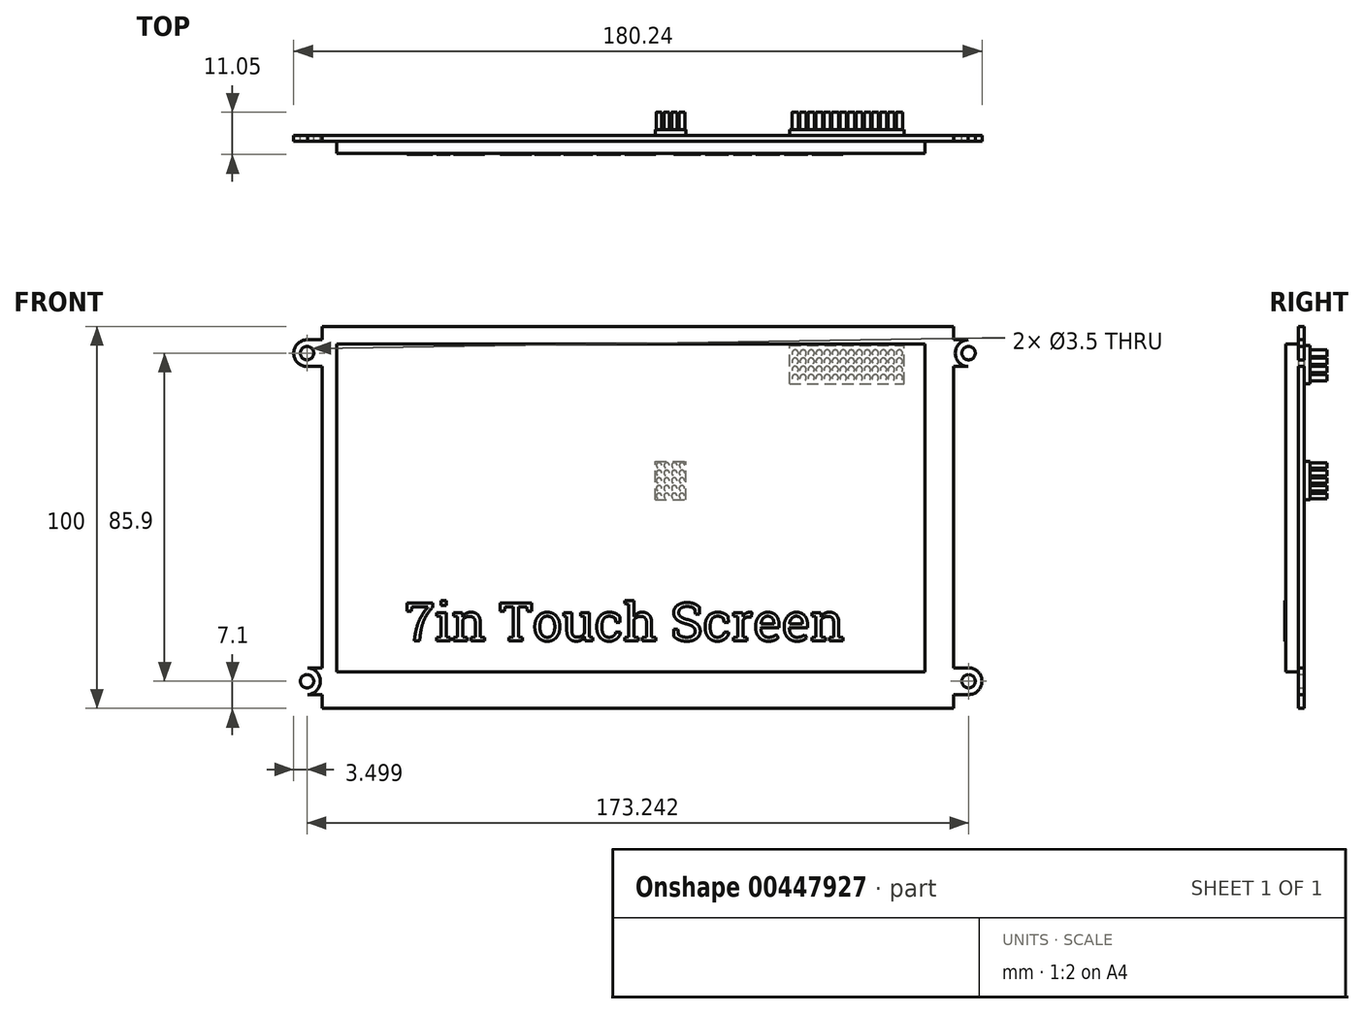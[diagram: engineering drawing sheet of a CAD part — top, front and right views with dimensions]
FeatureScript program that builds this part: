
annotation { "Feature Type Name" : "Feature", "Feature Type Description" : "" }
export const myFeature = defineFeature(function(context is Context, id is Id, definition is map)
    precondition{}
    {
        {
            var Q0;
            Q0=qCreatedBy(makeId("Front.planeOp"),FACE);
            var sketch = newSketch(context, id + "F0", { "sketchPlane" : qUnion([Q0])});
            skPoint(sketch, "E0.middle", {"position": v(0, 0) * mm});
            skCircle(sketch, "E1", {"center": v(-86.62, 42.95) * mm, "radius": 1.75 * mm});
            skLineSegment(sketch, "E2.bottom", {"start": v(-82.7, 46.45) * mm, "end": v(-86.45, 46.45) * mm});
            skLineSegment(sketch, "E2.top", {"start": v(-82.7, 39.45) * mm, "end": v(-86.45, 39.45) * mm});
            skLineSegment(sketch, "E2.left", {"start": v(-82.7, 46.45) * mm, "end": v(-82.7, 39.45) * mm});
            skCircle(sketch, "E3", {"center": v(-86.62, 42.95) * mm, "radius": 3.5 * mm});
            skPoint(sketch, "E4", {"position": v(-86.45, 46.45) * mm});
            skPoint(sketch, "E5", {"position": v(-86.45, 39.45) * mm});
            skPoint(sketch, "E6.MirrorP", {"position": v(86.62, 42.95) * mm});
            skCircle(sketch, "E7.MirrorC", {"center": v(86.62, 42.95) * mm, "radius": 1.75 * mm});
            skCircle(sketch, "E8.MirrorC", {"center": v(86.62, 42.95) * mm, "radius": 3.5 * mm});
            skLineSegment(sketch, "E9.MirrorCS", {"start": v(82.7, 39.45) * mm, "end": v(86.45, 39.45) * mm});
            skLineSegment(sketch, "E10.MirrorCS", {"start": v(82.7, 46.45) * mm, "end": v(82.7, 39.45) * mm});
            skLineSegment(sketch, "E11.MirrorCS", {"start": v(82.7, 46.45) * mm, "end": v(86.45, 46.45) * mm});
            skCircle(sketch, "E12.MirrorC", {"center": v(-86.62, -42.95) * mm, "radius": 1.75 * mm});
            skCircle(sketch, "E13.MirrorC", {"center": v(86.62, -42.95) * mm, "radius": 1.75 * mm});
            skLineSegment(sketch, "E14.MirrorCS", {"start": v(-82.7, -39.45) * mm, "end": v(-86.45, -39.45) * mm});
            skLineSegment(sketch, "E15.MirrorCS", {"start": v(-82.7, -46.45) * mm, "end": v(-82.7, -39.45) * mm});
            skLineSegment(sketch, "E16.MirrorCS", {"start": v(82.7, -46.45) * mm, "end": v(86.45, -46.45) * mm});
            skLineSegment(sketch, "E17.MirrorCS", {"start": v(-82.7, -46.45) * mm, "end": v(-86.45, -46.45) * mm});
            skLineSegment(sketch, "E18.MirrorCS", {"start": v(82.7, -46.45) * mm, "end": v(82.7, -39.45) * mm});
            skLineSegment(sketch, "E19.MirrorCS", {"start": v(82.7, -39.45) * mm, "end": v(86.45, -39.45) * mm});
            skCircle(sketch, "E20.MirrorC", {"center": v(-86.62, -42.95) * mm, "radius": 3.5 * mm});
            skCircle(sketch, "E21.MirrorC", {"center": v(86.62, -42.95) * mm, "radius": 3.5 * mm});
            skPoint(sketch, "E22.MirrorP", {"position": v(-86.45, -46.45) * mm});
            skPoint(sketch, "E23.MirrorP", {"position": v(-86.45, -39.45) * mm});
            skLineSegment(sketch, "E24.bottom", {"start": v(-78.92, 45.35) * mm, "end": v(75.18, 45.35) * mm});
            skLineSegment(sketch, "E24.top", {"start": v(-78.92, -40.55) * mm, "end": v(75.18, -40.55) * mm});
            skLineSegment(sketch, "E24.left", {"start": v(-78.92, 45.35) * mm, "end": v(-78.92, -40.55) * mm});
            skLineSegment(sketch, "E24.right", {"start": v(75.18, 45.35) * mm, "end": v(75.18, -40.55) * mm});
            skPoint(sketch, "E24.middle", {"position": v(-1.87, 2.4) * mm});
            skLineSegment(sketch, "E25.bottom", {"start": v(-82.7, 49.95) * mm, "end": v(82.7, 49.95) * mm});
            skLineSegment(sketch, "E25.top", {"start": v(-82.7, -50.05) * mm, "end": v(82.7, -50.05) * mm});
            skLineSegment(sketch, "E25.left", {"start": v(-82.7, 49.95) * mm, "end": v(-82.7, -50.05) * mm});
            skLineSegment(sketch, "E25.right", {"start": v(82.7, 49.95) * mm, "end": v(82.7, -50.05) * mm});
            skLineSegment(sketch, "E26", {"start": v(-86.45, 46.45) * mm, "end": v(-86.45, 46.45) * mm});
            skLineSegment(sketch, "E27.trimOffspring", {"start": v(-86.45, 39.45) * mm, "end": v(-86.45, 39.45) * mm});
            skLineSegment(sketch, "E28", {"start": v(-82.7, -39.45) * mm, "end": v(-82.7, -46.45) * mm});
            skLineSegment(sketch, "E29", {"start": v(-86.45, -39.45) * mm, "end": v(-86.45, -39.45) * mm});
            skLineSegment(sketch, "E30.trimOffspring", {"start": v(-86.45, -46.45) * mm, "end": v(-86.45, -46.45) * mm});
            skLineSegment(sketch, "E31", {"start": v(82.7, -39.45) * mm, "end": v(82.7, -46.45) * mm});
            skLineSegment(sketch, "E32", {"start": v(86.45, -39.45) * mm, "end": v(86.45, -39.45) * mm});
            skLineSegment(sketch, "E33.trimOffspring", {"start": v(86.45, -46.45) * mm, "end": v(86.45, -46.45) * mm});
            skLineSegment(sketch, "E34", {"start": v(86.45, 46.45) * mm, "end": v(86.45, 46.45) * mm});
            skLineSegment(sketch, "E35.trimOffspring", {"start": v(86.45, 39.45) * mm, "end": v(86.45, 39.45) * mm});
            skSolve(sketch);
        }
        {
            var Q0;
            Q0=makeQuery(id+"F0.imprint","IMPRINT",FACE,{"disambiguationData":[TD([[makeQuery(id+"F0.imprint","IMPRINT",EDGE,{"derivedFrom":sQuery(id+"F0.wireOp",EDGE,"E1")}),-1.0]])]});
            var Q1;
            {var subQ4=sQuery(id+"F0.wireOp",EDGE,"E2.bottom");Q1=makeQuery(id+"F0.imprint","IMPRINT",FACE,{"disambiguationData":[TD([[makeQuery(id+"F0.imprint","IMPRINT",EDGE,{"derivedFrom":subQ4}),1.0]])]});}
            var Q2;
            Q2=makeQuery(id+"F0.imprint","IMPRINT",FACE,{"disambiguationData":[TD([[makeQuery(id+"F0.imprint","IMPRINT",EDGE,{"derivedFrom":sQuery(id+"F0.wireOp",EDGE,"E24.bottom")}),1.0]])]});
            var Q3;
            Q3=makeQuery(id+"F0.imprint","IMPRINT",FACE,{"disambiguationData":[TD([[makeQuery(id+"F0.imprint","IMPRINT",EDGE,{"derivedFrom":sQuery(id+"F0.wireOp",EDGE,"E14.MirrorCS")}),1.0]])]});
            var Q4;
            Q4=makeQuery(id+"F0.imprint","IMPRINT",FACE,{"disambiguationData":[TD([[makeQuery(id+"F0.imprint","IMPRINT",EDGE,{"derivedFrom":sQuery(id+"F0.wireOp",EDGE,"E12.MirrorC")}),1.0]])]});
            var Q5;
            Q5=makeQuery(id+"F0.imprint","IMPRINT",FACE,{"disambiguationData":[TD([[makeQuery(id+"F0.imprint","IMPRINT",EDGE,{"derivedFrom":sQuery(id+"F0.wireOp",EDGE,"E13.MirrorC")}),-1.0]])]});
            var Q6;
            Q6=makeQuery(id+"F0.imprint","IMPRINT",FACE,{"disambiguationData":[TD([[makeQuery(id+"F0.imprint","IMPRINT",EDGE,{"derivedFrom":sQuery(id+"F0.wireOp",EDGE,"E16.MirrorCS")}),1.0]])]});
            var Q7;
            Q7=makeQuery(id+"F0.imprint","IMPRINT",FACE,{"disambiguationData":[TD([[makeQuery(id+"F0.imprint","IMPRINT",EDGE,{"derivedFrom":sQuery(id+"F0.wireOp",EDGE,"E7.MirrorC")}),1.0]])]});
            var Q8;
            Q8=makeQuery(id+"F0.imprint","IMPRINT",FACE,{"disambiguationData":[TD([[makeQuery(id+"F0.imprint","IMPRINT",EDGE,{"derivedFrom":sQuery(id+"F0.wireOp",EDGE,"E9.MirrorCS")}),1.0]])]});
            extrude(context, id + "F1", {"entities" : qUnion([Q0, Q1, Q2, Q3, Q4, Q5, Q6, Q7, Q8]), "depth" : 1.6 * mm});
        }
        {
            var Q0;
            Q0=makeQuery(id+"F0.imprint","IMPRINT",FACE,{"disambiguationData":[TD([[makeQuery(id+"F0.imprint","IMPRINT",EDGE,{"derivedFrom":sQuery(id+"F0.wireOp",EDGE,"E24.bottom")}),-1.0]])]});
            extrude(context, id + "F2", {"entities" : qUnion([Q0]), "operationType" : NewBodyOperationType.ADD, "depth" : 4.8 * mm});
        }
        {
            var Q0;
            {var subQ0=sQuery(id+"F0.wireOp",EDGE,"E24.right");var subQ1=sQuery(id+"F0.wireOp",EDGE,"E24.left");var subQ2=sQuery(id+"F0.wireOp",EDGE,"E24.top");var subQ3=sQuery(id+"F0.wireOp",EDGE,"E24.bottom");Q0=makeQuery(id+"F2.boolean.opBoolean","MERGE",FACE,{"derivedFrom":[makeQuery(id+"F1.opExtrude","CAP_FACE",FACE,{"disambiguationData":[OSD([sQuery(id+"F0.wireOp",EDGE,"E1"),sQuery(id+"F0.wireOp",EDGE,"E2.bottom"),sQuery(id+"F0.wireOp",EDGE,"E2.top"),sQuery(id+"F0.wireOp",EDGE,"E3"),sQuery(id+"F0.wireOp",EDGE,"E7.MirrorC"),sQuery(id+"F0.wireOp",EDGE,"E8.MirrorC"),sQuery(id+"F0.wireOp",EDGE,"E9.MirrorCS"),sQuery(id+"F0.wireOp",EDGE,"E11.MirrorCS"),sQuery(id+"F0.wireOp",EDGE,"E12.MirrorC"),sQuery(id+"F0.wireOp",EDGE,"E13.MirrorC"),sQuery(id+"F0.wireOp",EDGE,"E14.MirrorCS"),sQuery(id+"F0.wireOp",EDGE,"E16.MirrorCS"),sQuery(id+"F0.wireOp",EDGE,"E17.MirrorCS"),sQuery(id+"F0.wireOp",EDGE,"E19.MirrorCS"),sQuery(id+"F0.wireOp",EDGE,"E20.MirrorC"),sQuery(id+"F0.wireOp",EDGE,"E21.MirrorC"),subQ3,subQ2,subQ1,subQ0,sQuery(id+"F0.wireOp",EDGE,"E25.bottom"),sQuery(id+"F0.wireOp",EDGE,"E25.top"),sQuery(id+"F0.wireOp",EDGE,"E25.left"),sQuery(id+"F0.wireOp",EDGE,"E25.right"),sQuery(id+"F0.wireOp",EDGE,"E26"),sQuery(id+"F0.wireOp",EDGE,"E27.trimOffspring"),sQuery(id+"F0.wireOp",EDGE,"E29"),sQuery(id+"F0.wireOp",EDGE,"E30.trimOffspring"),sQuery(id+"F0.wireOp",EDGE,"E32"),sQuery(id+"F0.wireOp",EDGE,"E33.trimOffspring"),sQuery(id+"F0.wireOp",EDGE,"E34"),sQuery(id+"F0.wireOp",EDGE,"E35.trimOffspring")])],"isStart":true}),makeQuery(id+"F2.opExtrude","CAP_FACE",FACE,{"disambiguationData":[OSD([subQ3,subQ2,subQ1,subQ0])],"isStart":true})]});}
            var sketch = newSketch(context, id + "F3", { "sketchPlane" : qUnion([Q0])});
            skLineSegment(sketch, "E36.bottom", {"start": v(-39.7, 44.95) * mm, "end": v(-69.7, 44.95) * mm});
            skLineSegment(sketch, "E36.top", {"start": v(-39.7, 34.95) * mm, "end": v(-69.7, 34.95) * mm});
            skLineSegment(sketch, "E36.left", {"start": v(-39.7, 34.95) * mm, "end": v(-39.7, 44.95) * mm});
            skLineSegment(sketch, "E36.right", {"start": v(-69.7, 34.95) * mm, "end": v(-69.7, 44.95) * mm});
            skPoint(sketch, "E36.middle", {"position": v(-54.7, 39.95) * mm});
            skLineSegment(sketch, "E37.bottom", {"start": v(-4.57, 4.56) * mm, "end": v(-12.57, 4.56) * mm});
            skLineSegment(sketch, "E37.top", {"start": v(-4.57, 14.56) * mm, "end": v(-12.57, 14.56) * mm});
            skLineSegment(sketch, "E37.left", {"start": v(-4.57, 4.56) * mm, "end": v(-4.57, 14.56) * mm});
            skLineSegment(sketch, "E37.right", {"start": v(-12.57, 4.56) * mm, "end": v(-12.57, 14.56) * mm});
            skPoint(sketch, "E37.middle", {"position": v(-8.57, 9.56) * mm});
            skCircle(sketch, "E38", {"center": v(-68.5, 42.95) * mm, "radius": 0.84 * mm});
            skCircle(sketch, "E39.1.0.0", {"center": v(-66.4, 42.95) * mm, "radius": 0.84 * mm});
            skCircle(sketch, "E39.2.0.0", {"center": v(-64.3, 42.95) * mm, "radius": 0.84 * mm});
            skCircle(sketch, "E39.3.0.0", {"center": v(-62.2, 42.95) * mm, "radius": 0.84 * mm});
            skCircle(sketch, "E39.4.0.0", {"center": v(-60.1, 42.95) * mm, "radius": 0.84 * mm});
            skCircle(sketch, "E39.5.0.0", {"center": v(-58, 42.95) * mm, "radius": 0.84 * mm});
            skCircle(sketch, "E39.6.0.0", {"center": v(-55.9, 42.95) * mm, "radius": 0.84 * mm});
            skCircle(sketch, "E39.7.0.0", {"center": v(-53.8, 42.95) * mm, "radius": 0.84 * mm});
            skCircle(sketch, "E39.8.0.0", {"center": v(-51.7, 42.95) * mm, "radius": 0.84 * mm});
            skCircle(sketch, "E39.9.0.0", {"center": v(-49.6, 42.95) * mm, "radius": 0.84 * mm});
            skCircle(sketch, "E39.10.0.0", {"center": v(-47.5, 42.95) * mm, "radius": 0.84 * mm});
            skCircle(sketch, "E39.11.0.0", {"center": v(-45.4, 42.95) * mm, "radius": 0.84 * mm});
            skCircle(sketch, "E39.12.0.0", {"center": v(-43.3, 42.95) * mm, "radius": 0.84 * mm});
            skLineSegment(sketch, "E39.direction1", {"start": v(-68.5, 42.95) * mm, "end": v(-66.4, 42.95) * mm, "construction": true});
            skCircle(sketch, "E40.0.13.0", {"center": v(-41.2, 42.95) * mm, "radius": 0.84 * mm});
            skCircle(sketch, "E41.1.0.0", {"center": v(-58, 40.8) * mm, "radius": 0.84 * mm});
            skCircle(sketch, "E41.1.0.1", {"center": v(-68.5, 40.8) * mm, "radius": 0.84 * mm});
            skCircle(sketch, "E41.1.0.2", {"center": v(-53.8, 40.8) * mm, "radius": 0.84 * mm});
            skCircle(sketch, "E41.1.0.3", {"center": v(-47.5, 40.8) * mm, "radius": 0.84 * mm});
            skCircle(sketch, "E41.1.0.4", {"center": v(-41.2, 40.8) * mm, "radius": 0.84 * mm});
            skCircle(sketch, "E41.1.0.5", {"center": v(-43.3, 40.8) * mm, "radius": 0.84 * mm});
            skCircle(sketch, "E41.1.0.6", {"center": v(-51.7, 40.8) * mm, "radius": 0.84 * mm});
            skCircle(sketch, "E41.1.0.7", {"center": v(-60.1, 40.8) * mm, "radius": 0.84 * mm});
            skCircle(sketch, "E41.1.0.8", {"center": v(-62.2, 40.8) * mm, "radius": 0.84 * mm});
            skCircle(sketch, "E41.1.0.9", {"center": v(-64.3, 40.8) * mm, "radius": 0.84 * mm});
            skCircle(sketch, "E41.1.0.10", {"center": v(-66.4, 40.8) * mm, "radius": 0.84 * mm});
            skCircle(sketch, "E41.1.0.11", {"center": v(-55.9, 40.8) * mm, "radius": 0.84 * mm});
            skCircle(sketch, "E41.1.0.12", {"center": v(-49.6, 40.8) * mm, "radius": 0.84 * mm});
            skLineSegment(sketch, "E41.1.0.13", {"start": v(-68.5, 40.8) * mm, "end": v(-66.4, 40.8) * mm, "construction": true});
            skCircle(sketch, "E41.1.0.14", {"center": v(-45.4, 40.8) * mm, "radius": 0.84 * mm});
            skCircle(sketch, "E41.2.0.0", {"center": v(-58, 38.65) * mm, "radius": 0.84 * mm});
            skCircle(sketch, "E41.2.0.1", {"center": v(-68.5, 38.65) * mm, "radius": 0.84 * mm});
            skCircle(sketch, "E41.2.0.2", {"center": v(-53.8, 38.65) * mm, "radius": 0.84 * mm});
            skCircle(sketch, "E41.2.0.3", {"center": v(-47.5, 38.65) * mm, "radius": 0.84 * mm});
            skCircle(sketch, "E41.2.0.4", {"center": v(-41.2, 38.65) * mm, "radius": 0.84 * mm});
            skCircle(sketch, "E41.2.0.5", {"center": v(-43.3, 38.65) * mm, "radius": 0.84 * mm});
            skCircle(sketch, "E41.2.0.6", {"center": v(-51.7, 38.65) * mm, "radius": 0.84 * mm});
            skCircle(sketch, "E41.2.0.7", {"center": v(-60.1, 38.65) * mm, "radius": 0.84 * mm});
            skCircle(sketch, "E41.2.0.8", {"center": v(-62.2, 38.65) * mm, "radius": 0.84 * mm});
            skCircle(sketch, "E41.2.0.9", {"center": v(-64.3, 38.65) * mm, "radius": 0.84 * mm});
            skCircle(sketch, "E41.2.0.10", {"center": v(-66.4, 38.65) * mm, "radius": 0.84 * mm});
            skCircle(sketch, "E41.2.0.11", {"center": v(-55.9, 38.65) * mm, "radius": 0.84 * mm});
            skCircle(sketch, "E41.2.0.12", {"center": v(-49.6, 38.65) * mm, "radius": 0.84 * mm});
            skLineSegment(sketch, "E41.2.0.13", {"start": v(-68.5, 38.65) * mm, "end": v(-66.4, 38.65) * mm, "construction": true});
            skCircle(sketch, "E41.2.0.14", {"center": v(-45.4, 38.65) * mm, "radius": 0.84 * mm});
            skCircle(sketch, "E41.3.0.0", {"center": v(-58, 36.5) * mm, "radius": 0.84 * mm});
            skCircle(sketch, "E41.3.0.1", {"center": v(-68.5, 36.5) * mm, "radius": 0.84 * mm});
            skCircle(sketch, "E41.3.0.2", {"center": v(-53.8, 36.5) * mm, "radius": 0.84 * mm});
            skCircle(sketch, "E41.3.0.3", {"center": v(-47.5, 36.5) * mm, "radius": 0.84 * mm});
            skCircle(sketch, "E41.3.0.4", {"center": v(-41.2, 36.5) * mm, "radius": 0.84 * mm});
            skCircle(sketch, "E41.3.0.5", {"center": v(-43.3, 36.5) * mm, "radius": 0.84 * mm});
            skCircle(sketch, "E41.3.0.6", {"center": v(-51.7, 36.5) * mm, "radius": 0.84 * mm});
            skCircle(sketch, "E41.3.0.7", {"center": v(-60.1, 36.5) * mm, "radius": 0.84 * mm});
            skCircle(sketch, "E41.3.0.8", {"center": v(-62.2, 36.5) * mm, "radius": 0.84 * mm});
            skCircle(sketch, "E41.3.0.9", {"center": v(-64.3, 36.5) * mm, "radius": 0.84 * mm});
            skCircle(sketch, "E41.3.0.10", {"center": v(-66.4, 36.5) * mm, "radius": 0.84 * mm});
            skCircle(sketch, "E41.3.0.11", {"center": v(-55.9, 36.5) * mm, "radius": 0.84 * mm});
            skCircle(sketch, "E41.3.0.12", {"center": v(-49.6, 36.5) * mm, "radius": 0.84 * mm});
            skLineSegment(sketch, "E41.3.0.13", {"start": v(-68.5, 36.5) * mm, "end": v(-66.4, 36.5) * mm, "construction": true});
            skCircle(sketch, "E41.3.0.14", {"center": v(-45.4, 36.5) * mm, "radius": 0.84 * mm});
            skLineSegment(sketch, "E41.direction1", {"start": v(-68.5, 42.95) * mm, "end": v(-68.5, 40.8) * mm, "construction": true});
            skCircle(sketch, "E42", {"center": v(-11.57, 13.56) * mm, "radius": 0.71 * mm});
            skCircle(sketch, "E43.1.0.0", {"center": v(-9.57, 13.56) * mm, "radius": 0.71 * mm});
            skCircle(sketch, "E43.2.0.0", {"center": v(-7.57, 13.56) * mm, "radius": 0.71 * mm});
            skCircle(sketch, "E43.3.0.0", {"center": v(-5.57, 13.56) * mm, "radius": 0.71 * mm});
            skLineSegment(sketch, "E43.direction1", {"start": v(-11.57, 13.56) * mm, "end": v(-9.57, 13.56) * mm, "construction": true});
            skCircle(sketch, "E44.1.0.0", {"center": v(-11.56, 11.56) * mm, "radius": 0.71 * mm});
            skCircle(sketch, "E44.1.0.1", {"center": v(-9.56, 11.56) * mm, "radius": 0.71 * mm});
            skCircle(sketch, "E44.1.0.2", {"center": v(-7.56, 11.56) * mm, "radius": 0.71 * mm});
            skCircle(sketch, "E44.1.0.3", {"center": v(-5.56, 11.56) * mm, "radius": 0.71 * mm});
            skCircle(sketch, "E44.2.0.0", {"center": v(-11.55, 9.56) * mm, "radius": 0.71 * mm});
            skCircle(sketch, "E44.2.0.1", {"center": v(-9.55, 9.56) * mm, "radius": 0.71 * mm});
            skCircle(sketch, "E44.2.0.2", {"center": v(-7.55, 9.56) * mm, "radius": 0.71 * mm});
            skCircle(sketch, "E44.2.0.3", {"center": v(-5.55, 9.56) * mm, "radius": 0.71 * mm});
            skCircle(sketch, "E44.3.0.0", {"center": v(-11.55, 7.56) * mm, "radius": 0.71 * mm});
            skCircle(sketch, "E44.3.0.1", {"center": v(-9.55, 7.56) * mm, "radius": 0.71 * mm});
            skCircle(sketch, "E44.3.0.2", {"center": v(-7.55, 7.56) * mm, "radius": 0.71 * mm});
            skCircle(sketch, "E44.3.0.3", {"center": v(-5.55, 7.56) * mm, "radius": 0.71 * mm});
            skCircle(sketch, "E44.4.0.0", {"center": v(-11.54, 5.56) * mm, "radius": 0.71 * mm});
            skCircle(sketch, "E44.4.0.1", {"center": v(-9.54, 5.56) * mm, "radius": 0.71 * mm});
            skCircle(sketch, "E44.4.0.2", {"center": v(-7.54, 5.56) * mm, "radius": 0.71 * mm});
            skCircle(sketch, "E44.4.0.3", {"center": v(-5.54, 5.56) * mm, "radius": 0.71 * mm});
            skLineSegment(sketch, "E44.direction1", {"start": v(-11.57, 13.56) * mm, "end": v(-11.56, 11.56) * mm, "construction": true});
            skSolve(sketch);
        }
        {
            var Q0;
            Q0=makeQuery(id+"F3.imprint","IMPRINT",FACE,{"disambiguationData":[TD([[makeQuery(id+"F3.imprint","IMPRINT",EDGE,{"derivedFrom":sQuery(id+"F3.wireOp",EDGE,"E36.bottom")}),1.0]])]});
            extrude(context, id + "F4", {"entities" : qUnion([Q0]), "operationType" : NewBodyOperationType.ADD, "depth" : 1.5 * mm});
        }
        {
            var Q0;
            {var subQ0=sQuery(id+"F0.wireOp",EDGE,"E24.right");var subQ1=sQuery(id+"F0.wireOp",EDGE,"E24.left");var subQ2=sQuery(id+"F0.wireOp",EDGE,"E24.top");var subQ3=sQuery(id+"F0.wireOp",EDGE,"E24.bottom");Q0=makeQuery(id+"F4.boolean.opBoolean","SPLIT",FACE,{"disambiguationData":[TD([makeQuery(id+"F4.opExtrude","SWEPT_FACE",FACE,{"disambiguationData":[OSD([sQuery(id+"F3.wireOp",EDGE,"E38")])]})])],"derivedFrom":makeQuery(id+"F2.boolean.opBoolean","MERGE",FACE,{"derivedFrom":[makeQuery(id+"F1.opExtrude","CAP_FACE",FACE,{"disambiguationData":[OSD([sQuery(id+"F0.wireOp",EDGE,"E1"),sQuery(id+"F0.wireOp",EDGE,"E2.bottom"),sQuery(id+"F0.wireOp",EDGE,"E2.top"),sQuery(id+"F0.wireOp",EDGE,"E3"),sQuery(id+"F0.wireOp",EDGE,"E7.MirrorC"),sQuery(id+"F0.wireOp",EDGE,"E8.MirrorC"),sQuery(id+"F0.wireOp",EDGE,"E9.MirrorCS"),sQuery(id+"F0.wireOp",EDGE,"E11.MirrorCS"),sQuery(id+"F0.wireOp",EDGE,"E12.MirrorC"),sQuery(id+"F0.wireOp",EDGE,"E13.MirrorC"),sQuery(id+"F0.wireOp",EDGE,"E14.MirrorCS"),sQuery(id+"F0.wireOp",EDGE,"E16.MirrorCS"),sQuery(id+"F0.wireOp",EDGE,"E17.MirrorCS"),sQuery(id+"F0.wireOp",EDGE,"E19.MirrorCS"),sQuery(id+"F0.wireOp",EDGE,"E20.MirrorC"),sQuery(id+"F0.wireOp",EDGE,"E21.MirrorC"),subQ3,subQ2,subQ1,subQ0,sQuery(id+"F0.wireOp",EDGE,"E25.bottom"),sQuery(id+"F0.wireOp",EDGE,"E25.top"),sQuery(id+"F0.wireOp",EDGE,"E25.left"),sQuery(id+"F0.wireOp",EDGE,"E25.right"),sQuery(id+"F0.wireOp",EDGE,"E26"),sQuery(id+"F0.wireOp",EDGE,"E27.trimOffspring"),sQuery(id+"F0.wireOp",EDGE,"E29"),sQuery(id+"F0.wireOp",EDGE,"E30.trimOffspring"),sQuery(id+"F0.wireOp",EDGE,"E32"),sQuery(id+"F0.wireOp",EDGE,"E33.trimOffspring"),sQuery(id+"F0.wireOp",EDGE,"E34"),sQuery(id+"F0.wireOp",EDGE,"E35.trimOffspring")])],"isStart":true}),makeQuery(id+"F2.opExtrude","CAP_FACE",FACE,{"disambiguationData":[OSD([subQ3,subQ2,subQ1,subQ0])],"isStart":true})]})});}
            var Q1;
            {var subQ0=sQuery(id+"F0.wireOp",EDGE,"E24.right");var subQ1=sQuery(id+"F0.wireOp",EDGE,"E24.left");var subQ2=sQuery(id+"F0.wireOp",EDGE,"E24.top");var subQ3=sQuery(id+"F0.wireOp",EDGE,"E24.bottom");Q1=makeQuery(id+"F4.boolean.opBoolean","SPLIT",FACE,{"disambiguationData":[TD([makeQuery(id+"F4.opExtrude","SWEPT_FACE",FACE,{"disambiguationData":[OSD([sQuery(id+"F3.wireOp",EDGE,"E39.1.0.0")])]})])],"derivedFrom":makeQuery(id+"F2.boolean.opBoolean","MERGE",FACE,{"derivedFrom":[makeQuery(id+"F1.opExtrude","CAP_FACE",FACE,{"disambiguationData":[OSD([sQuery(id+"F0.wireOp",EDGE,"E1"),sQuery(id+"F0.wireOp",EDGE,"E2.bottom"),sQuery(id+"F0.wireOp",EDGE,"E2.top"),sQuery(id+"F0.wireOp",EDGE,"E3"),sQuery(id+"F0.wireOp",EDGE,"E7.MirrorC"),sQuery(id+"F0.wireOp",EDGE,"E8.MirrorC"),sQuery(id+"F0.wireOp",EDGE,"E9.MirrorCS"),sQuery(id+"F0.wireOp",EDGE,"E11.MirrorCS"),sQuery(id+"F0.wireOp",EDGE,"E12.MirrorC"),sQuery(id+"F0.wireOp",EDGE,"E13.MirrorC"),sQuery(id+"F0.wireOp",EDGE,"E14.MirrorCS"),sQuery(id+"F0.wireOp",EDGE,"E16.MirrorCS"),sQuery(id+"F0.wireOp",EDGE,"E17.MirrorCS"),sQuery(id+"F0.wireOp",EDGE,"E19.MirrorCS"),sQuery(id+"F0.wireOp",EDGE,"E20.MirrorC"),sQuery(id+"F0.wireOp",EDGE,"E21.MirrorC"),subQ3,subQ2,subQ1,subQ0,sQuery(id+"F0.wireOp",EDGE,"E25.bottom"),sQuery(id+"F0.wireOp",EDGE,"E25.top"),sQuery(id+"F0.wireOp",EDGE,"E25.left"),sQuery(id+"F0.wireOp",EDGE,"E25.right"),sQuery(id+"F0.wireOp",EDGE,"E26"),sQuery(id+"F0.wireOp",EDGE,"E27.trimOffspring"),sQuery(id+"F0.wireOp",EDGE,"E29"),sQuery(id+"F0.wireOp",EDGE,"E30.trimOffspring"),sQuery(id+"F0.wireOp",EDGE,"E32"),sQuery(id+"F0.wireOp",EDGE,"E33.trimOffspring"),sQuery(id+"F0.wireOp",EDGE,"E34"),sQuery(id+"F0.wireOp",EDGE,"E35.trimOffspring")])],"isStart":true}),makeQuery(id+"F2.opExtrude","CAP_FACE",FACE,{"disambiguationData":[OSD([subQ3,subQ2,subQ1,subQ0])],"isStart":true})]})});}
            var Q2;
            {var subQ0=sQuery(id+"F0.wireOp",EDGE,"E24.right");var subQ1=sQuery(id+"F0.wireOp",EDGE,"E24.left");var subQ2=sQuery(id+"F0.wireOp",EDGE,"E24.top");var subQ3=sQuery(id+"F0.wireOp",EDGE,"E24.bottom");Q2=makeQuery(id+"F4.boolean.opBoolean","SPLIT",FACE,{"disambiguationData":[TD([makeQuery(id+"F4.opExtrude","SWEPT_FACE",FACE,{"disambiguationData":[OSD([sQuery(id+"F3.wireOp",EDGE,"E39.2.0.0")])]})])],"derivedFrom":makeQuery(id+"F2.boolean.opBoolean","MERGE",FACE,{"derivedFrom":[makeQuery(id+"F1.opExtrude","CAP_FACE",FACE,{"disambiguationData":[OSD([sQuery(id+"F0.wireOp",EDGE,"E1"),sQuery(id+"F0.wireOp",EDGE,"E2.bottom"),sQuery(id+"F0.wireOp",EDGE,"E2.top"),sQuery(id+"F0.wireOp",EDGE,"E3"),sQuery(id+"F0.wireOp",EDGE,"E7.MirrorC"),sQuery(id+"F0.wireOp",EDGE,"E8.MirrorC"),sQuery(id+"F0.wireOp",EDGE,"E9.MirrorCS"),sQuery(id+"F0.wireOp",EDGE,"E11.MirrorCS"),sQuery(id+"F0.wireOp",EDGE,"E12.MirrorC"),sQuery(id+"F0.wireOp",EDGE,"E13.MirrorC"),sQuery(id+"F0.wireOp",EDGE,"E14.MirrorCS"),sQuery(id+"F0.wireOp",EDGE,"E16.MirrorCS"),sQuery(id+"F0.wireOp",EDGE,"E17.MirrorCS"),sQuery(id+"F0.wireOp",EDGE,"E19.MirrorCS"),sQuery(id+"F0.wireOp",EDGE,"E20.MirrorC"),sQuery(id+"F0.wireOp",EDGE,"E21.MirrorC"),subQ3,subQ2,subQ1,subQ0,sQuery(id+"F0.wireOp",EDGE,"E25.bottom"),sQuery(id+"F0.wireOp",EDGE,"E25.top"),sQuery(id+"F0.wireOp",EDGE,"E25.left"),sQuery(id+"F0.wireOp",EDGE,"E25.right"),sQuery(id+"F0.wireOp",EDGE,"E26"),sQuery(id+"F0.wireOp",EDGE,"E27.trimOffspring"),sQuery(id+"F0.wireOp",EDGE,"E29"),sQuery(id+"F0.wireOp",EDGE,"E30.trimOffspring"),sQuery(id+"F0.wireOp",EDGE,"E32"),sQuery(id+"F0.wireOp",EDGE,"E33.trimOffspring"),sQuery(id+"F0.wireOp",EDGE,"E34"),sQuery(id+"F0.wireOp",EDGE,"E35.trimOffspring")])],"isStart":true}),makeQuery(id+"F2.opExtrude","CAP_FACE",FACE,{"disambiguationData":[OSD([subQ3,subQ2,subQ1,subQ0])],"isStart":true})]})});}
            var Q3;
            {var subQ0=sQuery(id+"F0.wireOp",EDGE,"E24.right");var subQ1=sQuery(id+"F0.wireOp",EDGE,"E24.left");var subQ2=sQuery(id+"F0.wireOp",EDGE,"E24.top");var subQ3=sQuery(id+"F0.wireOp",EDGE,"E24.bottom");Q3=makeQuery(id+"F4.boolean.opBoolean","SPLIT",FACE,{"disambiguationData":[TD([makeQuery(id+"F4.opExtrude","SWEPT_FACE",FACE,{"disambiguationData":[OSD([sQuery(id+"F3.wireOp",EDGE,"E39.3.0.0")])]})])],"derivedFrom":makeQuery(id+"F2.boolean.opBoolean","MERGE",FACE,{"derivedFrom":[makeQuery(id+"F1.opExtrude","CAP_FACE",FACE,{"disambiguationData":[OSD([sQuery(id+"F0.wireOp",EDGE,"E1"),sQuery(id+"F0.wireOp",EDGE,"E2.bottom"),sQuery(id+"F0.wireOp",EDGE,"E2.top"),sQuery(id+"F0.wireOp",EDGE,"E3"),sQuery(id+"F0.wireOp",EDGE,"E7.MirrorC"),sQuery(id+"F0.wireOp",EDGE,"E8.MirrorC"),sQuery(id+"F0.wireOp",EDGE,"E9.MirrorCS"),sQuery(id+"F0.wireOp",EDGE,"E11.MirrorCS"),sQuery(id+"F0.wireOp",EDGE,"E12.MirrorC"),sQuery(id+"F0.wireOp",EDGE,"E13.MirrorC"),sQuery(id+"F0.wireOp",EDGE,"E14.MirrorCS"),sQuery(id+"F0.wireOp",EDGE,"E16.MirrorCS"),sQuery(id+"F0.wireOp",EDGE,"E17.MirrorCS"),sQuery(id+"F0.wireOp",EDGE,"E19.MirrorCS"),sQuery(id+"F0.wireOp",EDGE,"E20.MirrorC"),sQuery(id+"F0.wireOp",EDGE,"E21.MirrorC"),subQ3,subQ2,subQ1,subQ0,sQuery(id+"F0.wireOp",EDGE,"E25.bottom"),sQuery(id+"F0.wireOp",EDGE,"E25.top"),sQuery(id+"F0.wireOp",EDGE,"E25.left"),sQuery(id+"F0.wireOp",EDGE,"E25.right"),sQuery(id+"F0.wireOp",EDGE,"E26"),sQuery(id+"F0.wireOp",EDGE,"E27.trimOffspring"),sQuery(id+"F0.wireOp",EDGE,"E29"),sQuery(id+"F0.wireOp",EDGE,"E30.trimOffspring"),sQuery(id+"F0.wireOp",EDGE,"E32"),sQuery(id+"F0.wireOp",EDGE,"E33.trimOffspring"),sQuery(id+"F0.wireOp",EDGE,"E34"),sQuery(id+"F0.wireOp",EDGE,"E35.trimOffspring")])],"isStart":true}),makeQuery(id+"F2.opExtrude","CAP_FACE",FACE,{"disambiguationData":[OSD([subQ3,subQ2,subQ1,subQ0])],"isStart":true})]})});}
            var Q4;
            {var subQ0=sQuery(id+"F0.wireOp",EDGE,"E24.right");var subQ1=sQuery(id+"F0.wireOp",EDGE,"E24.left");var subQ2=sQuery(id+"F0.wireOp",EDGE,"E24.top");var subQ3=sQuery(id+"F0.wireOp",EDGE,"E24.bottom");Q4=makeQuery(id+"F4.boolean.opBoolean","SPLIT",FACE,{"disambiguationData":[TD([makeQuery(id+"F4.opExtrude","SWEPT_FACE",FACE,{"disambiguationData":[OSD([sQuery(id+"F3.wireOp",EDGE,"E39.4.0.0")])]})])],"derivedFrom":makeQuery(id+"F2.boolean.opBoolean","MERGE",FACE,{"derivedFrom":[makeQuery(id+"F1.opExtrude","CAP_FACE",FACE,{"disambiguationData":[OSD([sQuery(id+"F0.wireOp",EDGE,"E1"),sQuery(id+"F0.wireOp",EDGE,"E2.bottom"),sQuery(id+"F0.wireOp",EDGE,"E2.top"),sQuery(id+"F0.wireOp",EDGE,"E3"),sQuery(id+"F0.wireOp",EDGE,"E7.MirrorC"),sQuery(id+"F0.wireOp",EDGE,"E8.MirrorC"),sQuery(id+"F0.wireOp",EDGE,"E9.MirrorCS"),sQuery(id+"F0.wireOp",EDGE,"E11.MirrorCS"),sQuery(id+"F0.wireOp",EDGE,"E12.MirrorC"),sQuery(id+"F0.wireOp",EDGE,"E13.MirrorC"),sQuery(id+"F0.wireOp",EDGE,"E14.MirrorCS"),sQuery(id+"F0.wireOp",EDGE,"E16.MirrorCS"),sQuery(id+"F0.wireOp",EDGE,"E17.MirrorCS"),sQuery(id+"F0.wireOp",EDGE,"E19.MirrorCS"),sQuery(id+"F0.wireOp",EDGE,"E20.MirrorC"),sQuery(id+"F0.wireOp",EDGE,"E21.MirrorC"),subQ3,subQ2,subQ1,subQ0,sQuery(id+"F0.wireOp",EDGE,"E25.bottom"),sQuery(id+"F0.wireOp",EDGE,"E25.top"),sQuery(id+"F0.wireOp",EDGE,"E25.left"),sQuery(id+"F0.wireOp",EDGE,"E25.right"),sQuery(id+"F0.wireOp",EDGE,"E26"),sQuery(id+"F0.wireOp",EDGE,"E27.trimOffspring"),sQuery(id+"F0.wireOp",EDGE,"E29"),sQuery(id+"F0.wireOp",EDGE,"E30.trimOffspring"),sQuery(id+"F0.wireOp",EDGE,"E32"),sQuery(id+"F0.wireOp",EDGE,"E33.trimOffspring"),sQuery(id+"F0.wireOp",EDGE,"E34"),sQuery(id+"F0.wireOp",EDGE,"E35.trimOffspring")])],"isStart":true}),makeQuery(id+"F2.opExtrude","CAP_FACE",FACE,{"disambiguationData":[OSD([subQ3,subQ2,subQ1,subQ0])],"isStart":true})]})});}
            var Q5;
            {var subQ0=sQuery(id+"F0.wireOp",EDGE,"E24.right");var subQ1=sQuery(id+"F0.wireOp",EDGE,"E24.left");var subQ2=sQuery(id+"F0.wireOp",EDGE,"E24.top");var subQ3=sQuery(id+"F0.wireOp",EDGE,"E24.bottom");Q5=makeQuery(id+"F4.boolean.opBoolean","SPLIT",FACE,{"disambiguationData":[TD([makeQuery(id+"F4.opExtrude","SWEPT_FACE",FACE,{"disambiguationData":[OSD([sQuery(id+"F3.wireOp",EDGE,"E39.6.0.0")])]})])],"derivedFrom":makeQuery(id+"F2.boolean.opBoolean","MERGE",FACE,{"derivedFrom":[makeQuery(id+"F1.opExtrude","CAP_FACE",FACE,{"disambiguationData":[OSD([sQuery(id+"F0.wireOp",EDGE,"E1"),sQuery(id+"F0.wireOp",EDGE,"E2.bottom"),sQuery(id+"F0.wireOp",EDGE,"E2.top"),sQuery(id+"F0.wireOp",EDGE,"E3"),sQuery(id+"F0.wireOp",EDGE,"E7.MirrorC"),sQuery(id+"F0.wireOp",EDGE,"E8.MirrorC"),sQuery(id+"F0.wireOp",EDGE,"E9.MirrorCS"),sQuery(id+"F0.wireOp",EDGE,"E11.MirrorCS"),sQuery(id+"F0.wireOp",EDGE,"E12.MirrorC"),sQuery(id+"F0.wireOp",EDGE,"E13.MirrorC"),sQuery(id+"F0.wireOp",EDGE,"E14.MirrorCS"),sQuery(id+"F0.wireOp",EDGE,"E16.MirrorCS"),sQuery(id+"F0.wireOp",EDGE,"E17.MirrorCS"),sQuery(id+"F0.wireOp",EDGE,"E19.MirrorCS"),sQuery(id+"F0.wireOp",EDGE,"E20.MirrorC"),sQuery(id+"F0.wireOp",EDGE,"E21.MirrorC"),subQ3,subQ2,subQ1,subQ0,sQuery(id+"F0.wireOp",EDGE,"E25.bottom"),sQuery(id+"F0.wireOp",EDGE,"E25.top"),sQuery(id+"F0.wireOp",EDGE,"E25.left"),sQuery(id+"F0.wireOp",EDGE,"E25.right"),sQuery(id+"F0.wireOp",EDGE,"E26"),sQuery(id+"F0.wireOp",EDGE,"E27.trimOffspring"),sQuery(id+"F0.wireOp",EDGE,"E29"),sQuery(id+"F0.wireOp",EDGE,"E30.trimOffspring"),sQuery(id+"F0.wireOp",EDGE,"E32"),sQuery(id+"F0.wireOp",EDGE,"E33.trimOffspring"),sQuery(id+"F0.wireOp",EDGE,"E34"),sQuery(id+"F0.wireOp",EDGE,"E35.trimOffspring")])],"isStart":true}),makeQuery(id+"F2.opExtrude","CAP_FACE",FACE,{"disambiguationData":[OSD([subQ3,subQ2,subQ1,subQ0])],"isStart":true})]})});}
            var Q6;
            {var subQ0=sQuery(id+"F0.wireOp",EDGE,"E24.right");var subQ1=sQuery(id+"F0.wireOp",EDGE,"E24.left");var subQ2=sQuery(id+"F0.wireOp",EDGE,"E24.top");var subQ3=sQuery(id+"F0.wireOp",EDGE,"E24.bottom");Q6=makeQuery(id+"F4.boolean.opBoolean","SPLIT",FACE,{"disambiguationData":[TD([makeQuery(id+"F4.opExtrude","SWEPT_FACE",FACE,{"disambiguationData":[OSD([sQuery(id+"F3.wireOp",EDGE,"E39.5.0.0")])]})])],"derivedFrom":makeQuery(id+"F2.boolean.opBoolean","MERGE",FACE,{"derivedFrom":[makeQuery(id+"F1.opExtrude","CAP_FACE",FACE,{"disambiguationData":[OSD([sQuery(id+"F0.wireOp",EDGE,"E1"),sQuery(id+"F0.wireOp",EDGE,"E2.bottom"),sQuery(id+"F0.wireOp",EDGE,"E2.top"),sQuery(id+"F0.wireOp",EDGE,"E3"),sQuery(id+"F0.wireOp",EDGE,"E7.MirrorC"),sQuery(id+"F0.wireOp",EDGE,"E8.MirrorC"),sQuery(id+"F0.wireOp",EDGE,"E9.MirrorCS"),sQuery(id+"F0.wireOp",EDGE,"E11.MirrorCS"),sQuery(id+"F0.wireOp",EDGE,"E12.MirrorC"),sQuery(id+"F0.wireOp",EDGE,"E13.MirrorC"),sQuery(id+"F0.wireOp",EDGE,"E14.MirrorCS"),sQuery(id+"F0.wireOp",EDGE,"E16.MirrorCS"),sQuery(id+"F0.wireOp",EDGE,"E17.MirrorCS"),sQuery(id+"F0.wireOp",EDGE,"E19.MirrorCS"),sQuery(id+"F0.wireOp",EDGE,"E20.MirrorC"),sQuery(id+"F0.wireOp",EDGE,"E21.MirrorC"),subQ3,subQ2,subQ1,subQ0,sQuery(id+"F0.wireOp",EDGE,"E25.bottom"),sQuery(id+"F0.wireOp",EDGE,"E25.top"),sQuery(id+"F0.wireOp",EDGE,"E25.left"),sQuery(id+"F0.wireOp",EDGE,"E25.right"),sQuery(id+"F0.wireOp",EDGE,"E26"),sQuery(id+"F0.wireOp",EDGE,"E27.trimOffspring"),sQuery(id+"F0.wireOp",EDGE,"E29"),sQuery(id+"F0.wireOp",EDGE,"E30.trimOffspring"),sQuery(id+"F0.wireOp",EDGE,"E32"),sQuery(id+"F0.wireOp",EDGE,"E33.trimOffspring"),sQuery(id+"F0.wireOp",EDGE,"E34"),sQuery(id+"F0.wireOp",EDGE,"E35.trimOffspring")])],"isStart":true}),makeQuery(id+"F2.opExtrude","CAP_FACE",FACE,{"disambiguationData":[OSD([subQ3,subQ2,subQ1,subQ0])],"isStart":true})]})});}
            var Q7;
            {var subQ0=sQuery(id+"F0.wireOp",EDGE,"E24.right");var subQ1=sQuery(id+"F0.wireOp",EDGE,"E24.left");var subQ2=sQuery(id+"F0.wireOp",EDGE,"E24.top");var subQ3=sQuery(id+"F0.wireOp",EDGE,"E24.bottom");Q7=makeQuery(id+"F4.boolean.opBoolean","SPLIT",FACE,{"disambiguationData":[TD([makeQuery(id+"F4.opExtrude","SWEPT_FACE",FACE,{"disambiguationData":[OSD([sQuery(id+"F3.wireOp",EDGE,"E39.7.0.0")])]})])],"derivedFrom":makeQuery(id+"F2.boolean.opBoolean","MERGE",FACE,{"derivedFrom":[makeQuery(id+"F1.opExtrude","CAP_FACE",FACE,{"disambiguationData":[OSD([sQuery(id+"F0.wireOp",EDGE,"E1"),sQuery(id+"F0.wireOp",EDGE,"E2.bottom"),sQuery(id+"F0.wireOp",EDGE,"E2.top"),sQuery(id+"F0.wireOp",EDGE,"E3"),sQuery(id+"F0.wireOp",EDGE,"E7.MirrorC"),sQuery(id+"F0.wireOp",EDGE,"E8.MirrorC"),sQuery(id+"F0.wireOp",EDGE,"E9.MirrorCS"),sQuery(id+"F0.wireOp",EDGE,"E11.MirrorCS"),sQuery(id+"F0.wireOp",EDGE,"E12.MirrorC"),sQuery(id+"F0.wireOp",EDGE,"E13.MirrorC"),sQuery(id+"F0.wireOp",EDGE,"E14.MirrorCS"),sQuery(id+"F0.wireOp",EDGE,"E16.MirrorCS"),sQuery(id+"F0.wireOp",EDGE,"E17.MirrorCS"),sQuery(id+"F0.wireOp",EDGE,"E19.MirrorCS"),sQuery(id+"F0.wireOp",EDGE,"E20.MirrorC"),sQuery(id+"F0.wireOp",EDGE,"E21.MirrorC"),subQ3,subQ2,subQ1,subQ0,sQuery(id+"F0.wireOp",EDGE,"E25.bottom"),sQuery(id+"F0.wireOp",EDGE,"E25.top"),sQuery(id+"F0.wireOp",EDGE,"E25.left"),sQuery(id+"F0.wireOp",EDGE,"E25.right"),sQuery(id+"F0.wireOp",EDGE,"E26"),sQuery(id+"F0.wireOp",EDGE,"E27.trimOffspring"),sQuery(id+"F0.wireOp",EDGE,"E29"),sQuery(id+"F0.wireOp",EDGE,"E30.trimOffspring"),sQuery(id+"F0.wireOp",EDGE,"E32"),sQuery(id+"F0.wireOp",EDGE,"E33.trimOffspring"),sQuery(id+"F0.wireOp",EDGE,"E34"),sQuery(id+"F0.wireOp",EDGE,"E35.trimOffspring")])],"isStart":true}),makeQuery(id+"F2.opExtrude","CAP_FACE",FACE,{"disambiguationData":[OSD([subQ3,subQ2,subQ1,subQ0])],"isStart":true})]})});}
            var Q8;
            {var subQ0=sQuery(id+"F0.wireOp",EDGE,"E24.right");var subQ1=sQuery(id+"F0.wireOp",EDGE,"E24.left");var subQ2=sQuery(id+"F0.wireOp",EDGE,"E24.top");var subQ3=sQuery(id+"F0.wireOp",EDGE,"E24.bottom");Q8=makeQuery(id+"F4.boolean.opBoolean","SPLIT",FACE,{"disambiguationData":[TD([makeQuery(id+"F4.opExtrude","SWEPT_FACE",FACE,{"disambiguationData":[OSD([sQuery(id+"F3.wireOp",EDGE,"E39.9.0.0")])]})])],"derivedFrom":makeQuery(id+"F2.boolean.opBoolean","MERGE",FACE,{"derivedFrom":[makeQuery(id+"F1.opExtrude","CAP_FACE",FACE,{"disambiguationData":[OSD([sQuery(id+"F0.wireOp",EDGE,"E1"),sQuery(id+"F0.wireOp",EDGE,"E2.bottom"),sQuery(id+"F0.wireOp",EDGE,"E2.top"),sQuery(id+"F0.wireOp",EDGE,"E3"),sQuery(id+"F0.wireOp",EDGE,"E7.MirrorC"),sQuery(id+"F0.wireOp",EDGE,"E8.MirrorC"),sQuery(id+"F0.wireOp",EDGE,"E9.MirrorCS"),sQuery(id+"F0.wireOp",EDGE,"E11.MirrorCS"),sQuery(id+"F0.wireOp",EDGE,"E12.MirrorC"),sQuery(id+"F0.wireOp",EDGE,"E13.MirrorC"),sQuery(id+"F0.wireOp",EDGE,"E14.MirrorCS"),sQuery(id+"F0.wireOp",EDGE,"E16.MirrorCS"),sQuery(id+"F0.wireOp",EDGE,"E17.MirrorCS"),sQuery(id+"F0.wireOp",EDGE,"E19.MirrorCS"),sQuery(id+"F0.wireOp",EDGE,"E20.MirrorC"),sQuery(id+"F0.wireOp",EDGE,"E21.MirrorC"),subQ3,subQ2,subQ1,subQ0,sQuery(id+"F0.wireOp",EDGE,"E25.bottom"),sQuery(id+"F0.wireOp",EDGE,"E25.top"),sQuery(id+"F0.wireOp",EDGE,"E25.left"),sQuery(id+"F0.wireOp",EDGE,"E25.right"),sQuery(id+"F0.wireOp",EDGE,"E26"),sQuery(id+"F0.wireOp",EDGE,"E27.trimOffspring"),sQuery(id+"F0.wireOp",EDGE,"E29"),sQuery(id+"F0.wireOp",EDGE,"E30.trimOffspring"),sQuery(id+"F0.wireOp",EDGE,"E32"),sQuery(id+"F0.wireOp",EDGE,"E33.trimOffspring"),sQuery(id+"F0.wireOp",EDGE,"E34"),sQuery(id+"F0.wireOp",EDGE,"E35.trimOffspring")])],"isStart":true}),makeQuery(id+"F2.opExtrude","CAP_FACE",FACE,{"disambiguationData":[OSD([subQ3,subQ2,subQ1,subQ0])],"isStart":true})]})});}
            var Q9;
            {var subQ0=sQuery(id+"F0.wireOp",EDGE,"E24.right");var subQ1=sQuery(id+"F0.wireOp",EDGE,"E24.left");var subQ2=sQuery(id+"F0.wireOp",EDGE,"E24.top");var subQ3=sQuery(id+"F0.wireOp",EDGE,"E24.bottom");Q9=makeQuery(id+"F4.boolean.opBoolean","SPLIT",FACE,{"disambiguationData":[TD([makeQuery(id+"F4.opExtrude","SWEPT_FACE",FACE,{"disambiguationData":[OSD([sQuery(id+"F3.wireOp",EDGE,"E39.8.0.0")])]})])],"derivedFrom":makeQuery(id+"F2.boolean.opBoolean","MERGE",FACE,{"derivedFrom":[makeQuery(id+"F1.opExtrude","CAP_FACE",FACE,{"disambiguationData":[OSD([sQuery(id+"F0.wireOp",EDGE,"E1"),sQuery(id+"F0.wireOp",EDGE,"E2.bottom"),sQuery(id+"F0.wireOp",EDGE,"E2.top"),sQuery(id+"F0.wireOp",EDGE,"E3"),sQuery(id+"F0.wireOp",EDGE,"E7.MirrorC"),sQuery(id+"F0.wireOp",EDGE,"E8.MirrorC"),sQuery(id+"F0.wireOp",EDGE,"E9.MirrorCS"),sQuery(id+"F0.wireOp",EDGE,"E11.MirrorCS"),sQuery(id+"F0.wireOp",EDGE,"E12.MirrorC"),sQuery(id+"F0.wireOp",EDGE,"E13.MirrorC"),sQuery(id+"F0.wireOp",EDGE,"E14.MirrorCS"),sQuery(id+"F0.wireOp",EDGE,"E16.MirrorCS"),sQuery(id+"F0.wireOp",EDGE,"E17.MirrorCS"),sQuery(id+"F0.wireOp",EDGE,"E19.MirrorCS"),sQuery(id+"F0.wireOp",EDGE,"E20.MirrorC"),sQuery(id+"F0.wireOp",EDGE,"E21.MirrorC"),subQ3,subQ2,subQ1,subQ0,sQuery(id+"F0.wireOp",EDGE,"E25.bottom"),sQuery(id+"F0.wireOp",EDGE,"E25.top"),sQuery(id+"F0.wireOp",EDGE,"E25.left"),sQuery(id+"F0.wireOp",EDGE,"E25.right"),sQuery(id+"F0.wireOp",EDGE,"E26"),sQuery(id+"F0.wireOp",EDGE,"E27.trimOffspring"),sQuery(id+"F0.wireOp",EDGE,"E29"),sQuery(id+"F0.wireOp",EDGE,"E30.trimOffspring"),sQuery(id+"F0.wireOp",EDGE,"E32"),sQuery(id+"F0.wireOp",EDGE,"E33.trimOffspring"),sQuery(id+"F0.wireOp",EDGE,"E34"),sQuery(id+"F0.wireOp",EDGE,"E35.trimOffspring")])],"isStart":true}),makeQuery(id+"F2.opExtrude","CAP_FACE",FACE,{"disambiguationData":[OSD([subQ3,subQ2,subQ1,subQ0])],"isStart":true})]})});}
            var Q10;
            {var subQ0=sQuery(id+"F0.wireOp",EDGE,"E24.right");var subQ1=sQuery(id+"F0.wireOp",EDGE,"E24.left");var subQ2=sQuery(id+"F0.wireOp",EDGE,"E24.top");var subQ3=sQuery(id+"F0.wireOp",EDGE,"E24.bottom");Q10=makeQuery(id+"F4.boolean.opBoolean","SPLIT",FACE,{"disambiguationData":[TD([makeQuery(id+"F4.opExtrude","SWEPT_FACE",FACE,{"disambiguationData":[OSD([sQuery(id+"F3.wireOp",EDGE,"E39.10.0.0")])]})])],"derivedFrom":makeQuery(id+"F2.boolean.opBoolean","MERGE",FACE,{"derivedFrom":[makeQuery(id+"F1.opExtrude","CAP_FACE",FACE,{"disambiguationData":[OSD([sQuery(id+"F0.wireOp",EDGE,"E1"),sQuery(id+"F0.wireOp",EDGE,"E2.bottom"),sQuery(id+"F0.wireOp",EDGE,"E2.top"),sQuery(id+"F0.wireOp",EDGE,"E3"),sQuery(id+"F0.wireOp",EDGE,"E7.MirrorC"),sQuery(id+"F0.wireOp",EDGE,"E8.MirrorC"),sQuery(id+"F0.wireOp",EDGE,"E9.MirrorCS"),sQuery(id+"F0.wireOp",EDGE,"E11.MirrorCS"),sQuery(id+"F0.wireOp",EDGE,"E12.MirrorC"),sQuery(id+"F0.wireOp",EDGE,"E13.MirrorC"),sQuery(id+"F0.wireOp",EDGE,"E14.MirrorCS"),sQuery(id+"F0.wireOp",EDGE,"E16.MirrorCS"),sQuery(id+"F0.wireOp",EDGE,"E17.MirrorCS"),sQuery(id+"F0.wireOp",EDGE,"E19.MirrorCS"),sQuery(id+"F0.wireOp",EDGE,"E20.MirrorC"),sQuery(id+"F0.wireOp",EDGE,"E21.MirrorC"),subQ3,subQ2,subQ1,subQ0,sQuery(id+"F0.wireOp",EDGE,"E25.bottom"),sQuery(id+"F0.wireOp",EDGE,"E25.top"),sQuery(id+"F0.wireOp",EDGE,"E25.left"),sQuery(id+"F0.wireOp",EDGE,"E25.right"),sQuery(id+"F0.wireOp",EDGE,"E26"),sQuery(id+"F0.wireOp",EDGE,"E27.trimOffspring"),sQuery(id+"F0.wireOp",EDGE,"E29"),sQuery(id+"F0.wireOp",EDGE,"E30.trimOffspring"),sQuery(id+"F0.wireOp",EDGE,"E32"),sQuery(id+"F0.wireOp",EDGE,"E33.trimOffspring"),sQuery(id+"F0.wireOp",EDGE,"E34"),sQuery(id+"F0.wireOp",EDGE,"E35.trimOffspring")])],"isStart":true}),makeQuery(id+"F2.opExtrude","CAP_FACE",FACE,{"disambiguationData":[OSD([subQ3,subQ2,subQ1,subQ0])],"isStart":true})]})});}
            var Q11;
            {var subQ0=sQuery(id+"F0.wireOp",EDGE,"E24.right");var subQ1=sQuery(id+"F0.wireOp",EDGE,"E24.left");var subQ2=sQuery(id+"F0.wireOp",EDGE,"E24.top");var subQ3=sQuery(id+"F0.wireOp",EDGE,"E24.bottom");Q11=makeQuery(id+"F4.boolean.opBoolean","SPLIT",FACE,{"disambiguationData":[TD([makeQuery(id+"F4.opExtrude","SWEPT_FACE",FACE,{"disambiguationData":[OSD([sQuery(id+"F3.wireOp",EDGE,"E39.11.0.0")])]})])],"derivedFrom":makeQuery(id+"F2.boolean.opBoolean","MERGE",FACE,{"derivedFrom":[makeQuery(id+"F1.opExtrude","CAP_FACE",FACE,{"disambiguationData":[OSD([sQuery(id+"F0.wireOp",EDGE,"E1"),sQuery(id+"F0.wireOp",EDGE,"E2.bottom"),sQuery(id+"F0.wireOp",EDGE,"E2.top"),sQuery(id+"F0.wireOp",EDGE,"E3"),sQuery(id+"F0.wireOp",EDGE,"E7.MirrorC"),sQuery(id+"F0.wireOp",EDGE,"E8.MirrorC"),sQuery(id+"F0.wireOp",EDGE,"E9.MirrorCS"),sQuery(id+"F0.wireOp",EDGE,"E11.MirrorCS"),sQuery(id+"F0.wireOp",EDGE,"E12.MirrorC"),sQuery(id+"F0.wireOp",EDGE,"E13.MirrorC"),sQuery(id+"F0.wireOp",EDGE,"E14.MirrorCS"),sQuery(id+"F0.wireOp",EDGE,"E16.MirrorCS"),sQuery(id+"F0.wireOp",EDGE,"E17.MirrorCS"),sQuery(id+"F0.wireOp",EDGE,"E19.MirrorCS"),sQuery(id+"F0.wireOp",EDGE,"E20.MirrorC"),sQuery(id+"F0.wireOp",EDGE,"E21.MirrorC"),subQ3,subQ2,subQ1,subQ0,sQuery(id+"F0.wireOp",EDGE,"E25.bottom"),sQuery(id+"F0.wireOp",EDGE,"E25.top"),sQuery(id+"F0.wireOp",EDGE,"E25.left"),sQuery(id+"F0.wireOp",EDGE,"E25.right"),sQuery(id+"F0.wireOp",EDGE,"E26"),sQuery(id+"F0.wireOp",EDGE,"E27.trimOffspring"),sQuery(id+"F0.wireOp",EDGE,"E29"),sQuery(id+"F0.wireOp",EDGE,"E30.trimOffspring"),sQuery(id+"F0.wireOp",EDGE,"E32"),sQuery(id+"F0.wireOp",EDGE,"E33.trimOffspring"),sQuery(id+"F0.wireOp",EDGE,"E34"),sQuery(id+"F0.wireOp",EDGE,"E35.trimOffspring")])],"isStart":true}),makeQuery(id+"F2.opExtrude","CAP_FACE",FACE,{"disambiguationData":[OSD([subQ3,subQ2,subQ1,subQ0])],"isStart":true})]})});}
            var Q12;
            {var subQ0=sQuery(id+"F0.wireOp",EDGE,"E24.right");var subQ1=sQuery(id+"F0.wireOp",EDGE,"E24.left");var subQ2=sQuery(id+"F0.wireOp",EDGE,"E24.top");var subQ3=sQuery(id+"F0.wireOp",EDGE,"E24.bottom");Q12=makeQuery(id+"F4.boolean.opBoolean","SPLIT",FACE,{"disambiguationData":[TD([makeQuery(id+"F4.opExtrude","SWEPT_FACE",FACE,{"disambiguationData":[OSD([sQuery(id+"F3.wireOp",EDGE,"E39.12.0.0")])]})])],"derivedFrom":makeQuery(id+"F2.boolean.opBoolean","MERGE",FACE,{"derivedFrom":[makeQuery(id+"F1.opExtrude","CAP_FACE",FACE,{"disambiguationData":[OSD([sQuery(id+"F0.wireOp",EDGE,"E1"),sQuery(id+"F0.wireOp",EDGE,"E2.bottom"),sQuery(id+"F0.wireOp",EDGE,"E2.top"),sQuery(id+"F0.wireOp",EDGE,"E3"),sQuery(id+"F0.wireOp",EDGE,"E7.MirrorC"),sQuery(id+"F0.wireOp",EDGE,"E8.MirrorC"),sQuery(id+"F0.wireOp",EDGE,"E9.MirrorCS"),sQuery(id+"F0.wireOp",EDGE,"E11.MirrorCS"),sQuery(id+"F0.wireOp",EDGE,"E12.MirrorC"),sQuery(id+"F0.wireOp",EDGE,"E13.MirrorC"),sQuery(id+"F0.wireOp",EDGE,"E14.MirrorCS"),sQuery(id+"F0.wireOp",EDGE,"E16.MirrorCS"),sQuery(id+"F0.wireOp",EDGE,"E17.MirrorCS"),sQuery(id+"F0.wireOp",EDGE,"E19.MirrorCS"),sQuery(id+"F0.wireOp",EDGE,"E20.MirrorC"),sQuery(id+"F0.wireOp",EDGE,"E21.MirrorC"),subQ3,subQ2,subQ1,subQ0,sQuery(id+"F0.wireOp",EDGE,"E25.bottom"),sQuery(id+"F0.wireOp",EDGE,"E25.top"),sQuery(id+"F0.wireOp",EDGE,"E25.left"),sQuery(id+"F0.wireOp",EDGE,"E25.right"),sQuery(id+"F0.wireOp",EDGE,"E26"),sQuery(id+"F0.wireOp",EDGE,"E27.trimOffspring"),sQuery(id+"F0.wireOp",EDGE,"E29"),sQuery(id+"F0.wireOp",EDGE,"E30.trimOffspring"),sQuery(id+"F0.wireOp",EDGE,"E32"),sQuery(id+"F0.wireOp",EDGE,"E33.trimOffspring"),sQuery(id+"F0.wireOp",EDGE,"E34"),sQuery(id+"F0.wireOp",EDGE,"E35.trimOffspring")])],"isStart":true}),makeQuery(id+"F2.opExtrude","CAP_FACE",FACE,{"disambiguationData":[OSD([subQ3,subQ2,subQ1,subQ0])],"isStart":true})]})});}
            var Q13;
            {var subQ0=sQuery(id+"F0.wireOp",EDGE,"E24.right");var subQ1=sQuery(id+"F0.wireOp",EDGE,"E24.left");var subQ2=sQuery(id+"F0.wireOp",EDGE,"E24.top");var subQ3=sQuery(id+"F0.wireOp",EDGE,"E24.bottom");Q13=makeQuery(id+"F4.boolean.opBoolean","SPLIT",FACE,{"disambiguationData":[TD([makeQuery(id+"F4.opExtrude","SWEPT_FACE",FACE,{"disambiguationData":[OSD([sQuery(id+"F3.wireOp",EDGE,"E40.0.13.0")])]})])],"derivedFrom":makeQuery(id+"F2.boolean.opBoolean","MERGE",FACE,{"derivedFrom":[makeQuery(id+"F1.opExtrude","CAP_FACE",FACE,{"disambiguationData":[OSD([sQuery(id+"F0.wireOp",EDGE,"E1"),sQuery(id+"F0.wireOp",EDGE,"E2.bottom"),sQuery(id+"F0.wireOp",EDGE,"E2.top"),sQuery(id+"F0.wireOp",EDGE,"E3"),sQuery(id+"F0.wireOp",EDGE,"E7.MirrorC"),sQuery(id+"F0.wireOp",EDGE,"E8.MirrorC"),sQuery(id+"F0.wireOp",EDGE,"E9.MirrorCS"),sQuery(id+"F0.wireOp",EDGE,"E11.MirrorCS"),sQuery(id+"F0.wireOp",EDGE,"E12.MirrorC"),sQuery(id+"F0.wireOp",EDGE,"E13.MirrorC"),sQuery(id+"F0.wireOp",EDGE,"E14.MirrorCS"),sQuery(id+"F0.wireOp",EDGE,"E16.MirrorCS"),sQuery(id+"F0.wireOp",EDGE,"E17.MirrorCS"),sQuery(id+"F0.wireOp",EDGE,"E19.MirrorCS"),sQuery(id+"F0.wireOp",EDGE,"E20.MirrorC"),sQuery(id+"F0.wireOp",EDGE,"E21.MirrorC"),subQ3,subQ2,subQ1,subQ0,sQuery(id+"F0.wireOp",EDGE,"E25.bottom"),sQuery(id+"F0.wireOp",EDGE,"E25.top"),sQuery(id+"F0.wireOp",EDGE,"E25.left"),sQuery(id+"F0.wireOp",EDGE,"E25.right"),sQuery(id+"F0.wireOp",EDGE,"E26"),sQuery(id+"F0.wireOp",EDGE,"E27.trimOffspring"),sQuery(id+"F0.wireOp",EDGE,"E29"),sQuery(id+"F0.wireOp",EDGE,"E30.trimOffspring"),sQuery(id+"F0.wireOp",EDGE,"E32"),sQuery(id+"F0.wireOp",EDGE,"E33.trimOffspring"),sQuery(id+"F0.wireOp",EDGE,"E34"),sQuery(id+"F0.wireOp",EDGE,"E35.trimOffspring")])],"isStart":true}),makeQuery(id+"F2.opExtrude","CAP_FACE",FACE,{"disambiguationData":[OSD([subQ3,subQ2,subQ1,subQ0])],"isStart":true})]})});}
            var Q14;
            {var subQ0=sQuery(id+"F0.wireOp",EDGE,"E24.right");var subQ1=sQuery(id+"F0.wireOp",EDGE,"E24.left");var subQ2=sQuery(id+"F0.wireOp",EDGE,"E24.top");var subQ3=sQuery(id+"F0.wireOp",EDGE,"E24.bottom");Q14=makeQuery(id+"F4.boolean.opBoolean","SPLIT",FACE,{"disambiguationData":[TD([makeQuery(id+"F4.opExtrude","SWEPT_FACE",FACE,{"disambiguationData":[OSD([sQuery(id+"F3.wireOp",EDGE,"E41.1.0.4")])]})])],"derivedFrom":makeQuery(id+"F2.boolean.opBoolean","MERGE",FACE,{"derivedFrom":[makeQuery(id+"F1.opExtrude","CAP_FACE",FACE,{"disambiguationData":[OSD([sQuery(id+"F0.wireOp",EDGE,"E1"),sQuery(id+"F0.wireOp",EDGE,"E2.bottom"),sQuery(id+"F0.wireOp",EDGE,"E2.top"),sQuery(id+"F0.wireOp",EDGE,"E3"),sQuery(id+"F0.wireOp",EDGE,"E7.MirrorC"),sQuery(id+"F0.wireOp",EDGE,"E8.MirrorC"),sQuery(id+"F0.wireOp",EDGE,"E9.MirrorCS"),sQuery(id+"F0.wireOp",EDGE,"E11.MirrorCS"),sQuery(id+"F0.wireOp",EDGE,"E12.MirrorC"),sQuery(id+"F0.wireOp",EDGE,"E13.MirrorC"),sQuery(id+"F0.wireOp",EDGE,"E14.MirrorCS"),sQuery(id+"F0.wireOp",EDGE,"E16.MirrorCS"),sQuery(id+"F0.wireOp",EDGE,"E17.MirrorCS"),sQuery(id+"F0.wireOp",EDGE,"E19.MirrorCS"),sQuery(id+"F0.wireOp",EDGE,"E20.MirrorC"),sQuery(id+"F0.wireOp",EDGE,"E21.MirrorC"),subQ3,subQ2,subQ1,subQ0,sQuery(id+"F0.wireOp",EDGE,"E25.bottom"),sQuery(id+"F0.wireOp",EDGE,"E25.top"),sQuery(id+"F0.wireOp",EDGE,"E25.left"),sQuery(id+"F0.wireOp",EDGE,"E25.right"),sQuery(id+"F0.wireOp",EDGE,"E26"),sQuery(id+"F0.wireOp",EDGE,"E27.trimOffspring"),sQuery(id+"F0.wireOp",EDGE,"E29"),sQuery(id+"F0.wireOp",EDGE,"E30.trimOffspring"),sQuery(id+"F0.wireOp",EDGE,"E32"),sQuery(id+"F0.wireOp",EDGE,"E33.trimOffspring"),sQuery(id+"F0.wireOp",EDGE,"E34"),sQuery(id+"F0.wireOp",EDGE,"E35.trimOffspring")])],"isStart":true}),makeQuery(id+"F2.opExtrude","CAP_FACE",FACE,{"disambiguationData":[OSD([subQ3,subQ2,subQ1,subQ0])],"isStart":true})]})});}
            var Q15;
            {var subQ0=sQuery(id+"F0.wireOp",EDGE,"E24.right");var subQ1=sQuery(id+"F0.wireOp",EDGE,"E24.left");var subQ2=sQuery(id+"F0.wireOp",EDGE,"E24.top");var subQ3=sQuery(id+"F0.wireOp",EDGE,"E24.bottom");Q15=makeQuery(id+"F4.boolean.opBoolean","SPLIT",FACE,{"disambiguationData":[TD([makeQuery(id+"F4.opExtrude","SWEPT_FACE",FACE,{"disambiguationData":[OSD([sQuery(id+"F3.wireOp",EDGE,"E41.1.0.5")])]})])],"derivedFrom":makeQuery(id+"F2.boolean.opBoolean","MERGE",FACE,{"derivedFrom":[makeQuery(id+"F1.opExtrude","CAP_FACE",FACE,{"disambiguationData":[OSD([sQuery(id+"F0.wireOp",EDGE,"E1"),sQuery(id+"F0.wireOp",EDGE,"E2.bottom"),sQuery(id+"F0.wireOp",EDGE,"E2.top"),sQuery(id+"F0.wireOp",EDGE,"E3"),sQuery(id+"F0.wireOp",EDGE,"E7.MirrorC"),sQuery(id+"F0.wireOp",EDGE,"E8.MirrorC"),sQuery(id+"F0.wireOp",EDGE,"E9.MirrorCS"),sQuery(id+"F0.wireOp",EDGE,"E11.MirrorCS"),sQuery(id+"F0.wireOp",EDGE,"E12.MirrorC"),sQuery(id+"F0.wireOp",EDGE,"E13.MirrorC"),sQuery(id+"F0.wireOp",EDGE,"E14.MirrorCS"),sQuery(id+"F0.wireOp",EDGE,"E16.MirrorCS"),sQuery(id+"F0.wireOp",EDGE,"E17.MirrorCS"),sQuery(id+"F0.wireOp",EDGE,"E19.MirrorCS"),sQuery(id+"F0.wireOp",EDGE,"E20.MirrorC"),sQuery(id+"F0.wireOp",EDGE,"E21.MirrorC"),subQ3,subQ2,subQ1,subQ0,sQuery(id+"F0.wireOp",EDGE,"E25.bottom"),sQuery(id+"F0.wireOp",EDGE,"E25.top"),sQuery(id+"F0.wireOp",EDGE,"E25.left"),sQuery(id+"F0.wireOp",EDGE,"E25.right"),sQuery(id+"F0.wireOp",EDGE,"E26"),sQuery(id+"F0.wireOp",EDGE,"E27.trimOffspring"),sQuery(id+"F0.wireOp",EDGE,"E29"),sQuery(id+"F0.wireOp",EDGE,"E30.trimOffspring"),sQuery(id+"F0.wireOp",EDGE,"E32"),sQuery(id+"F0.wireOp",EDGE,"E33.trimOffspring"),sQuery(id+"F0.wireOp",EDGE,"E34"),sQuery(id+"F0.wireOp",EDGE,"E35.trimOffspring")])],"isStart":true}),makeQuery(id+"F2.opExtrude","CAP_FACE",FACE,{"disambiguationData":[OSD([subQ3,subQ2,subQ1,subQ0])],"isStart":true})]})});}
            var Q16;
            {var subQ0=sQuery(id+"F0.wireOp",EDGE,"E24.right");var subQ1=sQuery(id+"F0.wireOp",EDGE,"E24.left");var subQ2=sQuery(id+"F0.wireOp",EDGE,"E24.top");var subQ3=sQuery(id+"F0.wireOp",EDGE,"E24.bottom");Q16=makeQuery(id+"F4.boolean.opBoolean","SPLIT",FACE,{"disambiguationData":[TD([makeQuery(id+"F4.opExtrude","SWEPT_FACE",FACE,{"disambiguationData":[OSD([sQuery(id+"F3.wireOp",EDGE,"E41.1.0.14")])]})])],"derivedFrom":makeQuery(id+"F2.boolean.opBoolean","MERGE",FACE,{"derivedFrom":[makeQuery(id+"F1.opExtrude","CAP_FACE",FACE,{"disambiguationData":[OSD([sQuery(id+"F0.wireOp",EDGE,"E1"),sQuery(id+"F0.wireOp",EDGE,"E2.bottom"),sQuery(id+"F0.wireOp",EDGE,"E2.top"),sQuery(id+"F0.wireOp",EDGE,"E3"),sQuery(id+"F0.wireOp",EDGE,"E7.MirrorC"),sQuery(id+"F0.wireOp",EDGE,"E8.MirrorC"),sQuery(id+"F0.wireOp",EDGE,"E9.MirrorCS"),sQuery(id+"F0.wireOp",EDGE,"E11.MirrorCS"),sQuery(id+"F0.wireOp",EDGE,"E12.MirrorC"),sQuery(id+"F0.wireOp",EDGE,"E13.MirrorC"),sQuery(id+"F0.wireOp",EDGE,"E14.MirrorCS"),sQuery(id+"F0.wireOp",EDGE,"E16.MirrorCS"),sQuery(id+"F0.wireOp",EDGE,"E17.MirrorCS"),sQuery(id+"F0.wireOp",EDGE,"E19.MirrorCS"),sQuery(id+"F0.wireOp",EDGE,"E20.MirrorC"),sQuery(id+"F0.wireOp",EDGE,"E21.MirrorC"),subQ3,subQ2,subQ1,subQ0,sQuery(id+"F0.wireOp",EDGE,"E25.bottom"),sQuery(id+"F0.wireOp",EDGE,"E25.top"),sQuery(id+"F0.wireOp",EDGE,"E25.left"),sQuery(id+"F0.wireOp",EDGE,"E25.right"),sQuery(id+"F0.wireOp",EDGE,"E26"),sQuery(id+"F0.wireOp",EDGE,"E27.trimOffspring"),sQuery(id+"F0.wireOp",EDGE,"E29"),sQuery(id+"F0.wireOp",EDGE,"E30.trimOffspring"),sQuery(id+"F0.wireOp",EDGE,"E32"),sQuery(id+"F0.wireOp",EDGE,"E33.trimOffspring"),sQuery(id+"F0.wireOp",EDGE,"E34"),sQuery(id+"F0.wireOp",EDGE,"E35.trimOffspring")])],"isStart":true}),makeQuery(id+"F2.opExtrude","CAP_FACE",FACE,{"disambiguationData":[OSD([subQ3,subQ2,subQ1,subQ0])],"isStart":true})]})});}
            var Q17;
            {var subQ0=sQuery(id+"F0.wireOp",EDGE,"E24.right");var subQ1=sQuery(id+"F0.wireOp",EDGE,"E24.left");var subQ2=sQuery(id+"F0.wireOp",EDGE,"E24.top");var subQ3=sQuery(id+"F0.wireOp",EDGE,"E24.bottom");Q17=makeQuery(id+"F4.boolean.opBoolean","SPLIT",FACE,{"disambiguationData":[TD([makeQuery(id+"F4.opExtrude","SWEPT_FACE",FACE,{"disambiguationData":[OSD([sQuery(id+"F3.wireOp",EDGE,"E41.1.0.3")])]})])],"derivedFrom":makeQuery(id+"F2.boolean.opBoolean","MERGE",FACE,{"derivedFrom":[makeQuery(id+"F1.opExtrude","CAP_FACE",FACE,{"disambiguationData":[OSD([sQuery(id+"F0.wireOp",EDGE,"E1"),sQuery(id+"F0.wireOp",EDGE,"E2.bottom"),sQuery(id+"F0.wireOp",EDGE,"E2.top"),sQuery(id+"F0.wireOp",EDGE,"E3"),sQuery(id+"F0.wireOp",EDGE,"E7.MirrorC"),sQuery(id+"F0.wireOp",EDGE,"E8.MirrorC"),sQuery(id+"F0.wireOp",EDGE,"E9.MirrorCS"),sQuery(id+"F0.wireOp",EDGE,"E11.MirrorCS"),sQuery(id+"F0.wireOp",EDGE,"E12.MirrorC"),sQuery(id+"F0.wireOp",EDGE,"E13.MirrorC"),sQuery(id+"F0.wireOp",EDGE,"E14.MirrorCS"),sQuery(id+"F0.wireOp",EDGE,"E16.MirrorCS"),sQuery(id+"F0.wireOp",EDGE,"E17.MirrorCS"),sQuery(id+"F0.wireOp",EDGE,"E19.MirrorCS"),sQuery(id+"F0.wireOp",EDGE,"E20.MirrorC"),sQuery(id+"F0.wireOp",EDGE,"E21.MirrorC"),subQ3,subQ2,subQ1,subQ0,sQuery(id+"F0.wireOp",EDGE,"E25.bottom"),sQuery(id+"F0.wireOp",EDGE,"E25.top"),sQuery(id+"F0.wireOp",EDGE,"E25.left"),sQuery(id+"F0.wireOp",EDGE,"E25.right"),sQuery(id+"F0.wireOp",EDGE,"E26"),sQuery(id+"F0.wireOp",EDGE,"E27.trimOffspring"),sQuery(id+"F0.wireOp",EDGE,"E29"),sQuery(id+"F0.wireOp",EDGE,"E30.trimOffspring"),sQuery(id+"F0.wireOp",EDGE,"E32"),sQuery(id+"F0.wireOp",EDGE,"E33.trimOffspring"),sQuery(id+"F0.wireOp",EDGE,"E34"),sQuery(id+"F0.wireOp",EDGE,"E35.trimOffspring")])],"isStart":true}),makeQuery(id+"F2.opExtrude","CAP_FACE",FACE,{"disambiguationData":[OSD([subQ3,subQ2,subQ1,subQ0])],"isStart":true})]})});}
            var Q18;
            {var subQ0=sQuery(id+"F0.wireOp",EDGE,"E24.right");var subQ1=sQuery(id+"F0.wireOp",EDGE,"E24.left");var subQ2=sQuery(id+"F0.wireOp",EDGE,"E24.top");var subQ3=sQuery(id+"F0.wireOp",EDGE,"E24.bottom");Q18=makeQuery(id+"F4.boolean.opBoolean","SPLIT",FACE,{"disambiguationData":[TD([makeQuery(id+"F4.opExtrude","SWEPT_FACE",FACE,{"disambiguationData":[OSD([sQuery(id+"F3.wireOp",EDGE,"E41.1.0.12")])]})])],"derivedFrom":makeQuery(id+"F2.boolean.opBoolean","MERGE",FACE,{"derivedFrom":[makeQuery(id+"F1.opExtrude","CAP_FACE",FACE,{"disambiguationData":[OSD([sQuery(id+"F0.wireOp",EDGE,"E1"),sQuery(id+"F0.wireOp",EDGE,"E2.bottom"),sQuery(id+"F0.wireOp",EDGE,"E2.top"),sQuery(id+"F0.wireOp",EDGE,"E3"),sQuery(id+"F0.wireOp",EDGE,"E7.MirrorC"),sQuery(id+"F0.wireOp",EDGE,"E8.MirrorC"),sQuery(id+"F0.wireOp",EDGE,"E9.MirrorCS"),sQuery(id+"F0.wireOp",EDGE,"E11.MirrorCS"),sQuery(id+"F0.wireOp",EDGE,"E12.MirrorC"),sQuery(id+"F0.wireOp",EDGE,"E13.MirrorC"),sQuery(id+"F0.wireOp",EDGE,"E14.MirrorCS"),sQuery(id+"F0.wireOp",EDGE,"E16.MirrorCS"),sQuery(id+"F0.wireOp",EDGE,"E17.MirrorCS"),sQuery(id+"F0.wireOp",EDGE,"E19.MirrorCS"),sQuery(id+"F0.wireOp",EDGE,"E20.MirrorC"),sQuery(id+"F0.wireOp",EDGE,"E21.MirrorC"),subQ3,subQ2,subQ1,subQ0,sQuery(id+"F0.wireOp",EDGE,"E25.bottom"),sQuery(id+"F0.wireOp",EDGE,"E25.top"),sQuery(id+"F0.wireOp",EDGE,"E25.left"),sQuery(id+"F0.wireOp",EDGE,"E25.right"),sQuery(id+"F0.wireOp",EDGE,"E26"),sQuery(id+"F0.wireOp",EDGE,"E27.trimOffspring"),sQuery(id+"F0.wireOp",EDGE,"E29"),sQuery(id+"F0.wireOp",EDGE,"E30.trimOffspring"),sQuery(id+"F0.wireOp",EDGE,"E32"),sQuery(id+"F0.wireOp",EDGE,"E33.trimOffspring"),sQuery(id+"F0.wireOp",EDGE,"E34"),sQuery(id+"F0.wireOp",EDGE,"E35.trimOffspring")])],"isStart":true}),makeQuery(id+"F2.opExtrude","CAP_FACE",FACE,{"disambiguationData":[OSD([subQ3,subQ2,subQ1,subQ0])],"isStart":true})]})});}
            var Q19;
            {var subQ0=sQuery(id+"F0.wireOp",EDGE,"E24.right");var subQ1=sQuery(id+"F0.wireOp",EDGE,"E24.left");var subQ2=sQuery(id+"F0.wireOp",EDGE,"E24.top");var subQ3=sQuery(id+"F0.wireOp",EDGE,"E24.bottom");Q19=makeQuery(id+"F4.boolean.opBoolean","SPLIT",FACE,{"disambiguationData":[TD([makeQuery(id+"F4.opExtrude","SWEPT_FACE",FACE,{"disambiguationData":[OSD([sQuery(id+"F3.wireOp",EDGE,"E41.1.0.6")])]})])],"derivedFrom":makeQuery(id+"F2.boolean.opBoolean","MERGE",FACE,{"derivedFrom":[makeQuery(id+"F1.opExtrude","CAP_FACE",FACE,{"disambiguationData":[OSD([sQuery(id+"F0.wireOp",EDGE,"E1"),sQuery(id+"F0.wireOp",EDGE,"E2.bottom"),sQuery(id+"F0.wireOp",EDGE,"E2.top"),sQuery(id+"F0.wireOp",EDGE,"E3"),sQuery(id+"F0.wireOp",EDGE,"E7.MirrorC"),sQuery(id+"F0.wireOp",EDGE,"E8.MirrorC"),sQuery(id+"F0.wireOp",EDGE,"E9.MirrorCS"),sQuery(id+"F0.wireOp",EDGE,"E11.MirrorCS"),sQuery(id+"F0.wireOp",EDGE,"E12.MirrorC"),sQuery(id+"F0.wireOp",EDGE,"E13.MirrorC"),sQuery(id+"F0.wireOp",EDGE,"E14.MirrorCS"),sQuery(id+"F0.wireOp",EDGE,"E16.MirrorCS"),sQuery(id+"F0.wireOp",EDGE,"E17.MirrorCS"),sQuery(id+"F0.wireOp",EDGE,"E19.MirrorCS"),sQuery(id+"F0.wireOp",EDGE,"E20.MirrorC"),sQuery(id+"F0.wireOp",EDGE,"E21.MirrorC"),subQ3,subQ2,subQ1,subQ0,sQuery(id+"F0.wireOp",EDGE,"E25.bottom"),sQuery(id+"F0.wireOp",EDGE,"E25.top"),sQuery(id+"F0.wireOp",EDGE,"E25.left"),sQuery(id+"F0.wireOp",EDGE,"E25.right"),sQuery(id+"F0.wireOp",EDGE,"E26"),sQuery(id+"F0.wireOp",EDGE,"E27.trimOffspring"),sQuery(id+"F0.wireOp",EDGE,"E29"),sQuery(id+"F0.wireOp",EDGE,"E30.trimOffspring"),sQuery(id+"F0.wireOp",EDGE,"E32"),sQuery(id+"F0.wireOp",EDGE,"E33.trimOffspring"),sQuery(id+"F0.wireOp",EDGE,"E34"),sQuery(id+"F0.wireOp",EDGE,"E35.trimOffspring")])],"isStart":true}),makeQuery(id+"F2.opExtrude","CAP_FACE",FACE,{"disambiguationData":[OSD([subQ3,subQ2,subQ1,subQ0])],"isStart":true})]})});}
            var Q20;
            {var subQ0=sQuery(id+"F0.wireOp",EDGE,"E24.right");var subQ1=sQuery(id+"F0.wireOp",EDGE,"E24.left");var subQ2=sQuery(id+"F0.wireOp",EDGE,"E24.top");var subQ3=sQuery(id+"F0.wireOp",EDGE,"E24.bottom");Q20=makeQuery(id+"F4.boolean.opBoolean","SPLIT",FACE,{"disambiguationData":[TD([makeQuery(id+"F4.opExtrude","SWEPT_FACE",FACE,{"disambiguationData":[OSD([sQuery(id+"F3.wireOp",EDGE,"E41.1.0.2")])]})])],"derivedFrom":makeQuery(id+"F2.boolean.opBoolean","MERGE",FACE,{"derivedFrom":[makeQuery(id+"F1.opExtrude","CAP_FACE",FACE,{"disambiguationData":[OSD([sQuery(id+"F0.wireOp",EDGE,"E1"),sQuery(id+"F0.wireOp",EDGE,"E2.bottom"),sQuery(id+"F0.wireOp",EDGE,"E2.top"),sQuery(id+"F0.wireOp",EDGE,"E3"),sQuery(id+"F0.wireOp",EDGE,"E7.MirrorC"),sQuery(id+"F0.wireOp",EDGE,"E8.MirrorC"),sQuery(id+"F0.wireOp",EDGE,"E9.MirrorCS"),sQuery(id+"F0.wireOp",EDGE,"E11.MirrorCS"),sQuery(id+"F0.wireOp",EDGE,"E12.MirrorC"),sQuery(id+"F0.wireOp",EDGE,"E13.MirrorC"),sQuery(id+"F0.wireOp",EDGE,"E14.MirrorCS"),sQuery(id+"F0.wireOp",EDGE,"E16.MirrorCS"),sQuery(id+"F0.wireOp",EDGE,"E17.MirrorCS"),sQuery(id+"F0.wireOp",EDGE,"E19.MirrorCS"),sQuery(id+"F0.wireOp",EDGE,"E20.MirrorC"),sQuery(id+"F0.wireOp",EDGE,"E21.MirrorC"),subQ3,subQ2,subQ1,subQ0,sQuery(id+"F0.wireOp",EDGE,"E25.bottom"),sQuery(id+"F0.wireOp",EDGE,"E25.top"),sQuery(id+"F0.wireOp",EDGE,"E25.left"),sQuery(id+"F0.wireOp",EDGE,"E25.right"),sQuery(id+"F0.wireOp",EDGE,"E26"),sQuery(id+"F0.wireOp",EDGE,"E27.trimOffspring"),sQuery(id+"F0.wireOp",EDGE,"E29"),sQuery(id+"F0.wireOp",EDGE,"E30.trimOffspring"),sQuery(id+"F0.wireOp",EDGE,"E32"),sQuery(id+"F0.wireOp",EDGE,"E33.trimOffspring"),sQuery(id+"F0.wireOp",EDGE,"E34"),sQuery(id+"F0.wireOp",EDGE,"E35.trimOffspring")])],"isStart":true}),makeQuery(id+"F2.opExtrude","CAP_FACE",FACE,{"disambiguationData":[OSD([subQ3,subQ2,subQ1,subQ0])],"isStart":true})]})});}
            var Q21;
            {var subQ0=sQuery(id+"F0.wireOp",EDGE,"E24.right");var subQ1=sQuery(id+"F0.wireOp",EDGE,"E24.left");var subQ2=sQuery(id+"F0.wireOp",EDGE,"E24.top");var subQ3=sQuery(id+"F0.wireOp",EDGE,"E24.bottom");Q21=makeQuery(id+"F4.boolean.opBoolean","SPLIT",FACE,{"disambiguationData":[TD([makeQuery(id+"F4.opExtrude","SWEPT_FACE",FACE,{"disambiguationData":[OSD([sQuery(id+"F3.wireOp",EDGE,"E41.1.0.11")])]})])],"derivedFrom":makeQuery(id+"F2.boolean.opBoolean","MERGE",FACE,{"derivedFrom":[makeQuery(id+"F1.opExtrude","CAP_FACE",FACE,{"disambiguationData":[OSD([sQuery(id+"F0.wireOp",EDGE,"E1"),sQuery(id+"F0.wireOp",EDGE,"E2.bottom"),sQuery(id+"F0.wireOp",EDGE,"E2.top"),sQuery(id+"F0.wireOp",EDGE,"E3"),sQuery(id+"F0.wireOp",EDGE,"E7.MirrorC"),sQuery(id+"F0.wireOp",EDGE,"E8.MirrorC"),sQuery(id+"F0.wireOp",EDGE,"E9.MirrorCS"),sQuery(id+"F0.wireOp",EDGE,"E11.MirrorCS"),sQuery(id+"F0.wireOp",EDGE,"E12.MirrorC"),sQuery(id+"F0.wireOp",EDGE,"E13.MirrorC"),sQuery(id+"F0.wireOp",EDGE,"E14.MirrorCS"),sQuery(id+"F0.wireOp",EDGE,"E16.MirrorCS"),sQuery(id+"F0.wireOp",EDGE,"E17.MirrorCS"),sQuery(id+"F0.wireOp",EDGE,"E19.MirrorCS"),sQuery(id+"F0.wireOp",EDGE,"E20.MirrorC"),sQuery(id+"F0.wireOp",EDGE,"E21.MirrorC"),subQ3,subQ2,subQ1,subQ0,sQuery(id+"F0.wireOp",EDGE,"E25.bottom"),sQuery(id+"F0.wireOp",EDGE,"E25.top"),sQuery(id+"F0.wireOp",EDGE,"E25.left"),sQuery(id+"F0.wireOp",EDGE,"E25.right"),sQuery(id+"F0.wireOp",EDGE,"E26"),sQuery(id+"F0.wireOp",EDGE,"E27.trimOffspring"),sQuery(id+"F0.wireOp",EDGE,"E29"),sQuery(id+"F0.wireOp",EDGE,"E30.trimOffspring"),sQuery(id+"F0.wireOp",EDGE,"E32"),sQuery(id+"F0.wireOp",EDGE,"E33.trimOffspring"),sQuery(id+"F0.wireOp",EDGE,"E34"),sQuery(id+"F0.wireOp",EDGE,"E35.trimOffspring")])],"isStart":true}),makeQuery(id+"F2.opExtrude","CAP_FACE",FACE,{"disambiguationData":[OSD([subQ3,subQ2,subQ1,subQ0])],"isStart":true})]})});}
            var Q22;
            {var subQ0=sQuery(id+"F0.wireOp",EDGE,"E24.right");var subQ1=sQuery(id+"F0.wireOp",EDGE,"E24.left");var subQ2=sQuery(id+"F0.wireOp",EDGE,"E24.top");var subQ3=sQuery(id+"F0.wireOp",EDGE,"E24.bottom");Q22=makeQuery(id+"F4.boolean.opBoolean","SPLIT",FACE,{"disambiguationData":[TD([makeQuery(id+"F4.opExtrude","SWEPT_FACE",FACE,{"disambiguationData":[OSD([sQuery(id+"F3.wireOp",EDGE,"E41.1.0.0")])]})])],"derivedFrom":makeQuery(id+"F2.boolean.opBoolean","MERGE",FACE,{"derivedFrom":[makeQuery(id+"F1.opExtrude","CAP_FACE",FACE,{"disambiguationData":[OSD([sQuery(id+"F0.wireOp",EDGE,"E1"),sQuery(id+"F0.wireOp",EDGE,"E2.bottom"),sQuery(id+"F0.wireOp",EDGE,"E2.top"),sQuery(id+"F0.wireOp",EDGE,"E3"),sQuery(id+"F0.wireOp",EDGE,"E7.MirrorC"),sQuery(id+"F0.wireOp",EDGE,"E8.MirrorC"),sQuery(id+"F0.wireOp",EDGE,"E9.MirrorCS"),sQuery(id+"F0.wireOp",EDGE,"E11.MirrorCS"),sQuery(id+"F0.wireOp",EDGE,"E12.MirrorC"),sQuery(id+"F0.wireOp",EDGE,"E13.MirrorC"),sQuery(id+"F0.wireOp",EDGE,"E14.MirrorCS"),sQuery(id+"F0.wireOp",EDGE,"E16.MirrorCS"),sQuery(id+"F0.wireOp",EDGE,"E17.MirrorCS"),sQuery(id+"F0.wireOp",EDGE,"E19.MirrorCS"),sQuery(id+"F0.wireOp",EDGE,"E20.MirrorC"),sQuery(id+"F0.wireOp",EDGE,"E21.MirrorC"),subQ3,subQ2,subQ1,subQ0,sQuery(id+"F0.wireOp",EDGE,"E25.bottom"),sQuery(id+"F0.wireOp",EDGE,"E25.top"),sQuery(id+"F0.wireOp",EDGE,"E25.left"),sQuery(id+"F0.wireOp",EDGE,"E25.right"),sQuery(id+"F0.wireOp",EDGE,"E26"),sQuery(id+"F0.wireOp",EDGE,"E27.trimOffspring"),sQuery(id+"F0.wireOp",EDGE,"E29"),sQuery(id+"F0.wireOp",EDGE,"E30.trimOffspring"),sQuery(id+"F0.wireOp",EDGE,"E32"),sQuery(id+"F0.wireOp",EDGE,"E33.trimOffspring"),sQuery(id+"F0.wireOp",EDGE,"E34"),sQuery(id+"F0.wireOp",EDGE,"E35.trimOffspring")])],"isStart":true}),makeQuery(id+"F2.opExtrude","CAP_FACE",FACE,{"disambiguationData":[OSD([subQ3,subQ2,subQ1,subQ0])],"isStart":true})]})});}
            var Q23;
            {var subQ0=sQuery(id+"F0.wireOp",EDGE,"E24.right");var subQ1=sQuery(id+"F0.wireOp",EDGE,"E24.left");var subQ2=sQuery(id+"F0.wireOp",EDGE,"E24.top");var subQ3=sQuery(id+"F0.wireOp",EDGE,"E24.bottom");Q23=makeQuery(id+"F4.boolean.opBoolean","SPLIT",FACE,{"disambiguationData":[TD([makeQuery(id+"F4.opExtrude","SWEPT_FACE",FACE,{"disambiguationData":[OSD([sQuery(id+"F3.wireOp",EDGE,"E41.1.0.7")])]})])],"derivedFrom":makeQuery(id+"F2.boolean.opBoolean","MERGE",FACE,{"derivedFrom":[makeQuery(id+"F1.opExtrude","CAP_FACE",FACE,{"disambiguationData":[OSD([sQuery(id+"F0.wireOp",EDGE,"E1"),sQuery(id+"F0.wireOp",EDGE,"E2.bottom"),sQuery(id+"F0.wireOp",EDGE,"E2.top"),sQuery(id+"F0.wireOp",EDGE,"E3"),sQuery(id+"F0.wireOp",EDGE,"E7.MirrorC"),sQuery(id+"F0.wireOp",EDGE,"E8.MirrorC"),sQuery(id+"F0.wireOp",EDGE,"E9.MirrorCS"),sQuery(id+"F0.wireOp",EDGE,"E11.MirrorCS"),sQuery(id+"F0.wireOp",EDGE,"E12.MirrorC"),sQuery(id+"F0.wireOp",EDGE,"E13.MirrorC"),sQuery(id+"F0.wireOp",EDGE,"E14.MirrorCS"),sQuery(id+"F0.wireOp",EDGE,"E16.MirrorCS"),sQuery(id+"F0.wireOp",EDGE,"E17.MirrorCS"),sQuery(id+"F0.wireOp",EDGE,"E19.MirrorCS"),sQuery(id+"F0.wireOp",EDGE,"E20.MirrorC"),sQuery(id+"F0.wireOp",EDGE,"E21.MirrorC"),subQ3,subQ2,subQ1,subQ0,sQuery(id+"F0.wireOp",EDGE,"E25.bottom"),sQuery(id+"F0.wireOp",EDGE,"E25.top"),sQuery(id+"F0.wireOp",EDGE,"E25.left"),sQuery(id+"F0.wireOp",EDGE,"E25.right"),sQuery(id+"F0.wireOp",EDGE,"E26"),sQuery(id+"F0.wireOp",EDGE,"E27.trimOffspring"),sQuery(id+"F0.wireOp",EDGE,"E29"),sQuery(id+"F0.wireOp",EDGE,"E30.trimOffspring"),sQuery(id+"F0.wireOp",EDGE,"E32"),sQuery(id+"F0.wireOp",EDGE,"E33.trimOffspring"),sQuery(id+"F0.wireOp",EDGE,"E34"),sQuery(id+"F0.wireOp",EDGE,"E35.trimOffspring")])],"isStart":true}),makeQuery(id+"F2.opExtrude","CAP_FACE",FACE,{"disambiguationData":[OSD([subQ3,subQ2,subQ1,subQ0])],"isStart":true})]})});}
            var Q24;
            {var subQ0=sQuery(id+"F0.wireOp",EDGE,"E24.right");var subQ1=sQuery(id+"F0.wireOp",EDGE,"E24.left");var subQ2=sQuery(id+"F0.wireOp",EDGE,"E24.top");var subQ3=sQuery(id+"F0.wireOp",EDGE,"E24.bottom");Q24=makeQuery(id+"F4.boolean.opBoolean","SPLIT",FACE,{"disambiguationData":[TD([makeQuery(id+"F4.opExtrude","SWEPT_FACE",FACE,{"disambiguationData":[OSD([sQuery(id+"F3.wireOp",EDGE,"E41.1.0.8")])]})])],"derivedFrom":makeQuery(id+"F2.boolean.opBoolean","MERGE",FACE,{"derivedFrom":[makeQuery(id+"F1.opExtrude","CAP_FACE",FACE,{"disambiguationData":[OSD([sQuery(id+"F0.wireOp",EDGE,"E1"),sQuery(id+"F0.wireOp",EDGE,"E2.bottom"),sQuery(id+"F0.wireOp",EDGE,"E2.top"),sQuery(id+"F0.wireOp",EDGE,"E3"),sQuery(id+"F0.wireOp",EDGE,"E7.MirrorC"),sQuery(id+"F0.wireOp",EDGE,"E8.MirrorC"),sQuery(id+"F0.wireOp",EDGE,"E9.MirrorCS"),sQuery(id+"F0.wireOp",EDGE,"E11.MirrorCS"),sQuery(id+"F0.wireOp",EDGE,"E12.MirrorC"),sQuery(id+"F0.wireOp",EDGE,"E13.MirrorC"),sQuery(id+"F0.wireOp",EDGE,"E14.MirrorCS"),sQuery(id+"F0.wireOp",EDGE,"E16.MirrorCS"),sQuery(id+"F0.wireOp",EDGE,"E17.MirrorCS"),sQuery(id+"F0.wireOp",EDGE,"E19.MirrorCS"),sQuery(id+"F0.wireOp",EDGE,"E20.MirrorC"),sQuery(id+"F0.wireOp",EDGE,"E21.MirrorC"),subQ3,subQ2,subQ1,subQ0,sQuery(id+"F0.wireOp",EDGE,"E25.bottom"),sQuery(id+"F0.wireOp",EDGE,"E25.top"),sQuery(id+"F0.wireOp",EDGE,"E25.left"),sQuery(id+"F0.wireOp",EDGE,"E25.right"),sQuery(id+"F0.wireOp",EDGE,"E26"),sQuery(id+"F0.wireOp",EDGE,"E27.trimOffspring"),sQuery(id+"F0.wireOp",EDGE,"E29"),sQuery(id+"F0.wireOp",EDGE,"E30.trimOffspring"),sQuery(id+"F0.wireOp",EDGE,"E32"),sQuery(id+"F0.wireOp",EDGE,"E33.trimOffspring"),sQuery(id+"F0.wireOp",EDGE,"E34"),sQuery(id+"F0.wireOp",EDGE,"E35.trimOffspring")])],"isStart":true}),makeQuery(id+"F2.opExtrude","CAP_FACE",FACE,{"disambiguationData":[OSD([subQ3,subQ2,subQ1,subQ0])],"isStart":true})]})});}
            var Q25;
            {var subQ0=sQuery(id+"F0.wireOp",EDGE,"E24.right");var subQ1=sQuery(id+"F0.wireOp",EDGE,"E24.left");var subQ2=sQuery(id+"F0.wireOp",EDGE,"E24.top");var subQ3=sQuery(id+"F0.wireOp",EDGE,"E24.bottom");Q25=makeQuery(id+"F4.boolean.opBoolean","SPLIT",FACE,{"disambiguationData":[TD([makeQuery(id+"F4.opExtrude","SWEPT_FACE",FACE,{"disambiguationData":[OSD([sQuery(id+"F3.wireOp",EDGE,"E41.1.0.9")])]})])],"derivedFrom":makeQuery(id+"F2.boolean.opBoolean","MERGE",FACE,{"derivedFrom":[makeQuery(id+"F1.opExtrude","CAP_FACE",FACE,{"disambiguationData":[OSD([sQuery(id+"F0.wireOp",EDGE,"E1"),sQuery(id+"F0.wireOp",EDGE,"E2.bottom"),sQuery(id+"F0.wireOp",EDGE,"E2.top"),sQuery(id+"F0.wireOp",EDGE,"E3"),sQuery(id+"F0.wireOp",EDGE,"E7.MirrorC"),sQuery(id+"F0.wireOp",EDGE,"E8.MirrorC"),sQuery(id+"F0.wireOp",EDGE,"E9.MirrorCS"),sQuery(id+"F0.wireOp",EDGE,"E11.MirrorCS"),sQuery(id+"F0.wireOp",EDGE,"E12.MirrorC"),sQuery(id+"F0.wireOp",EDGE,"E13.MirrorC"),sQuery(id+"F0.wireOp",EDGE,"E14.MirrorCS"),sQuery(id+"F0.wireOp",EDGE,"E16.MirrorCS"),sQuery(id+"F0.wireOp",EDGE,"E17.MirrorCS"),sQuery(id+"F0.wireOp",EDGE,"E19.MirrorCS"),sQuery(id+"F0.wireOp",EDGE,"E20.MirrorC"),sQuery(id+"F0.wireOp",EDGE,"E21.MirrorC"),subQ3,subQ2,subQ1,subQ0,sQuery(id+"F0.wireOp",EDGE,"E25.bottom"),sQuery(id+"F0.wireOp",EDGE,"E25.top"),sQuery(id+"F0.wireOp",EDGE,"E25.left"),sQuery(id+"F0.wireOp",EDGE,"E25.right"),sQuery(id+"F0.wireOp",EDGE,"E26"),sQuery(id+"F0.wireOp",EDGE,"E27.trimOffspring"),sQuery(id+"F0.wireOp",EDGE,"E29"),sQuery(id+"F0.wireOp",EDGE,"E30.trimOffspring"),sQuery(id+"F0.wireOp",EDGE,"E32"),sQuery(id+"F0.wireOp",EDGE,"E33.trimOffspring"),sQuery(id+"F0.wireOp",EDGE,"E34"),sQuery(id+"F0.wireOp",EDGE,"E35.trimOffspring")])],"isStart":true}),makeQuery(id+"F2.opExtrude","CAP_FACE",FACE,{"disambiguationData":[OSD([subQ3,subQ2,subQ1,subQ0])],"isStart":true})]})});}
            var Q26;
            {var subQ0=sQuery(id+"F0.wireOp",EDGE,"E24.right");var subQ1=sQuery(id+"F0.wireOp",EDGE,"E24.left");var subQ2=sQuery(id+"F0.wireOp",EDGE,"E24.top");var subQ3=sQuery(id+"F0.wireOp",EDGE,"E24.bottom");Q26=makeQuery(id+"F4.boolean.opBoolean","SPLIT",FACE,{"disambiguationData":[TD([makeQuery(id+"F4.opExtrude","SWEPT_FACE",FACE,{"disambiguationData":[OSD([sQuery(id+"F3.wireOp",EDGE,"E41.1.0.10")])]})])],"derivedFrom":makeQuery(id+"F2.boolean.opBoolean","MERGE",FACE,{"derivedFrom":[makeQuery(id+"F1.opExtrude","CAP_FACE",FACE,{"disambiguationData":[OSD([sQuery(id+"F0.wireOp",EDGE,"E1"),sQuery(id+"F0.wireOp",EDGE,"E2.bottom"),sQuery(id+"F0.wireOp",EDGE,"E2.top"),sQuery(id+"F0.wireOp",EDGE,"E3"),sQuery(id+"F0.wireOp",EDGE,"E7.MirrorC"),sQuery(id+"F0.wireOp",EDGE,"E8.MirrorC"),sQuery(id+"F0.wireOp",EDGE,"E9.MirrorCS"),sQuery(id+"F0.wireOp",EDGE,"E11.MirrorCS"),sQuery(id+"F0.wireOp",EDGE,"E12.MirrorC"),sQuery(id+"F0.wireOp",EDGE,"E13.MirrorC"),sQuery(id+"F0.wireOp",EDGE,"E14.MirrorCS"),sQuery(id+"F0.wireOp",EDGE,"E16.MirrorCS"),sQuery(id+"F0.wireOp",EDGE,"E17.MirrorCS"),sQuery(id+"F0.wireOp",EDGE,"E19.MirrorCS"),sQuery(id+"F0.wireOp",EDGE,"E20.MirrorC"),sQuery(id+"F0.wireOp",EDGE,"E21.MirrorC"),subQ3,subQ2,subQ1,subQ0,sQuery(id+"F0.wireOp",EDGE,"E25.bottom"),sQuery(id+"F0.wireOp",EDGE,"E25.top"),sQuery(id+"F0.wireOp",EDGE,"E25.left"),sQuery(id+"F0.wireOp",EDGE,"E25.right"),sQuery(id+"F0.wireOp",EDGE,"E26"),sQuery(id+"F0.wireOp",EDGE,"E27.trimOffspring"),sQuery(id+"F0.wireOp",EDGE,"E29"),sQuery(id+"F0.wireOp",EDGE,"E30.trimOffspring"),sQuery(id+"F0.wireOp",EDGE,"E32"),sQuery(id+"F0.wireOp",EDGE,"E33.trimOffspring"),sQuery(id+"F0.wireOp",EDGE,"E34"),sQuery(id+"F0.wireOp",EDGE,"E35.trimOffspring")])],"isStart":true}),makeQuery(id+"F2.opExtrude","CAP_FACE",FACE,{"disambiguationData":[OSD([subQ3,subQ2,subQ1,subQ0])],"isStart":true})]})});}
            var Q27;
            {var subQ0=sQuery(id+"F0.wireOp",EDGE,"E24.right");var subQ1=sQuery(id+"F0.wireOp",EDGE,"E24.left");var subQ2=sQuery(id+"F0.wireOp",EDGE,"E24.top");var subQ3=sQuery(id+"F0.wireOp",EDGE,"E24.bottom");Q27=makeQuery(id+"F4.boolean.opBoolean","SPLIT",FACE,{"disambiguationData":[TD([makeQuery(id+"F4.opExtrude","SWEPT_FACE",FACE,{"disambiguationData":[OSD([sQuery(id+"F3.wireOp",EDGE,"E41.1.0.1")])]})])],"derivedFrom":makeQuery(id+"F2.boolean.opBoolean","MERGE",FACE,{"derivedFrom":[makeQuery(id+"F1.opExtrude","CAP_FACE",FACE,{"disambiguationData":[OSD([sQuery(id+"F0.wireOp",EDGE,"E1"),sQuery(id+"F0.wireOp",EDGE,"E2.bottom"),sQuery(id+"F0.wireOp",EDGE,"E2.top"),sQuery(id+"F0.wireOp",EDGE,"E3"),sQuery(id+"F0.wireOp",EDGE,"E7.MirrorC"),sQuery(id+"F0.wireOp",EDGE,"E8.MirrorC"),sQuery(id+"F0.wireOp",EDGE,"E9.MirrorCS"),sQuery(id+"F0.wireOp",EDGE,"E11.MirrorCS"),sQuery(id+"F0.wireOp",EDGE,"E12.MirrorC"),sQuery(id+"F0.wireOp",EDGE,"E13.MirrorC"),sQuery(id+"F0.wireOp",EDGE,"E14.MirrorCS"),sQuery(id+"F0.wireOp",EDGE,"E16.MirrorCS"),sQuery(id+"F0.wireOp",EDGE,"E17.MirrorCS"),sQuery(id+"F0.wireOp",EDGE,"E19.MirrorCS"),sQuery(id+"F0.wireOp",EDGE,"E20.MirrorC"),sQuery(id+"F0.wireOp",EDGE,"E21.MirrorC"),subQ3,subQ2,subQ1,subQ0,sQuery(id+"F0.wireOp",EDGE,"E25.bottom"),sQuery(id+"F0.wireOp",EDGE,"E25.top"),sQuery(id+"F0.wireOp",EDGE,"E25.left"),sQuery(id+"F0.wireOp",EDGE,"E25.right"),sQuery(id+"F0.wireOp",EDGE,"E26"),sQuery(id+"F0.wireOp",EDGE,"E27.trimOffspring"),sQuery(id+"F0.wireOp",EDGE,"E29"),sQuery(id+"F0.wireOp",EDGE,"E30.trimOffspring"),sQuery(id+"F0.wireOp",EDGE,"E32"),sQuery(id+"F0.wireOp",EDGE,"E33.trimOffspring"),sQuery(id+"F0.wireOp",EDGE,"E34"),sQuery(id+"F0.wireOp",EDGE,"E35.trimOffspring")])],"isStart":true}),makeQuery(id+"F2.opExtrude","CAP_FACE",FACE,{"disambiguationData":[OSD([subQ3,subQ2,subQ1,subQ0])],"isStart":true})]})});}
            var Q28;
            {var subQ0=sQuery(id+"F0.wireOp",EDGE,"E24.right");var subQ1=sQuery(id+"F0.wireOp",EDGE,"E24.left");var subQ2=sQuery(id+"F0.wireOp",EDGE,"E24.top");var subQ3=sQuery(id+"F0.wireOp",EDGE,"E24.bottom");Q28=makeQuery(id+"F4.boolean.opBoolean","SPLIT",FACE,{"disambiguationData":[TD([makeQuery(id+"F4.opExtrude","SWEPT_FACE",FACE,{"disambiguationData":[OSD([sQuery(id+"F3.wireOp",EDGE,"E41.2.0.1")])]})])],"derivedFrom":makeQuery(id+"F2.boolean.opBoolean","MERGE",FACE,{"derivedFrom":[makeQuery(id+"F1.opExtrude","CAP_FACE",FACE,{"disambiguationData":[OSD([sQuery(id+"F0.wireOp",EDGE,"E1"),sQuery(id+"F0.wireOp",EDGE,"E2.bottom"),sQuery(id+"F0.wireOp",EDGE,"E2.top"),sQuery(id+"F0.wireOp",EDGE,"E3"),sQuery(id+"F0.wireOp",EDGE,"E7.MirrorC"),sQuery(id+"F0.wireOp",EDGE,"E8.MirrorC"),sQuery(id+"F0.wireOp",EDGE,"E9.MirrorCS"),sQuery(id+"F0.wireOp",EDGE,"E11.MirrorCS"),sQuery(id+"F0.wireOp",EDGE,"E12.MirrorC"),sQuery(id+"F0.wireOp",EDGE,"E13.MirrorC"),sQuery(id+"F0.wireOp",EDGE,"E14.MirrorCS"),sQuery(id+"F0.wireOp",EDGE,"E16.MirrorCS"),sQuery(id+"F0.wireOp",EDGE,"E17.MirrorCS"),sQuery(id+"F0.wireOp",EDGE,"E19.MirrorCS"),sQuery(id+"F0.wireOp",EDGE,"E20.MirrorC"),sQuery(id+"F0.wireOp",EDGE,"E21.MirrorC"),subQ3,subQ2,subQ1,subQ0,sQuery(id+"F0.wireOp",EDGE,"E25.bottom"),sQuery(id+"F0.wireOp",EDGE,"E25.top"),sQuery(id+"F0.wireOp",EDGE,"E25.left"),sQuery(id+"F0.wireOp",EDGE,"E25.right"),sQuery(id+"F0.wireOp",EDGE,"E26"),sQuery(id+"F0.wireOp",EDGE,"E27.trimOffspring"),sQuery(id+"F0.wireOp",EDGE,"E29"),sQuery(id+"F0.wireOp",EDGE,"E30.trimOffspring"),sQuery(id+"F0.wireOp",EDGE,"E32"),sQuery(id+"F0.wireOp",EDGE,"E33.trimOffspring"),sQuery(id+"F0.wireOp",EDGE,"E34"),sQuery(id+"F0.wireOp",EDGE,"E35.trimOffspring")])],"isStart":true}),makeQuery(id+"F2.opExtrude","CAP_FACE",FACE,{"disambiguationData":[OSD([subQ3,subQ2,subQ1,subQ0])],"isStart":true})]})});}
            var Q29;
            {var subQ0=sQuery(id+"F0.wireOp",EDGE,"E24.right");var subQ1=sQuery(id+"F0.wireOp",EDGE,"E24.left");var subQ2=sQuery(id+"F0.wireOp",EDGE,"E24.top");var subQ3=sQuery(id+"F0.wireOp",EDGE,"E24.bottom");Q29=makeQuery(id+"F4.boolean.opBoolean","SPLIT",FACE,{"disambiguationData":[TD([makeQuery(id+"F4.opExtrude","SWEPT_FACE",FACE,{"disambiguationData":[OSD([sQuery(id+"F3.wireOp",EDGE,"E41.2.0.10")])]})])],"derivedFrom":makeQuery(id+"F2.boolean.opBoolean","MERGE",FACE,{"derivedFrom":[makeQuery(id+"F1.opExtrude","CAP_FACE",FACE,{"disambiguationData":[OSD([sQuery(id+"F0.wireOp",EDGE,"E1"),sQuery(id+"F0.wireOp",EDGE,"E2.bottom"),sQuery(id+"F0.wireOp",EDGE,"E2.top"),sQuery(id+"F0.wireOp",EDGE,"E3"),sQuery(id+"F0.wireOp",EDGE,"E7.MirrorC"),sQuery(id+"F0.wireOp",EDGE,"E8.MirrorC"),sQuery(id+"F0.wireOp",EDGE,"E9.MirrorCS"),sQuery(id+"F0.wireOp",EDGE,"E11.MirrorCS"),sQuery(id+"F0.wireOp",EDGE,"E12.MirrorC"),sQuery(id+"F0.wireOp",EDGE,"E13.MirrorC"),sQuery(id+"F0.wireOp",EDGE,"E14.MirrorCS"),sQuery(id+"F0.wireOp",EDGE,"E16.MirrorCS"),sQuery(id+"F0.wireOp",EDGE,"E17.MirrorCS"),sQuery(id+"F0.wireOp",EDGE,"E19.MirrorCS"),sQuery(id+"F0.wireOp",EDGE,"E20.MirrorC"),sQuery(id+"F0.wireOp",EDGE,"E21.MirrorC"),subQ3,subQ2,subQ1,subQ0,sQuery(id+"F0.wireOp",EDGE,"E25.bottom"),sQuery(id+"F0.wireOp",EDGE,"E25.top"),sQuery(id+"F0.wireOp",EDGE,"E25.left"),sQuery(id+"F0.wireOp",EDGE,"E25.right"),sQuery(id+"F0.wireOp",EDGE,"E26"),sQuery(id+"F0.wireOp",EDGE,"E27.trimOffspring"),sQuery(id+"F0.wireOp",EDGE,"E29"),sQuery(id+"F0.wireOp",EDGE,"E30.trimOffspring"),sQuery(id+"F0.wireOp",EDGE,"E32"),sQuery(id+"F0.wireOp",EDGE,"E33.trimOffspring"),sQuery(id+"F0.wireOp",EDGE,"E34"),sQuery(id+"F0.wireOp",EDGE,"E35.trimOffspring")])],"isStart":true}),makeQuery(id+"F2.opExtrude","CAP_FACE",FACE,{"disambiguationData":[OSD([subQ3,subQ2,subQ1,subQ0])],"isStart":true})]})});}
            var Q30;
            {var subQ0=sQuery(id+"F0.wireOp",EDGE,"E24.right");var subQ1=sQuery(id+"F0.wireOp",EDGE,"E24.left");var subQ2=sQuery(id+"F0.wireOp",EDGE,"E24.top");var subQ3=sQuery(id+"F0.wireOp",EDGE,"E24.bottom");Q30=makeQuery(id+"F4.boolean.opBoolean","SPLIT",FACE,{"disambiguationData":[TD([makeQuery(id+"F4.opExtrude","SWEPT_FACE",FACE,{"disambiguationData":[OSD([sQuery(id+"F3.wireOp",EDGE,"E41.2.0.9")])]})])],"derivedFrom":makeQuery(id+"F2.boolean.opBoolean","MERGE",FACE,{"derivedFrom":[makeQuery(id+"F1.opExtrude","CAP_FACE",FACE,{"disambiguationData":[OSD([sQuery(id+"F0.wireOp",EDGE,"E1"),sQuery(id+"F0.wireOp",EDGE,"E2.bottom"),sQuery(id+"F0.wireOp",EDGE,"E2.top"),sQuery(id+"F0.wireOp",EDGE,"E3"),sQuery(id+"F0.wireOp",EDGE,"E7.MirrorC"),sQuery(id+"F0.wireOp",EDGE,"E8.MirrorC"),sQuery(id+"F0.wireOp",EDGE,"E9.MirrorCS"),sQuery(id+"F0.wireOp",EDGE,"E11.MirrorCS"),sQuery(id+"F0.wireOp",EDGE,"E12.MirrorC"),sQuery(id+"F0.wireOp",EDGE,"E13.MirrorC"),sQuery(id+"F0.wireOp",EDGE,"E14.MirrorCS"),sQuery(id+"F0.wireOp",EDGE,"E16.MirrorCS"),sQuery(id+"F0.wireOp",EDGE,"E17.MirrorCS"),sQuery(id+"F0.wireOp",EDGE,"E19.MirrorCS"),sQuery(id+"F0.wireOp",EDGE,"E20.MirrorC"),sQuery(id+"F0.wireOp",EDGE,"E21.MirrorC"),subQ3,subQ2,subQ1,subQ0,sQuery(id+"F0.wireOp",EDGE,"E25.bottom"),sQuery(id+"F0.wireOp",EDGE,"E25.top"),sQuery(id+"F0.wireOp",EDGE,"E25.left"),sQuery(id+"F0.wireOp",EDGE,"E25.right"),sQuery(id+"F0.wireOp",EDGE,"E26"),sQuery(id+"F0.wireOp",EDGE,"E27.trimOffspring"),sQuery(id+"F0.wireOp",EDGE,"E29"),sQuery(id+"F0.wireOp",EDGE,"E30.trimOffspring"),sQuery(id+"F0.wireOp",EDGE,"E32"),sQuery(id+"F0.wireOp",EDGE,"E33.trimOffspring"),sQuery(id+"F0.wireOp",EDGE,"E34"),sQuery(id+"F0.wireOp",EDGE,"E35.trimOffspring")])],"isStart":true}),makeQuery(id+"F2.opExtrude","CAP_FACE",FACE,{"disambiguationData":[OSD([subQ3,subQ2,subQ1,subQ0])],"isStart":true})]})});}
            var Q31;
            {var subQ0=sQuery(id+"F0.wireOp",EDGE,"E24.right");var subQ1=sQuery(id+"F0.wireOp",EDGE,"E24.left");var subQ2=sQuery(id+"F0.wireOp",EDGE,"E24.top");var subQ3=sQuery(id+"F0.wireOp",EDGE,"E24.bottom");Q31=makeQuery(id+"F4.boolean.opBoolean","SPLIT",FACE,{"disambiguationData":[TD([makeQuery(id+"F4.opExtrude","SWEPT_FACE",FACE,{"disambiguationData":[OSD([sQuery(id+"F3.wireOp",EDGE,"E41.2.0.7")])]})])],"derivedFrom":makeQuery(id+"F2.boolean.opBoolean","MERGE",FACE,{"derivedFrom":[makeQuery(id+"F1.opExtrude","CAP_FACE",FACE,{"disambiguationData":[OSD([sQuery(id+"F0.wireOp",EDGE,"E1"),sQuery(id+"F0.wireOp",EDGE,"E2.bottom"),sQuery(id+"F0.wireOp",EDGE,"E2.top"),sQuery(id+"F0.wireOp",EDGE,"E3"),sQuery(id+"F0.wireOp",EDGE,"E7.MirrorC"),sQuery(id+"F0.wireOp",EDGE,"E8.MirrorC"),sQuery(id+"F0.wireOp",EDGE,"E9.MirrorCS"),sQuery(id+"F0.wireOp",EDGE,"E11.MirrorCS"),sQuery(id+"F0.wireOp",EDGE,"E12.MirrorC"),sQuery(id+"F0.wireOp",EDGE,"E13.MirrorC"),sQuery(id+"F0.wireOp",EDGE,"E14.MirrorCS"),sQuery(id+"F0.wireOp",EDGE,"E16.MirrorCS"),sQuery(id+"F0.wireOp",EDGE,"E17.MirrorCS"),sQuery(id+"F0.wireOp",EDGE,"E19.MirrorCS"),sQuery(id+"F0.wireOp",EDGE,"E20.MirrorC"),sQuery(id+"F0.wireOp",EDGE,"E21.MirrorC"),subQ3,subQ2,subQ1,subQ0,sQuery(id+"F0.wireOp",EDGE,"E25.bottom"),sQuery(id+"F0.wireOp",EDGE,"E25.top"),sQuery(id+"F0.wireOp",EDGE,"E25.left"),sQuery(id+"F0.wireOp",EDGE,"E25.right"),sQuery(id+"F0.wireOp",EDGE,"E26"),sQuery(id+"F0.wireOp",EDGE,"E27.trimOffspring"),sQuery(id+"F0.wireOp",EDGE,"E29"),sQuery(id+"F0.wireOp",EDGE,"E30.trimOffspring"),sQuery(id+"F0.wireOp",EDGE,"E32"),sQuery(id+"F0.wireOp",EDGE,"E33.trimOffspring"),sQuery(id+"F0.wireOp",EDGE,"E34"),sQuery(id+"F0.wireOp",EDGE,"E35.trimOffspring")])],"isStart":true}),makeQuery(id+"F2.opExtrude","CAP_FACE",FACE,{"disambiguationData":[OSD([subQ3,subQ2,subQ1,subQ0])],"isStart":true})]})});}
            var Q32;
            {var subQ0=sQuery(id+"F0.wireOp",EDGE,"E24.right");var subQ1=sQuery(id+"F0.wireOp",EDGE,"E24.left");var subQ2=sQuery(id+"F0.wireOp",EDGE,"E24.top");var subQ3=sQuery(id+"F0.wireOp",EDGE,"E24.bottom");Q32=makeQuery(id+"F4.boolean.opBoolean","SPLIT",FACE,{"disambiguationData":[TD([makeQuery(id+"F4.opExtrude","SWEPT_FACE",FACE,{"disambiguationData":[OSD([sQuery(id+"F3.wireOp",EDGE,"E41.2.0.8")])]})])],"derivedFrom":makeQuery(id+"F2.boolean.opBoolean","MERGE",FACE,{"derivedFrom":[makeQuery(id+"F1.opExtrude","CAP_FACE",FACE,{"disambiguationData":[OSD([sQuery(id+"F0.wireOp",EDGE,"E1"),sQuery(id+"F0.wireOp",EDGE,"E2.bottom"),sQuery(id+"F0.wireOp",EDGE,"E2.top"),sQuery(id+"F0.wireOp",EDGE,"E3"),sQuery(id+"F0.wireOp",EDGE,"E7.MirrorC"),sQuery(id+"F0.wireOp",EDGE,"E8.MirrorC"),sQuery(id+"F0.wireOp",EDGE,"E9.MirrorCS"),sQuery(id+"F0.wireOp",EDGE,"E11.MirrorCS"),sQuery(id+"F0.wireOp",EDGE,"E12.MirrorC"),sQuery(id+"F0.wireOp",EDGE,"E13.MirrorC"),sQuery(id+"F0.wireOp",EDGE,"E14.MirrorCS"),sQuery(id+"F0.wireOp",EDGE,"E16.MirrorCS"),sQuery(id+"F0.wireOp",EDGE,"E17.MirrorCS"),sQuery(id+"F0.wireOp",EDGE,"E19.MirrorCS"),sQuery(id+"F0.wireOp",EDGE,"E20.MirrorC"),sQuery(id+"F0.wireOp",EDGE,"E21.MirrorC"),subQ3,subQ2,subQ1,subQ0,sQuery(id+"F0.wireOp",EDGE,"E25.bottom"),sQuery(id+"F0.wireOp",EDGE,"E25.top"),sQuery(id+"F0.wireOp",EDGE,"E25.left"),sQuery(id+"F0.wireOp",EDGE,"E25.right"),sQuery(id+"F0.wireOp",EDGE,"E26"),sQuery(id+"F0.wireOp",EDGE,"E27.trimOffspring"),sQuery(id+"F0.wireOp",EDGE,"E29"),sQuery(id+"F0.wireOp",EDGE,"E30.trimOffspring"),sQuery(id+"F0.wireOp",EDGE,"E32"),sQuery(id+"F0.wireOp",EDGE,"E33.trimOffspring"),sQuery(id+"F0.wireOp",EDGE,"E34"),sQuery(id+"F0.wireOp",EDGE,"E35.trimOffspring")])],"isStart":true}),makeQuery(id+"F2.opExtrude","CAP_FACE",FACE,{"disambiguationData":[OSD([subQ3,subQ2,subQ1,subQ0])],"isStart":true})]})});}
            var Q33;
            {var subQ0=sQuery(id+"F0.wireOp",EDGE,"E24.right");var subQ1=sQuery(id+"F0.wireOp",EDGE,"E24.left");var subQ2=sQuery(id+"F0.wireOp",EDGE,"E24.top");var subQ3=sQuery(id+"F0.wireOp",EDGE,"E24.bottom");Q33=makeQuery(id+"F4.boolean.opBoolean","SPLIT",FACE,{"disambiguationData":[TD([makeQuery(id+"F4.opExtrude","SWEPT_FACE",FACE,{"disambiguationData":[OSD([sQuery(id+"F3.wireOp",EDGE,"E41.2.0.0")])]})])],"derivedFrom":makeQuery(id+"F2.boolean.opBoolean","MERGE",FACE,{"derivedFrom":[makeQuery(id+"F1.opExtrude","CAP_FACE",FACE,{"disambiguationData":[OSD([sQuery(id+"F0.wireOp",EDGE,"E1"),sQuery(id+"F0.wireOp",EDGE,"E2.bottom"),sQuery(id+"F0.wireOp",EDGE,"E2.top"),sQuery(id+"F0.wireOp",EDGE,"E3"),sQuery(id+"F0.wireOp",EDGE,"E7.MirrorC"),sQuery(id+"F0.wireOp",EDGE,"E8.MirrorC"),sQuery(id+"F0.wireOp",EDGE,"E9.MirrorCS"),sQuery(id+"F0.wireOp",EDGE,"E11.MirrorCS"),sQuery(id+"F0.wireOp",EDGE,"E12.MirrorC"),sQuery(id+"F0.wireOp",EDGE,"E13.MirrorC"),sQuery(id+"F0.wireOp",EDGE,"E14.MirrorCS"),sQuery(id+"F0.wireOp",EDGE,"E16.MirrorCS"),sQuery(id+"F0.wireOp",EDGE,"E17.MirrorCS"),sQuery(id+"F0.wireOp",EDGE,"E19.MirrorCS"),sQuery(id+"F0.wireOp",EDGE,"E20.MirrorC"),sQuery(id+"F0.wireOp",EDGE,"E21.MirrorC"),subQ3,subQ2,subQ1,subQ0,sQuery(id+"F0.wireOp",EDGE,"E25.bottom"),sQuery(id+"F0.wireOp",EDGE,"E25.top"),sQuery(id+"F0.wireOp",EDGE,"E25.left"),sQuery(id+"F0.wireOp",EDGE,"E25.right"),sQuery(id+"F0.wireOp",EDGE,"E26"),sQuery(id+"F0.wireOp",EDGE,"E27.trimOffspring"),sQuery(id+"F0.wireOp",EDGE,"E29"),sQuery(id+"F0.wireOp",EDGE,"E30.trimOffspring"),sQuery(id+"F0.wireOp",EDGE,"E32"),sQuery(id+"F0.wireOp",EDGE,"E33.trimOffspring"),sQuery(id+"F0.wireOp",EDGE,"E34"),sQuery(id+"F0.wireOp",EDGE,"E35.trimOffspring")])],"isStart":true}),makeQuery(id+"F2.opExtrude","CAP_FACE",FACE,{"disambiguationData":[OSD([subQ3,subQ2,subQ1,subQ0])],"isStart":true})]})});}
            var Q34;
            {var subQ0=sQuery(id+"F0.wireOp",EDGE,"E24.right");var subQ1=sQuery(id+"F0.wireOp",EDGE,"E24.left");var subQ2=sQuery(id+"F0.wireOp",EDGE,"E24.top");var subQ3=sQuery(id+"F0.wireOp",EDGE,"E24.bottom");Q34=makeQuery(id+"F4.boolean.opBoolean","SPLIT",FACE,{"disambiguationData":[TD([makeQuery(id+"F4.opExtrude","SWEPT_FACE",FACE,{"disambiguationData":[OSD([sQuery(id+"F3.wireOp",EDGE,"E41.2.0.11")])]})])],"derivedFrom":makeQuery(id+"F2.boolean.opBoolean","MERGE",FACE,{"derivedFrom":[makeQuery(id+"F1.opExtrude","CAP_FACE",FACE,{"disambiguationData":[OSD([sQuery(id+"F0.wireOp",EDGE,"E1"),sQuery(id+"F0.wireOp",EDGE,"E2.bottom"),sQuery(id+"F0.wireOp",EDGE,"E2.top"),sQuery(id+"F0.wireOp",EDGE,"E3"),sQuery(id+"F0.wireOp",EDGE,"E7.MirrorC"),sQuery(id+"F0.wireOp",EDGE,"E8.MirrorC"),sQuery(id+"F0.wireOp",EDGE,"E9.MirrorCS"),sQuery(id+"F0.wireOp",EDGE,"E11.MirrorCS"),sQuery(id+"F0.wireOp",EDGE,"E12.MirrorC"),sQuery(id+"F0.wireOp",EDGE,"E13.MirrorC"),sQuery(id+"F0.wireOp",EDGE,"E14.MirrorCS"),sQuery(id+"F0.wireOp",EDGE,"E16.MirrorCS"),sQuery(id+"F0.wireOp",EDGE,"E17.MirrorCS"),sQuery(id+"F0.wireOp",EDGE,"E19.MirrorCS"),sQuery(id+"F0.wireOp",EDGE,"E20.MirrorC"),sQuery(id+"F0.wireOp",EDGE,"E21.MirrorC"),subQ3,subQ2,subQ1,subQ0,sQuery(id+"F0.wireOp",EDGE,"E25.bottom"),sQuery(id+"F0.wireOp",EDGE,"E25.top"),sQuery(id+"F0.wireOp",EDGE,"E25.left"),sQuery(id+"F0.wireOp",EDGE,"E25.right"),sQuery(id+"F0.wireOp",EDGE,"E26"),sQuery(id+"F0.wireOp",EDGE,"E27.trimOffspring"),sQuery(id+"F0.wireOp",EDGE,"E29"),sQuery(id+"F0.wireOp",EDGE,"E30.trimOffspring"),sQuery(id+"F0.wireOp",EDGE,"E32"),sQuery(id+"F0.wireOp",EDGE,"E33.trimOffspring"),sQuery(id+"F0.wireOp",EDGE,"E34"),sQuery(id+"F0.wireOp",EDGE,"E35.trimOffspring")])],"isStart":true}),makeQuery(id+"F2.opExtrude","CAP_FACE",FACE,{"disambiguationData":[OSD([subQ3,subQ2,subQ1,subQ0])],"isStart":true})]})});}
            var Q35;
            {var subQ0=sQuery(id+"F0.wireOp",EDGE,"E24.right");var subQ1=sQuery(id+"F0.wireOp",EDGE,"E24.left");var subQ2=sQuery(id+"F0.wireOp",EDGE,"E24.top");var subQ3=sQuery(id+"F0.wireOp",EDGE,"E24.bottom");Q35=makeQuery(id+"F4.boolean.opBoolean","SPLIT",FACE,{"disambiguationData":[TD([makeQuery(id+"F4.opExtrude","SWEPT_FACE",FACE,{"disambiguationData":[OSD([sQuery(id+"F3.wireOp",EDGE,"E41.2.0.2")])]})])],"derivedFrom":makeQuery(id+"F2.boolean.opBoolean","MERGE",FACE,{"derivedFrom":[makeQuery(id+"F1.opExtrude","CAP_FACE",FACE,{"disambiguationData":[OSD([sQuery(id+"F0.wireOp",EDGE,"E1"),sQuery(id+"F0.wireOp",EDGE,"E2.bottom"),sQuery(id+"F0.wireOp",EDGE,"E2.top"),sQuery(id+"F0.wireOp",EDGE,"E3"),sQuery(id+"F0.wireOp",EDGE,"E7.MirrorC"),sQuery(id+"F0.wireOp",EDGE,"E8.MirrorC"),sQuery(id+"F0.wireOp",EDGE,"E9.MirrorCS"),sQuery(id+"F0.wireOp",EDGE,"E11.MirrorCS"),sQuery(id+"F0.wireOp",EDGE,"E12.MirrorC"),sQuery(id+"F0.wireOp",EDGE,"E13.MirrorC"),sQuery(id+"F0.wireOp",EDGE,"E14.MirrorCS"),sQuery(id+"F0.wireOp",EDGE,"E16.MirrorCS"),sQuery(id+"F0.wireOp",EDGE,"E17.MirrorCS"),sQuery(id+"F0.wireOp",EDGE,"E19.MirrorCS"),sQuery(id+"F0.wireOp",EDGE,"E20.MirrorC"),sQuery(id+"F0.wireOp",EDGE,"E21.MirrorC"),subQ3,subQ2,subQ1,subQ0,sQuery(id+"F0.wireOp",EDGE,"E25.bottom"),sQuery(id+"F0.wireOp",EDGE,"E25.top"),sQuery(id+"F0.wireOp",EDGE,"E25.left"),sQuery(id+"F0.wireOp",EDGE,"E25.right"),sQuery(id+"F0.wireOp",EDGE,"E26"),sQuery(id+"F0.wireOp",EDGE,"E27.trimOffspring"),sQuery(id+"F0.wireOp",EDGE,"E29"),sQuery(id+"F0.wireOp",EDGE,"E30.trimOffspring"),sQuery(id+"F0.wireOp",EDGE,"E32"),sQuery(id+"F0.wireOp",EDGE,"E33.trimOffspring"),sQuery(id+"F0.wireOp",EDGE,"E34"),sQuery(id+"F0.wireOp",EDGE,"E35.trimOffspring")])],"isStart":true}),makeQuery(id+"F2.opExtrude","CAP_FACE",FACE,{"disambiguationData":[OSD([subQ3,subQ2,subQ1,subQ0])],"isStart":true})]})});}
            var Q36;
            {var subQ0=sQuery(id+"F0.wireOp",EDGE,"E24.right");var subQ1=sQuery(id+"F0.wireOp",EDGE,"E24.left");var subQ2=sQuery(id+"F0.wireOp",EDGE,"E24.top");var subQ3=sQuery(id+"F0.wireOp",EDGE,"E24.bottom");Q36=makeQuery(id+"F4.boolean.opBoolean","SPLIT",FACE,{"disambiguationData":[TD([makeQuery(id+"F4.opExtrude","SWEPT_FACE",FACE,{"disambiguationData":[OSD([sQuery(id+"F3.wireOp",EDGE,"E41.2.0.6")])]})])],"derivedFrom":makeQuery(id+"F2.boolean.opBoolean","MERGE",FACE,{"derivedFrom":[makeQuery(id+"F1.opExtrude","CAP_FACE",FACE,{"disambiguationData":[OSD([sQuery(id+"F0.wireOp",EDGE,"E1"),sQuery(id+"F0.wireOp",EDGE,"E2.bottom"),sQuery(id+"F0.wireOp",EDGE,"E2.top"),sQuery(id+"F0.wireOp",EDGE,"E3"),sQuery(id+"F0.wireOp",EDGE,"E7.MirrorC"),sQuery(id+"F0.wireOp",EDGE,"E8.MirrorC"),sQuery(id+"F0.wireOp",EDGE,"E9.MirrorCS"),sQuery(id+"F0.wireOp",EDGE,"E11.MirrorCS"),sQuery(id+"F0.wireOp",EDGE,"E12.MirrorC"),sQuery(id+"F0.wireOp",EDGE,"E13.MirrorC"),sQuery(id+"F0.wireOp",EDGE,"E14.MirrorCS"),sQuery(id+"F0.wireOp",EDGE,"E16.MirrorCS"),sQuery(id+"F0.wireOp",EDGE,"E17.MirrorCS"),sQuery(id+"F0.wireOp",EDGE,"E19.MirrorCS"),sQuery(id+"F0.wireOp",EDGE,"E20.MirrorC"),sQuery(id+"F0.wireOp",EDGE,"E21.MirrorC"),subQ3,subQ2,subQ1,subQ0,sQuery(id+"F0.wireOp",EDGE,"E25.bottom"),sQuery(id+"F0.wireOp",EDGE,"E25.top"),sQuery(id+"F0.wireOp",EDGE,"E25.left"),sQuery(id+"F0.wireOp",EDGE,"E25.right"),sQuery(id+"F0.wireOp",EDGE,"E26"),sQuery(id+"F0.wireOp",EDGE,"E27.trimOffspring"),sQuery(id+"F0.wireOp",EDGE,"E29"),sQuery(id+"F0.wireOp",EDGE,"E30.trimOffspring"),sQuery(id+"F0.wireOp",EDGE,"E32"),sQuery(id+"F0.wireOp",EDGE,"E33.trimOffspring"),sQuery(id+"F0.wireOp",EDGE,"E34"),sQuery(id+"F0.wireOp",EDGE,"E35.trimOffspring")])],"isStart":true}),makeQuery(id+"F2.opExtrude","CAP_FACE",FACE,{"disambiguationData":[OSD([subQ3,subQ2,subQ1,subQ0])],"isStart":true})]})});}
            var Q37;
            {var subQ0=sQuery(id+"F0.wireOp",EDGE,"E24.right");var subQ1=sQuery(id+"F0.wireOp",EDGE,"E24.left");var subQ2=sQuery(id+"F0.wireOp",EDGE,"E24.top");var subQ3=sQuery(id+"F0.wireOp",EDGE,"E24.bottom");Q37=makeQuery(id+"F4.boolean.opBoolean","SPLIT",FACE,{"disambiguationData":[TD([makeQuery(id+"F4.opExtrude","SWEPT_FACE",FACE,{"disambiguationData":[OSD([sQuery(id+"F3.wireOp",EDGE,"E41.2.0.12")])]})])],"derivedFrom":makeQuery(id+"F2.boolean.opBoolean","MERGE",FACE,{"derivedFrom":[makeQuery(id+"F1.opExtrude","CAP_FACE",FACE,{"disambiguationData":[OSD([sQuery(id+"F0.wireOp",EDGE,"E1"),sQuery(id+"F0.wireOp",EDGE,"E2.bottom"),sQuery(id+"F0.wireOp",EDGE,"E2.top"),sQuery(id+"F0.wireOp",EDGE,"E3"),sQuery(id+"F0.wireOp",EDGE,"E7.MirrorC"),sQuery(id+"F0.wireOp",EDGE,"E8.MirrorC"),sQuery(id+"F0.wireOp",EDGE,"E9.MirrorCS"),sQuery(id+"F0.wireOp",EDGE,"E11.MirrorCS"),sQuery(id+"F0.wireOp",EDGE,"E12.MirrorC"),sQuery(id+"F0.wireOp",EDGE,"E13.MirrorC"),sQuery(id+"F0.wireOp",EDGE,"E14.MirrorCS"),sQuery(id+"F0.wireOp",EDGE,"E16.MirrorCS"),sQuery(id+"F0.wireOp",EDGE,"E17.MirrorCS"),sQuery(id+"F0.wireOp",EDGE,"E19.MirrorCS"),sQuery(id+"F0.wireOp",EDGE,"E20.MirrorC"),sQuery(id+"F0.wireOp",EDGE,"E21.MirrorC"),subQ3,subQ2,subQ1,subQ0,sQuery(id+"F0.wireOp",EDGE,"E25.bottom"),sQuery(id+"F0.wireOp",EDGE,"E25.top"),sQuery(id+"F0.wireOp",EDGE,"E25.left"),sQuery(id+"F0.wireOp",EDGE,"E25.right"),sQuery(id+"F0.wireOp",EDGE,"E26"),sQuery(id+"F0.wireOp",EDGE,"E27.trimOffspring"),sQuery(id+"F0.wireOp",EDGE,"E29"),sQuery(id+"F0.wireOp",EDGE,"E30.trimOffspring"),sQuery(id+"F0.wireOp",EDGE,"E32"),sQuery(id+"F0.wireOp",EDGE,"E33.trimOffspring"),sQuery(id+"F0.wireOp",EDGE,"E34"),sQuery(id+"F0.wireOp",EDGE,"E35.trimOffspring")])],"isStart":true}),makeQuery(id+"F2.opExtrude","CAP_FACE",FACE,{"disambiguationData":[OSD([subQ3,subQ2,subQ1,subQ0])],"isStart":true})]})});}
            var Q38;
            {var subQ0=sQuery(id+"F0.wireOp",EDGE,"E24.right");var subQ1=sQuery(id+"F0.wireOp",EDGE,"E24.left");var subQ2=sQuery(id+"F0.wireOp",EDGE,"E24.top");var subQ3=sQuery(id+"F0.wireOp",EDGE,"E24.bottom");Q38=makeQuery(id+"F4.boolean.opBoolean","SPLIT",FACE,{"disambiguationData":[TD([makeQuery(id+"F4.opExtrude","SWEPT_FACE",FACE,{"disambiguationData":[OSD([sQuery(id+"F3.wireOp",EDGE,"E41.2.0.3")])]})])],"derivedFrom":makeQuery(id+"F2.boolean.opBoolean","MERGE",FACE,{"derivedFrom":[makeQuery(id+"F1.opExtrude","CAP_FACE",FACE,{"disambiguationData":[OSD([sQuery(id+"F0.wireOp",EDGE,"E1"),sQuery(id+"F0.wireOp",EDGE,"E2.bottom"),sQuery(id+"F0.wireOp",EDGE,"E2.top"),sQuery(id+"F0.wireOp",EDGE,"E3"),sQuery(id+"F0.wireOp",EDGE,"E7.MirrorC"),sQuery(id+"F0.wireOp",EDGE,"E8.MirrorC"),sQuery(id+"F0.wireOp",EDGE,"E9.MirrorCS"),sQuery(id+"F0.wireOp",EDGE,"E11.MirrorCS"),sQuery(id+"F0.wireOp",EDGE,"E12.MirrorC"),sQuery(id+"F0.wireOp",EDGE,"E13.MirrorC"),sQuery(id+"F0.wireOp",EDGE,"E14.MirrorCS"),sQuery(id+"F0.wireOp",EDGE,"E16.MirrorCS"),sQuery(id+"F0.wireOp",EDGE,"E17.MirrorCS"),sQuery(id+"F0.wireOp",EDGE,"E19.MirrorCS"),sQuery(id+"F0.wireOp",EDGE,"E20.MirrorC"),sQuery(id+"F0.wireOp",EDGE,"E21.MirrorC"),subQ3,subQ2,subQ1,subQ0,sQuery(id+"F0.wireOp",EDGE,"E25.bottom"),sQuery(id+"F0.wireOp",EDGE,"E25.top"),sQuery(id+"F0.wireOp",EDGE,"E25.left"),sQuery(id+"F0.wireOp",EDGE,"E25.right"),sQuery(id+"F0.wireOp",EDGE,"E26"),sQuery(id+"F0.wireOp",EDGE,"E27.trimOffspring"),sQuery(id+"F0.wireOp",EDGE,"E29"),sQuery(id+"F0.wireOp",EDGE,"E30.trimOffspring"),sQuery(id+"F0.wireOp",EDGE,"E32"),sQuery(id+"F0.wireOp",EDGE,"E33.trimOffspring"),sQuery(id+"F0.wireOp",EDGE,"E34"),sQuery(id+"F0.wireOp",EDGE,"E35.trimOffspring")])],"isStart":true}),makeQuery(id+"F2.opExtrude","CAP_FACE",FACE,{"disambiguationData":[OSD([subQ3,subQ2,subQ1,subQ0])],"isStart":true})]})});}
            var Q39;
            {var subQ0=sQuery(id+"F0.wireOp",EDGE,"E24.right");var subQ1=sQuery(id+"F0.wireOp",EDGE,"E24.left");var subQ2=sQuery(id+"F0.wireOp",EDGE,"E24.top");var subQ3=sQuery(id+"F0.wireOp",EDGE,"E24.bottom");Q39=makeQuery(id+"F4.boolean.opBoolean","SPLIT",FACE,{"disambiguationData":[TD([makeQuery(id+"F4.opExtrude","SWEPT_FACE",FACE,{"disambiguationData":[OSD([sQuery(id+"F3.wireOp",EDGE,"E41.2.0.14")])]})])],"derivedFrom":makeQuery(id+"F2.boolean.opBoolean","MERGE",FACE,{"derivedFrom":[makeQuery(id+"F1.opExtrude","CAP_FACE",FACE,{"disambiguationData":[OSD([sQuery(id+"F0.wireOp",EDGE,"E1"),sQuery(id+"F0.wireOp",EDGE,"E2.bottom"),sQuery(id+"F0.wireOp",EDGE,"E2.top"),sQuery(id+"F0.wireOp",EDGE,"E3"),sQuery(id+"F0.wireOp",EDGE,"E7.MirrorC"),sQuery(id+"F0.wireOp",EDGE,"E8.MirrorC"),sQuery(id+"F0.wireOp",EDGE,"E9.MirrorCS"),sQuery(id+"F0.wireOp",EDGE,"E11.MirrorCS"),sQuery(id+"F0.wireOp",EDGE,"E12.MirrorC"),sQuery(id+"F0.wireOp",EDGE,"E13.MirrorC"),sQuery(id+"F0.wireOp",EDGE,"E14.MirrorCS"),sQuery(id+"F0.wireOp",EDGE,"E16.MirrorCS"),sQuery(id+"F0.wireOp",EDGE,"E17.MirrorCS"),sQuery(id+"F0.wireOp",EDGE,"E19.MirrorCS"),sQuery(id+"F0.wireOp",EDGE,"E20.MirrorC"),sQuery(id+"F0.wireOp",EDGE,"E21.MirrorC"),subQ3,subQ2,subQ1,subQ0,sQuery(id+"F0.wireOp",EDGE,"E25.bottom"),sQuery(id+"F0.wireOp",EDGE,"E25.top"),sQuery(id+"F0.wireOp",EDGE,"E25.left"),sQuery(id+"F0.wireOp",EDGE,"E25.right"),sQuery(id+"F0.wireOp",EDGE,"E26"),sQuery(id+"F0.wireOp",EDGE,"E27.trimOffspring"),sQuery(id+"F0.wireOp",EDGE,"E29"),sQuery(id+"F0.wireOp",EDGE,"E30.trimOffspring"),sQuery(id+"F0.wireOp",EDGE,"E32"),sQuery(id+"F0.wireOp",EDGE,"E33.trimOffspring"),sQuery(id+"F0.wireOp",EDGE,"E34"),sQuery(id+"F0.wireOp",EDGE,"E35.trimOffspring")])],"isStart":true}),makeQuery(id+"F2.opExtrude","CAP_FACE",FACE,{"disambiguationData":[OSD([subQ3,subQ2,subQ1,subQ0])],"isStart":true})]})});}
            var Q40;
            {var subQ0=sQuery(id+"F0.wireOp",EDGE,"E24.right");var subQ1=sQuery(id+"F0.wireOp",EDGE,"E24.left");var subQ2=sQuery(id+"F0.wireOp",EDGE,"E24.top");var subQ3=sQuery(id+"F0.wireOp",EDGE,"E24.bottom");Q40=makeQuery(id+"F4.boolean.opBoolean","SPLIT",FACE,{"disambiguationData":[TD([makeQuery(id+"F4.opExtrude","SWEPT_FACE",FACE,{"disambiguationData":[OSD([sQuery(id+"F3.wireOp",EDGE,"E41.2.0.5")])]})])],"derivedFrom":makeQuery(id+"F2.boolean.opBoolean","MERGE",FACE,{"derivedFrom":[makeQuery(id+"F1.opExtrude","CAP_FACE",FACE,{"disambiguationData":[OSD([sQuery(id+"F0.wireOp",EDGE,"E1"),sQuery(id+"F0.wireOp",EDGE,"E2.bottom"),sQuery(id+"F0.wireOp",EDGE,"E2.top"),sQuery(id+"F0.wireOp",EDGE,"E3"),sQuery(id+"F0.wireOp",EDGE,"E7.MirrorC"),sQuery(id+"F0.wireOp",EDGE,"E8.MirrorC"),sQuery(id+"F0.wireOp",EDGE,"E9.MirrorCS"),sQuery(id+"F0.wireOp",EDGE,"E11.MirrorCS"),sQuery(id+"F0.wireOp",EDGE,"E12.MirrorC"),sQuery(id+"F0.wireOp",EDGE,"E13.MirrorC"),sQuery(id+"F0.wireOp",EDGE,"E14.MirrorCS"),sQuery(id+"F0.wireOp",EDGE,"E16.MirrorCS"),sQuery(id+"F0.wireOp",EDGE,"E17.MirrorCS"),sQuery(id+"F0.wireOp",EDGE,"E19.MirrorCS"),sQuery(id+"F0.wireOp",EDGE,"E20.MirrorC"),sQuery(id+"F0.wireOp",EDGE,"E21.MirrorC"),subQ3,subQ2,subQ1,subQ0,sQuery(id+"F0.wireOp",EDGE,"E25.bottom"),sQuery(id+"F0.wireOp",EDGE,"E25.top"),sQuery(id+"F0.wireOp",EDGE,"E25.left"),sQuery(id+"F0.wireOp",EDGE,"E25.right"),sQuery(id+"F0.wireOp",EDGE,"E26"),sQuery(id+"F0.wireOp",EDGE,"E27.trimOffspring"),sQuery(id+"F0.wireOp",EDGE,"E29"),sQuery(id+"F0.wireOp",EDGE,"E30.trimOffspring"),sQuery(id+"F0.wireOp",EDGE,"E32"),sQuery(id+"F0.wireOp",EDGE,"E33.trimOffspring"),sQuery(id+"F0.wireOp",EDGE,"E34"),sQuery(id+"F0.wireOp",EDGE,"E35.trimOffspring")])],"isStart":true}),makeQuery(id+"F2.opExtrude","CAP_FACE",FACE,{"disambiguationData":[OSD([subQ3,subQ2,subQ1,subQ0])],"isStart":true})]})});}
            var Q41;
            {var subQ0=sQuery(id+"F0.wireOp",EDGE,"E24.right");var subQ1=sQuery(id+"F0.wireOp",EDGE,"E24.left");var subQ2=sQuery(id+"F0.wireOp",EDGE,"E24.top");var subQ3=sQuery(id+"F0.wireOp",EDGE,"E24.bottom");Q41=makeQuery(id+"F4.boolean.opBoolean","SPLIT",FACE,{"disambiguationData":[TD([makeQuery(id+"F4.opExtrude","SWEPT_FACE",FACE,{"disambiguationData":[OSD([sQuery(id+"F3.wireOp",EDGE,"E41.2.0.4")])]})])],"derivedFrom":makeQuery(id+"F2.boolean.opBoolean","MERGE",FACE,{"derivedFrom":[makeQuery(id+"F1.opExtrude","CAP_FACE",FACE,{"disambiguationData":[OSD([sQuery(id+"F0.wireOp",EDGE,"E1"),sQuery(id+"F0.wireOp",EDGE,"E2.bottom"),sQuery(id+"F0.wireOp",EDGE,"E2.top"),sQuery(id+"F0.wireOp",EDGE,"E3"),sQuery(id+"F0.wireOp",EDGE,"E7.MirrorC"),sQuery(id+"F0.wireOp",EDGE,"E8.MirrorC"),sQuery(id+"F0.wireOp",EDGE,"E9.MirrorCS"),sQuery(id+"F0.wireOp",EDGE,"E11.MirrorCS"),sQuery(id+"F0.wireOp",EDGE,"E12.MirrorC"),sQuery(id+"F0.wireOp",EDGE,"E13.MirrorC"),sQuery(id+"F0.wireOp",EDGE,"E14.MirrorCS"),sQuery(id+"F0.wireOp",EDGE,"E16.MirrorCS"),sQuery(id+"F0.wireOp",EDGE,"E17.MirrorCS"),sQuery(id+"F0.wireOp",EDGE,"E19.MirrorCS"),sQuery(id+"F0.wireOp",EDGE,"E20.MirrorC"),sQuery(id+"F0.wireOp",EDGE,"E21.MirrorC"),subQ3,subQ2,subQ1,subQ0,sQuery(id+"F0.wireOp",EDGE,"E25.bottom"),sQuery(id+"F0.wireOp",EDGE,"E25.top"),sQuery(id+"F0.wireOp",EDGE,"E25.left"),sQuery(id+"F0.wireOp",EDGE,"E25.right"),sQuery(id+"F0.wireOp",EDGE,"E26"),sQuery(id+"F0.wireOp",EDGE,"E27.trimOffspring"),sQuery(id+"F0.wireOp",EDGE,"E29"),sQuery(id+"F0.wireOp",EDGE,"E30.trimOffspring"),sQuery(id+"F0.wireOp",EDGE,"E32"),sQuery(id+"F0.wireOp",EDGE,"E33.trimOffspring"),sQuery(id+"F0.wireOp",EDGE,"E34"),sQuery(id+"F0.wireOp",EDGE,"E35.trimOffspring")])],"isStart":true}),makeQuery(id+"F2.opExtrude","CAP_FACE",FACE,{"disambiguationData":[OSD([subQ3,subQ2,subQ1,subQ0])],"isStart":true})]})});}
            var Q42;
            {var subQ0=sQuery(id+"F0.wireOp",EDGE,"E24.right");var subQ1=sQuery(id+"F0.wireOp",EDGE,"E24.left");var subQ2=sQuery(id+"F0.wireOp",EDGE,"E24.top");var subQ3=sQuery(id+"F0.wireOp",EDGE,"E24.bottom");Q42=makeQuery(id+"F4.boolean.opBoolean","SPLIT",FACE,{"disambiguationData":[TD([makeQuery(id+"F4.opExtrude","SWEPT_FACE",FACE,{"disambiguationData":[OSD([sQuery(id+"F3.wireOp",EDGE,"E41.3.0.4")])]})])],"derivedFrom":makeQuery(id+"F2.boolean.opBoolean","MERGE",FACE,{"derivedFrom":[makeQuery(id+"F1.opExtrude","CAP_FACE",FACE,{"disambiguationData":[OSD([sQuery(id+"F0.wireOp",EDGE,"E1"),sQuery(id+"F0.wireOp",EDGE,"E2.bottom"),sQuery(id+"F0.wireOp",EDGE,"E2.top"),sQuery(id+"F0.wireOp",EDGE,"E3"),sQuery(id+"F0.wireOp",EDGE,"E7.MirrorC"),sQuery(id+"F0.wireOp",EDGE,"E8.MirrorC"),sQuery(id+"F0.wireOp",EDGE,"E9.MirrorCS"),sQuery(id+"F0.wireOp",EDGE,"E11.MirrorCS"),sQuery(id+"F0.wireOp",EDGE,"E12.MirrorC"),sQuery(id+"F0.wireOp",EDGE,"E13.MirrorC"),sQuery(id+"F0.wireOp",EDGE,"E14.MirrorCS"),sQuery(id+"F0.wireOp",EDGE,"E16.MirrorCS"),sQuery(id+"F0.wireOp",EDGE,"E17.MirrorCS"),sQuery(id+"F0.wireOp",EDGE,"E19.MirrorCS"),sQuery(id+"F0.wireOp",EDGE,"E20.MirrorC"),sQuery(id+"F0.wireOp",EDGE,"E21.MirrorC"),subQ3,subQ2,subQ1,subQ0,sQuery(id+"F0.wireOp",EDGE,"E25.bottom"),sQuery(id+"F0.wireOp",EDGE,"E25.top"),sQuery(id+"F0.wireOp",EDGE,"E25.left"),sQuery(id+"F0.wireOp",EDGE,"E25.right"),sQuery(id+"F0.wireOp",EDGE,"E26"),sQuery(id+"F0.wireOp",EDGE,"E27.trimOffspring"),sQuery(id+"F0.wireOp",EDGE,"E29"),sQuery(id+"F0.wireOp",EDGE,"E30.trimOffspring"),sQuery(id+"F0.wireOp",EDGE,"E32"),sQuery(id+"F0.wireOp",EDGE,"E33.trimOffspring"),sQuery(id+"F0.wireOp",EDGE,"E34"),sQuery(id+"F0.wireOp",EDGE,"E35.trimOffspring")])],"isStart":true}),makeQuery(id+"F2.opExtrude","CAP_FACE",FACE,{"disambiguationData":[OSD([subQ3,subQ2,subQ1,subQ0])],"isStart":true})]})});}
            var Q43;
            {var subQ0=sQuery(id+"F0.wireOp",EDGE,"E24.right");var subQ1=sQuery(id+"F0.wireOp",EDGE,"E24.left");var subQ2=sQuery(id+"F0.wireOp",EDGE,"E24.top");var subQ3=sQuery(id+"F0.wireOp",EDGE,"E24.bottom");Q43=makeQuery(id+"F4.boolean.opBoolean","SPLIT",FACE,{"disambiguationData":[TD([makeQuery(id+"F4.opExtrude","SWEPT_FACE",FACE,{"disambiguationData":[OSD([sQuery(id+"F3.wireOp",EDGE,"E41.3.0.5")])]})])],"derivedFrom":makeQuery(id+"F2.boolean.opBoolean","MERGE",FACE,{"derivedFrom":[makeQuery(id+"F1.opExtrude","CAP_FACE",FACE,{"disambiguationData":[OSD([sQuery(id+"F0.wireOp",EDGE,"E1"),sQuery(id+"F0.wireOp",EDGE,"E2.bottom"),sQuery(id+"F0.wireOp",EDGE,"E2.top"),sQuery(id+"F0.wireOp",EDGE,"E3"),sQuery(id+"F0.wireOp",EDGE,"E7.MirrorC"),sQuery(id+"F0.wireOp",EDGE,"E8.MirrorC"),sQuery(id+"F0.wireOp",EDGE,"E9.MirrorCS"),sQuery(id+"F0.wireOp",EDGE,"E11.MirrorCS"),sQuery(id+"F0.wireOp",EDGE,"E12.MirrorC"),sQuery(id+"F0.wireOp",EDGE,"E13.MirrorC"),sQuery(id+"F0.wireOp",EDGE,"E14.MirrorCS"),sQuery(id+"F0.wireOp",EDGE,"E16.MirrorCS"),sQuery(id+"F0.wireOp",EDGE,"E17.MirrorCS"),sQuery(id+"F0.wireOp",EDGE,"E19.MirrorCS"),sQuery(id+"F0.wireOp",EDGE,"E20.MirrorC"),sQuery(id+"F0.wireOp",EDGE,"E21.MirrorC"),subQ3,subQ2,subQ1,subQ0,sQuery(id+"F0.wireOp",EDGE,"E25.bottom"),sQuery(id+"F0.wireOp",EDGE,"E25.top"),sQuery(id+"F0.wireOp",EDGE,"E25.left"),sQuery(id+"F0.wireOp",EDGE,"E25.right"),sQuery(id+"F0.wireOp",EDGE,"E26"),sQuery(id+"F0.wireOp",EDGE,"E27.trimOffspring"),sQuery(id+"F0.wireOp",EDGE,"E29"),sQuery(id+"F0.wireOp",EDGE,"E30.trimOffspring"),sQuery(id+"F0.wireOp",EDGE,"E32"),sQuery(id+"F0.wireOp",EDGE,"E33.trimOffspring"),sQuery(id+"F0.wireOp",EDGE,"E34"),sQuery(id+"F0.wireOp",EDGE,"E35.trimOffspring")])],"isStart":true}),makeQuery(id+"F2.opExtrude","CAP_FACE",FACE,{"disambiguationData":[OSD([subQ3,subQ2,subQ1,subQ0])],"isStart":true})]})});}
            var Q44;
            {var subQ0=sQuery(id+"F0.wireOp",EDGE,"E24.right");var subQ1=sQuery(id+"F0.wireOp",EDGE,"E24.left");var subQ2=sQuery(id+"F0.wireOp",EDGE,"E24.top");var subQ3=sQuery(id+"F0.wireOp",EDGE,"E24.bottom");Q44=makeQuery(id+"F4.boolean.opBoolean","SPLIT",FACE,{"disambiguationData":[TD([makeQuery(id+"F4.opExtrude","SWEPT_FACE",FACE,{"disambiguationData":[OSD([sQuery(id+"F3.wireOp",EDGE,"E41.3.0.14")])]})])],"derivedFrom":makeQuery(id+"F2.boolean.opBoolean","MERGE",FACE,{"derivedFrom":[makeQuery(id+"F1.opExtrude","CAP_FACE",FACE,{"disambiguationData":[OSD([sQuery(id+"F0.wireOp",EDGE,"E1"),sQuery(id+"F0.wireOp",EDGE,"E2.bottom"),sQuery(id+"F0.wireOp",EDGE,"E2.top"),sQuery(id+"F0.wireOp",EDGE,"E3"),sQuery(id+"F0.wireOp",EDGE,"E7.MirrorC"),sQuery(id+"F0.wireOp",EDGE,"E8.MirrorC"),sQuery(id+"F0.wireOp",EDGE,"E9.MirrorCS"),sQuery(id+"F0.wireOp",EDGE,"E11.MirrorCS"),sQuery(id+"F0.wireOp",EDGE,"E12.MirrorC"),sQuery(id+"F0.wireOp",EDGE,"E13.MirrorC"),sQuery(id+"F0.wireOp",EDGE,"E14.MirrorCS"),sQuery(id+"F0.wireOp",EDGE,"E16.MirrorCS"),sQuery(id+"F0.wireOp",EDGE,"E17.MirrorCS"),sQuery(id+"F0.wireOp",EDGE,"E19.MirrorCS"),sQuery(id+"F0.wireOp",EDGE,"E20.MirrorC"),sQuery(id+"F0.wireOp",EDGE,"E21.MirrorC"),subQ3,subQ2,subQ1,subQ0,sQuery(id+"F0.wireOp",EDGE,"E25.bottom"),sQuery(id+"F0.wireOp",EDGE,"E25.top"),sQuery(id+"F0.wireOp",EDGE,"E25.left"),sQuery(id+"F0.wireOp",EDGE,"E25.right"),sQuery(id+"F0.wireOp",EDGE,"E26"),sQuery(id+"F0.wireOp",EDGE,"E27.trimOffspring"),sQuery(id+"F0.wireOp",EDGE,"E29"),sQuery(id+"F0.wireOp",EDGE,"E30.trimOffspring"),sQuery(id+"F0.wireOp",EDGE,"E32"),sQuery(id+"F0.wireOp",EDGE,"E33.trimOffspring"),sQuery(id+"F0.wireOp",EDGE,"E34"),sQuery(id+"F0.wireOp",EDGE,"E35.trimOffspring")])],"isStart":true}),makeQuery(id+"F2.opExtrude","CAP_FACE",FACE,{"disambiguationData":[OSD([subQ3,subQ2,subQ1,subQ0])],"isStart":true})]})});}
            var Q45;
            {var subQ0=sQuery(id+"F0.wireOp",EDGE,"E24.right");var subQ1=sQuery(id+"F0.wireOp",EDGE,"E24.left");var subQ2=sQuery(id+"F0.wireOp",EDGE,"E24.top");var subQ3=sQuery(id+"F0.wireOp",EDGE,"E24.bottom");Q45=makeQuery(id+"F4.boolean.opBoolean","SPLIT",FACE,{"disambiguationData":[TD([makeQuery(id+"F4.opExtrude","SWEPT_FACE",FACE,{"disambiguationData":[OSD([sQuery(id+"F3.wireOp",EDGE,"E41.3.0.3")])]})])],"derivedFrom":makeQuery(id+"F2.boolean.opBoolean","MERGE",FACE,{"derivedFrom":[makeQuery(id+"F1.opExtrude","CAP_FACE",FACE,{"disambiguationData":[OSD([sQuery(id+"F0.wireOp",EDGE,"E1"),sQuery(id+"F0.wireOp",EDGE,"E2.bottom"),sQuery(id+"F0.wireOp",EDGE,"E2.top"),sQuery(id+"F0.wireOp",EDGE,"E3"),sQuery(id+"F0.wireOp",EDGE,"E7.MirrorC"),sQuery(id+"F0.wireOp",EDGE,"E8.MirrorC"),sQuery(id+"F0.wireOp",EDGE,"E9.MirrorCS"),sQuery(id+"F0.wireOp",EDGE,"E11.MirrorCS"),sQuery(id+"F0.wireOp",EDGE,"E12.MirrorC"),sQuery(id+"F0.wireOp",EDGE,"E13.MirrorC"),sQuery(id+"F0.wireOp",EDGE,"E14.MirrorCS"),sQuery(id+"F0.wireOp",EDGE,"E16.MirrorCS"),sQuery(id+"F0.wireOp",EDGE,"E17.MirrorCS"),sQuery(id+"F0.wireOp",EDGE,"E19.MirrorCS"),sQuery(id+"F0.wireOp",EDGE,"E20.MirrorC"),sQuery(id+"F0.wireOp",EDGE,"E21.MirrorC"),subQ3,subQ2,subQ1,subQ0,sQuery(id+"F0.wireOp",EDGE,"E25.bottom"),sQuery(id+"F0.wireOp",EDGE,"E25.top"),sQuery(id+"F0.wireOp",EDGE,"E25.left"),sQuery(id+"F0.wireOp",EDGE,"E25.right"),sQuery(id+"F0.wireOp",EDGE,"E26"),sQuery(id+"F0.wireOp",EDGE,"E27.trimOffspring"),sQuery(id+"F0.wireOp",EDGE,"E29"),sQuery(id+"F0.wireOp",EDGE,"E30.trimOffspring"),sQuery(id+"F0.wireOp",EDGE,"E32"),sQuery(id+"F0.wireOp",EDGE,"E33.trimOffspring"),sQuery(id+"F0.wireOp",EDGE,"E34"),sQuery(id+"F0.wireOp",EDGE,"E35.trimOffspring")])],"isStart":true}),makeQuery(id+"F2.opExtrude","CAP_FACE",FACE,{"disambiguationData":[OSD([subQ3,subQ2,subQ1,subQ0])],"isStart":true})]})});}
            var Q46;
            {var subQ0=sQuery(id+"F0.wireOp",EDGE,"E24.right");var subQ1=sQuery(id+"F0.wireOp",EDGE,"E24.left");var subQ2=sQuery(id+"F0.wireOp",EDGE,"E24.top");var subQ3=sQuery(id+"F0.wireOp",EDGE,"E24.bottom");Q46=makeQuery(id+"F4.boolean.opBoolean","SPLIT",FACE,{"disambiguationData":[TD([makeQuery(id+"F4.opExtrude","SWEPT_FACE",FACE,{"disambiguationData":[OSD([sQuery(id+"F3.wireOp",EDGE,"E41.3.0.12")])]})])],"derivedFrom":makeQuery(id+"F2.boolean.opBoolean","MERGE",FACE,{"derivedFrom":[makeQuery(id+"F1.opExtrude","CAP_FACE",FACE,{"disambiguationData":[OSD([sQuery(id+"F0.wireOp",EDGE,"E1"),sQuery(id+"F0.wireOp",EDGE,"E2.bottom"),sQuery(id+"F0.wireOp",EDGE,"E2.top"),sQuery(id+"F0.wireOp",EDGE,"E3"),sQuery(id+"F0.wireOp",EDGE,"E7.MirrorC"),sQuery(id+"F0.wireOp",EDGE,"E8.MirrorC"),sQuery(id+"F0.wireOp",EDGE,"E9.MirrorCS"),sQuery(id+"F0.wireOp",EDGE,"E11.MirrorCS"),sQuery(id+"F0.wireOp",EDGE,"E12.MirrorC"),sQuery(id+"F0.wireOp",EDGE,"E13.MirrorC"),sQuery(id+"F0.wireOp",EDGE,"E14.MirrorCS"),sQuery(id+"F0.wireOp",EDGE,"E16.MirrorCS"),sQuery(id+"F0.wireOp",EDGE,"E17.MirrorCS"),sQuery(id+"F0.wireOp",EDGE,"E19.MirrorCS"),sQuery(id+"F0.wireOp",EDGE,"E20.MirrorC"),sQuery(id+"F0.wireOp",EDGE,"E21.MirrorC"),subQ3,subQ2,subQ1,subQ0,sQuery(id+"F0.wireOp",EDGE,"E25.bottom"),sQuery(id+"F0.wireOp",EDGE,"E25.top"),sQuery(id+"F0.wireOp",EDGE,"E25.left"),sQuery(id+"F0.wireOp",EDGE,"E25.right"),sQuery(id+"F0.wireOp",EDGE,"E26"),sQuery(id+"F0.wireOp",EDGE,"E27.trimOffspring"),sQuery(id+"F0.wireOp",EDGE,"E29"),sQuery(id+"F0.wireOp",EDGE,"E30.trimOffspring"),sQuery(id+"F0.wireOp",EDGE,"E32"),sQuery(id+"F0.wireOp",EDGE,"E33.trimOffspring"),sQuery(id+"F0.wireOp",EDGE,"E34"),sQuery(id+"F0.wireOp",EDGE,"E35.trimOffspring")])],"isStart":true}),makeQuery(id+"F2.opExtrude","CAP_FACE",FACE,{"disambiguationData":[OSD([subQ3,subQ2,subQ1,subQ0])],"isStart":true})]})});}
            var Q47;
            {var subQ0=sQuery(id+"F0.wireOp",EDGE,"E24.right");var subQ1=sQuery(id+"F0.wireOp",EDGE,"E24.left");var subQ2=sQuery(id+"F0.wireOp",EDGE,"E24.top");var subQ3=sQuery(id+"F0.wireOp",EDGE,"E24.bottom");Q47=makeQuery(id+"F4.boolean.opBoolean","SPLIT",FACE,{"disambiguationData":[TD([makeQuery(id+"F4.opExtrude","SWEPT_FACE",FACE,{"disambiguationData":[OSD([sQuery(id+"F3.wireOp",EDGE,"E41.3.0.6")])]})])],"derivedFrom":makeQuery(id+"F2.boolean.opBoolean","MERGE",FACE,{"derivedFrom":[makeQuery(id+"F1.opExtrude","CAP_FACE",FACE,{"disambiguationData":[OSD([sQuery(id+"F0.wireOp",EDGE,"E1"),sQuery(id+"F0.wireOp",EDGE,"E2.bottom"),sQuery(id+"F0.wireOp",EDGE,"E2.top"),sQuery(id+"F0.wireOp",EDGE,"E3"),sQuery(id+"F0.wireOp",EDGE,"E7.MirrorC"),sQuery(id+"F0.wireOp",EDGE,"E8.MirrorC"),sQuery(id+"F0.wireOp",EDGE,"E9.MirrorCS"),sQuery(id+"F0.wireOp",EDGE,"E11.MirrorCS"),sQuery(id+"F0.wireOp",EDGE,"E12.MirrorC"),sQuery(id+"F0.wireOp",EDGE,"E13.MirrorC"),sQuery(id+"F0.wireOp",EDGE,"E14.MirrorCS"),sQuery(id+"F0.wireOp",EDGE,"E16.MirrorCS"),sQuery(id+"F0.wireOp",EDGE,"E17.MirrorCS"),sQuery(id+"F0.wireOp",EDGE,"E19.MirrorCS"),sQuery(id+"F0.wireOp",EDGE,"E20.MirrorC"),sQuery(id+"F0.wireOp",EDGE,"E21.MirrorC"),subQ3,subQ2,subQ1,subQ0,sQuery(id+"F0.wireOp",EDGE,"E25.bottom"),sQuery(id+"F0.wireOp",EDGE,"E25.top"),sQuery(id+"F0.wireOp",EDGE,"E25.left"),sQuery(id+"F0.wireOp",EDGE,"E25.right"),sQuery(id+"F0.wireOp",EDGE,"E26"),sQuery(id+"F0.wireOp",EDGE,"E27.trimOffspring"),sQuery(id+"F0.wireOp",EDGE,"E29"),sQuery(id+"F0.wireOp",EDGE,"E30.trimOffspring"),sQuery(id+"F0.wireOp",EDGE,"E32"),sQuery(id+"F0.wireOp",EDGE,"E33.trimOffspring"),sQuery(id+"F0.wireOp",EDGE,"E34"),sQuery(id+"F0.wireOp",EDGE,"E35.trimOffspring")])],"isStart":true}),makeQuery(id+"F2.opExtrude","CAP_FACE",FACE,{"disambiguationData":[OSD([subQ3,subQ2,subQ1,subQ0])],"isStart":true})]})});}
            var Q48;
            {var subQ0=sQuery(id+"F0.wireOp",EDGE,"E24.right");var subQ1=sQuery(id+"F0.wireOp",EDGE,"E24.left");var subQ2=sQuery(id+"F0.wireOp",EDGE,"E24.top");var subQ3=sQuery(id+"F0.wireOp",EDGE,"E24.bottom");Q48=makeQuery(id+"F4.boolean.opBoolean","SPLIT",FACE,{"disambiguationData":[TD([makeQuery(id+"F4.opExtrude","SWEPT_FACE",FACE,{"disambiguationData":[OSD([sQuery(id+"F3.wireOp",EDGE,"E41.3.0.2")])]})])],"derivedFrom":makeQuery(id+"F2.boolean.opBoolean","MERGE",FACE,{"derivedFrom":[makeQuery(id+"F1.opExtrude","CAP_FACE",FACE,{"disambiguationData":[OSD([sQuery(id+"F0.wireOp",EDGE,"E1"),sQuery(id+"F0.wireOp",EDGE,"E2.bottom"),sQuery(id+"F0.wireOp",EDGE,"E2.top"),sQuery(id+"F0.wireOp",EDGE,"E3"),sQuery(id+"F0.wireOp",EDGE,"E7.MirrorC"),sQuery(id+"F0.wireOp",EDGE,"E8.MirrorC"),sQuery(id+"F0.wireOp",EDGE,"E9.MirrorCS"),sQuery(id+"F0.wireOp",EDGE,"E11.MirrorCS"),sQuery(id+"F0.wireOp",EDGE,"E12.MirrorC"),sQuery(id+"F0.wireOp",EDGE,"E13.MirrorC"),sQuery(id+"F0.wireOp",EDGE,"E14.MirrorCS"),sQuery(id+"F0.wireOp",EDGE,"E16.MirrorCS"),sQuery(id+"F0.wireOp",EDGE,"E17.MirrorCS"),sQuery(id+"F0.wireOp",EDGE,"E19.MirrorCS"),sQuery(id+"F0.wireOp",EDGE,"E20.MirrorC"),sQuery(id+"F0.wireOp",EDGE,"E21.MirrorC"),subQ3,subQ2,subQ1,subQ0,sQuery(id+"F0.wireOp",EDGE,"E25.bottom"),sQuery(id+"F0.wireOp",EDGE,"E25.top"),sQuery(id+"F0.wireOp",EDGE,"E25.left"),sQuery(id+"F0.wireOp",EDGE,"E25.right"),sQuery(id+"F0.wireOp",EDGE,"E26"),sQuery(id+"F0.wireOp",EDGE,"E27.trimOffspring"),sQuery(id+"F0.wireOp",EDGE,"E29"),sQuery(id+"F0.wireOp",EDGE,"E30.trimOffspring"),sQuery(id+"F0.wireOp",EDGE,"E32"),sQuery(id+"F0.wireOp",EDGE,"E33.trimOffspring"),sQuery(id+"F0.wireOp",EDGE,"E34"),sQuery(id+"F0.wireOp",EDGE,"E35.trimOffspring")])],"isStart":true}),makeQuery(id+"F2.opExtrude","CAP_FACE",FACE,{"disambiguationData":[OSD([subQ3,subQ2,subQ1,subQ0])],"isStart":true})]})});}
            var Q49;
            {var subQ0=sQuery(id+"F0.wireOp",EDGE,"E24.right");var subQ1=sQuery(id+"F0.wireOp",EDGE,"E24.left");var subQ2=sQuery(id+"F0.wireOp",EDGE,"E24.top");var subQ3=sQuery(id+"F0.wireOp",EDGE,"E24.bottom");Q49=makeQuery(id+"F4.boolean.opBoolean","SPLIT",FACE,{"disambiguationData":[TD([makeQuery(id+"F4.opExtrude","SWEPT_FACE",FACE,{"disambiguationData":[OSD([sQuery(id+"F3.wireOp",EDGE,"E41.3.0.11")])]})])],"derivedFrom":makeQuery(id+"F2.boolean.opBoolean","MERGE",FACE,{"derivedFrom":[makeQuery(id+"F1.opExtrude","CAP_FACE",FACE,{"disambiguationData":[OSD([sQuery(id+"F0.wireOp",EDGE,"E1"),sQuery(id+"F0.wireOp",EDGE,"E2.bottom"),sQuery(id+"F0.wireOp",EDGE,"E2.top"),sQuery(id+"F0.wireOp",EDGE,"E3"),sQuery(id+"F0.wireOp",EDGE,"E7.MirrorC"),sQuery(id+"F0.wireOp",EDGE,"E8.MirrorC"),sQuery(id+"F0.wireOp",EDGE,"E9.MirrorCS"),sQuery(id+"F0.wireOp",EDGE,"E11.MirrorCS"),sQuery(id+"F0.wireOp",EDGE,"E12.MirrorC"),sQuery(id+"F0.wireOp",EDGE,"E13.MirrorC"),sQuery(id+"F0.wireOp",EDGE,"E14.MirrorCS"),sQuery(id+"F0.wireOp",EDGE,"E16.MirrorCS"),sQuery(id+"F0.wireOp",EDGE,"E17.MirrorCS"),sQuery(id+"F0.wireOp",EDGE,"E19.MirrorCS"),sQuery(id+"F0.wireOp",EDGE,"E20.MirrorC"),sQuery(id+"F0.wireOp",EDGE,"E21.MirrorC"),subQ3,subQ2,subQ1,subQ0,sQuery(id+"F0.wireOp",EDGE,"E25.bottom"),sQuery(id+"F0.wireOp",EDGE,"E25.top"),sQuery(id+"F0.wireOp",EDGE,"E25.left"),sQuery(id+"F0.wireOp",EDGE,"E25.right"),sQuery(id+"F0.wireOp",EDGE,"E26"),sQuery(id+"F0.wireOp",EDGE,"E27.trimOffspring"),sQuery(id+"F0.wireOp",EDGE,"E29"),sQuery(id+"F0.wireOp",EDGE,"E30.trimOffspring"),sQuery(id+"F0.wireOp",EDGE,"E32"),sQuery(id+"F0.wireOp",EDGE,"E33.trimOffspring"),sQuery(id+"F0.wireOp",EDGE,"E34"),sQuery(id+"F0.wireOp",EDGE,"E35.trimOffspring")])],"isStart":true}),makeQuery(id+"F2.opExtrude","CAP_FACE",FACE,{"disambiguationData":[OSD([subQ3,subQ2,subQ1,subQ0])],"isStart":true})]})});}
            var Q50;
            {var subQ0=sQuery(id+"F0.wireOp",EDGE,"E24.right");var subQ1=sQuery(id+"F0.wireOp",EDGE,"E24.left");var subQ2=sQuery(id+"F0.wireOp",EDGE,"E24.top");var subQ3=sQuery(id+"F0.wireOp",EDGE,"E24.bottom");Q50=makeQuery(id+"F4.boolean.opBoolean","SPLIT",FACE,{"disambiguationData":[TD([makeQuery(id+"F4.opExtrude","SWEPT_FACE",FACE,{"disambiguationData":[OSD([sQuery(id+"F3.wireOp",EDGE,"E41.3.0.0")])]})])],"derivedFrom":makeQuery(id+"F2.boolean.opBoolean","MERGE",FACE,{"derivedFrom":[makeQuery(id+"F1.opExtrude","CAP_FACE",FACE,{"disambiguationData":[OSD([sQuery(id+"F0.wireOp",EDGE,"E1"),sQuery(id+"F0.wireOp",EDGE,"E2.bottom"),sQuery(id+"F0.wireOp",EDGE,"E2.top"),sQuery(id+"F0.wireOp",EDGE,"E3"),sQuery(id+"F0.wireOp",EDGE,"E7.MirrorC"),sQuery(id+"F0.wireOp",EDGE,"E8.MirrorC"),sQuery(id+"F0.wireOp",EDGE,"E9.MirrorCS"),sQuery(id+"F0.wireOp",EDGE,"E11.MirrorCS"),sQuery(id+"F0.wireOp",EDGE,"E12.MirrorC"),sQuery(id+"F0.wireOp",EDGE,"E13.MirrorC"),sQuery(id+"F0.wireOp",EDGE,"E14.MirrorCS"),sQuery(id+"F0.wireOp",EDGE,"E16.MirrorCS"),sQuery(id+"F0.wireOp",EDGE,"E17.MirrorCS"),sQuery(id+"F0.wireOp",EDGE,"E19.MirrorCS"),sQuery(id+"F0.wireOp",EDGE,"E20.MirrorC"),sQuery(id+"F0.wireOp",EDGE,"E21.MirrorC"),subQ3,subQ2,subQ1,subQ0,sQuery(id+"F0.wireOp",EDGE,"E25.bottom"),sQuery(id+"F0.wireOp",EDGE,"E25.top"),sQuery(id+"F0.wireOp",EDGE,"E25.left"),sQuery(id+"F0.wireOp",EDGE,"E25.right"),sQuery(id+"F0.wireOp",EDGE,"E26"),sQuery(id+"F0.wireOp",EDGE,"E27.trimOffspring"),sQuery(id+"F0.wireOp",EDGE,"E29"),sQuery(id+"F0.wireOp",EDGE,"E30.trimOffspring"),sQuery(id+"F0.wireOp",EDGE,"E32"),sQuery(id+"F0.wireOp",EDGE,"E33.trimOffspring"),sQuery(id+"F0.wireOp",EDGE,"E34"),sQuery(id+"F0.wireOp",EDGE,"E35.trimOffspring")])],"isStart":true}),makeQuery(id+"F2.opExtrude","CAP_FACE",FACE,{"disambiguationData":[OSD([subQ3,subQ2,subQ1,subQ0])],"isStart":true})]})});}
            var Q51;
            {var subQ0=sQuery(id+"F0.wireOp",EDGE,"E24.right");var subQ1=sQuery(id+"F0.wireOp",EDGE,"E24.left");var subQ2=sQuery(id+"F0.wireOp",EDGE,"E24.top");var subQ3=sQuery(id+"F0.wireOp",EDGE,"E24.bottom");Q51=makeQuery(id+"F4.boolean.opBoolean","SPLIT",FACE,{"disambiguationData":[TD([makeQuery(id+"F4.opExtrude","SWEPT_FACE",FACE,{"disambiguationData":[OSD([sQuery(id+"F3.wireOp",EDGE,"E41.3.0.7")])]})])],"derivedFrom":makeQuery(id+"F2.boolean.opBoolean","MERGE",FACE,{"derivedFrom":[makeQuery(id+"F1.opExtrude","CAP_FACE",FACE,{"disambiguationData":[OSD([sQuery(id+"F0.wireOp",EDGE,"E1"),sQuery(id+"F0.wireOp",EDGE,"E2.bottom"),sQuery(id+"F0.wireOp",EDGE,"E2.top"),sQuery(id+"F0.wireOp",EDGE,"E3"),sQuery(id+"F0.wireOp",EDGE,"E7.MirrorC"),sQuery(id+"F0.wireOp",EDGE,"E8.MirrorC"),sQuery(id+"F0.wireOp",EDGE,"E9.MirrorCS"),sQuery(id+"F0.wireOp",EDGE,"E11.MirrorCS"),sQuery(id+"F0.wireOp",EDGE,"E12.MirrorC"),sQuery(id+"F0.wireOp",EDGE,"E13.MirrorC"),sQuery(id+"F0.wireOp",EDGE,"E14.MirrorCS"),sQuery(id+"F0.wireOp",EDGE,"E16.MirrorCS"),sQuery(id+"F0.wireOp",EDGE,"E17.MirrorCS"),sQuery(id+"F0.wireOp",EDGE,"E19.MirrorCS"),sQuery(id+"F0.wireOp",EDGE,"E20.MirrorC"),sQuery(id+"F0.wireOp",EDGE,"E21.MirrorC"),subQ3,subQ2,subQ1,subQ0,sQuery(id+"F0.wireOp",EDGE,"E25.bottom"),sQuery(id+"F0.wireOp",EDGE,"E25.top"),sQuery(id+"F0.wireOp",EDGE,"E25.left"),sQuery(id+"F0.wireOp",EDGE,"E25.right"),sQuery(id+"F0.wireOp",EDGE,"E26"),sQuery(id+"F0.wireOp",EDGE,"E27.trimOffspring"),sQuery(id+"F0.wireOp",EDGE,"E29"),sQuery(id+"F0.wireOp",EDGE,"E30.trimOffspring"),sQuery(id+"F0.wireOp",EDGE,"E32"),sQuery(id+"F0.wireOp",EDGE,"E33.trimOffspring"),sQuery(id+"F0.wireOp",EDGE,"E34"),sQuery(id+"F0.wireOp",EDGE,"E35.trimOffspring")])],"isStart":true}),makeQuery(id+"F2.opExtrude","CAP_FACE",FACE,{"disambiguationData":[OSD([subQ3,subQ2,subQ1,subQ0])],"isStart":true})]})});}
            var Q52;
            {var subQ0=sQuery(id+"F0.wireOp",EDGE,"E24.right");var subQ1=sQuery(id+"F0.wireOp",EDGE,"E24.left");var subQ2=sQuery(id+"F0.wireOp",EDGE,"E24.top");var subQ3=sQuery(id+"F0.wireOp",EDGE,"E24.bottom");Q52=makeQuery(id+"F4.boolean.opBoolean","SPLIT",FACE,{"disambiguationData":[TD([makeQuery(id+"F4.opExtrude","SWEPT_FACE",FACE,{"disambiguationData":[OSD([sQuery(id+"F3.wireOp",EDGE,"E41.3.0.8")])]})])],"derivedFrom":makeQuery(id+"F2.boolean.opBoolean","MERGE",FACE,{"derivedFrom":[makeQuery(id+"F1.opExtrude","CAP_FACE",FACE,{"disambiguationData":[OSD([sQuery(id+"F0.wireOp",EDGE,"E1"),sQuery(id+"F0.wireOp",EDGE,"E2.bottom"),sQuery(id+"F0.wireOp",EDGE,"E2.top"),sQuery(id+"F0.wireOp",EDGE,"E3"),sQuery(id+"F0.wireOp",EDGE,"E7.MirrorC"),sQuery(id+"F0.wireOp",EDGE,"E8.MirrorC"),sQuery(id+"F0.wireOp",EDGE,"E9.MirrorCS"),sQuery(id+"F0.wireOp",EDGE,"E11.MirrorCS"),sQuery(id+"F0.wireOp",EDGE,"E12.MirrorC"),sQuery(id+"F0.wireOp",EDGE,"E13.MirrorC"),sQuery(id+"F0.wireOp",EDGE,"E14.MirrorCS"),sQuery(id+"F0.wireOp",EDGE,"E16.MirrorCS"),sQuery(id+"F0.wireOp",EDGE,"E17.MirrorCS"),sQuery(id+"F0.wireOp",EDGE,"E19.MirrorCS"),sQuery(id+"F0.wireOp",EDGE,"E20.MirrorC"),sQuery(id+"F0.wireOp",EDGE,"E21.MirrorC"),subQ3,subQ2,subQ1,subQ0,sQuery(id+"F0.wireOp",EDGE,"E25.bottom"),sQuery(id+"F0.wireOp",EDGE,"E25.top"),sQuery(id+"F0.wireOp",EDGE,"E25.left"),sQuery(id+"F0.wireOp",EDGE,"E25.right"),sQuery(id+"F0.wireOp",EDGE,"E26"),sQuery(id+"F0.wireOp",EDGE,"E27.trimOffspring"),sQuery(id+"F0.wireOp",EDGE,"E29"),sQuery(id+"F0.wireOp",EDGE,"E30.trimOffspring"),sQuery(id+"F0.wireOp",EDGE,"E32"),sQuery(id+"F0.wireOp",EDGE,"E33.trimOffspring"),sQuery(id+"F0.wireOp",EDGE,"E34"),sQuery(id+"F0.wireOp",EDGE,"E35.trimOffspring")])],"isStart":true}),makeQuery(id+"F2.opExtrude","CAP_FACE",FACE,{"disambiguationData":[OSD([subQ3,subQ2,subQ1,subQ0])],"isStart":true})]})});}
            var Q53;
            {var subQ0=sQuery(id+"F0.wireOp",EDGE,"E24.right");var subQ1=sQuery(id+"F0.wireOp",EDGE,"E24.left");var subQ2=sQuery(id+"F0.wireOp",EDGE,"E24.top");var subQ3=sQuery(id+"F0.wireOp",EDGE,"E24.bottom");Q53=makeQuery(id+"F4.boolean.opBoolean","SPLIT",FACE,{"disambiguationData":[TD([makeQuery(id+"F4.opExtrude","SWEPT_FACE",FACE,{"disambiguationData":[OSD([sQuery(id+"F3.wireOp",EDGE,"E41.3.0.9")])]})])],"derivedFrom":makeQuery(id+"F2.boolean.opBoolean","MERGE",FACE,{"derivedFrom":[makeQuery(id+"F1.opExtrude","CAP_FACE",FACE,{"disambiguationData":[OSD([sQuery(id+"F0.wireOp",EDGE,"E1"),sQuery(id+"F0.wireOp",EDGE,"E2.bottom"),sQuery(id+"F0.wireOp",EDGE,"E2.top"),sQuery(id+"F0.wireOp",EDGE,"E3"),sQuery(id+"F0.wireOp",EDGE,"E7.MirrorC"),sQuery(id+"F0.wireOp",EDGE,"E8.MirrorC"),sQuery(id+"F0.wireOp",EDGE,"E9.MirrorCS"),sQuery(id+"F0.wireOp",EDGE,"E11.MirrorCS"),sQuery(id+"F0.wireOp",EDGE,"E12.MirrorC"),sQuery(id+"F0.wireOp",EDGE,"E13.MirrorC"),sQuery(id+"F0.wireOp",EDGE,"E14.MirrorCS"),sQuery(id+"F0.wireOp",EDGE,"E16.MirrorCS"),sQuery(id+"F0.wireOp",EDGE,"E17.MirrorCS"),sQuery(id+"F0.wireOp",EDGE,"E19.MirrorCS"),sQuery(id+"F0.wireOp",EDGE,"E20.MirrorC"),sQuery(id+"F0.wireOp",EDGE,"E21.MirrorC"),subQ3,subQ2,subQ1,subQ0,sQuery(id+"F0.wireOp",EDGE,"E25.bottom"),sQuery(id+"F0.wireOp",EDGE,"E25.top"),sQuery(id+"F0.wireOp",EDGE,"E25.left"),sQuery(id+"F0.wireOp",EDGE,"E25.right"),sQuery(id+"F0.wireOp",EDGE,"E26"),sQuery(id+"F0.wireOp",EDGE,"E27.trimOffspring"),sQuery(id+"F0.wireOp",EDGE,"E29"),sQuery(id+"F0.wireOp",EDGE,"E30.trimOffspring"),sQuery(id+"F0.wireOp",EDGE,"E32"),sQuery(id+"F0.wireOp",EDGE,"E33.trimOffspring"),sQuery(id+"F0.wireOp",EDGE,"E34"),sQuery(id+"F0.wireOp",EDGE,"E35.trimOffspring")])],"isStart":true}),makeQuery(id+"F2.opExtrude","CAP_FACE",FACE,{"disambiguationData":[OSD([subQ3,subQ2,subQ1,subQ0])],"isStart":true})]})});}
            var Q54;
            {var subQ0=sQuery(id+"F0.wireOp",EDGE,"E24.right");var subQ1=sQuery(id+"F0.wireOp",EDGE,"E24.left");var subQ2=sQuery(id+"F0.wireOp",EDGE,"E24.top");var subQ3=sQuery(id+"F0.wireOp",EDGE,"E24.bottom");Q54=makeQuery(id+"F4.boolean.opBoolean","SPLIT",FACE,{"disambiguationData":[TD([makeQuery(id+"F4.opExtrude","SWEPT_FACE",FACE,{"disambiguationData":[OSD([sQuery(id+"F3.wireOp",EDGE,"E41.3.0.10")])]})])],"derivedFrom":makeQuery(id+"F2.boolean.opBoolean","MERGE",FACE,{"derivedFrom":[makeQuery(id+"F1.opExtrude","CAP_FACE",FACE,{"disambiguationData":[OSD([sQuery(id+"F0.wireOp",EDGE,"E1"),sQuery(id+"F0.wireOp",EDGE,"E2.bottom"),sQuery(id+"F0.wireOp",EDGE,"E2.top"),sQuery(id+"F0.wireOp",EDGE,"E3"),sQuery(id+"F0.wireOp",EDGE,"E7.MirrorC"),sQuery(id+"F0.wireOp",EDGE,"E8.MirrorC"),sQuery(id+"F0.wireOp",EDGE,"E9.MirrorCS"),sQuery(id+"F0.wireOp",EDGE,"E11.MirrorCS"),sQuery(id+"F0.wireOp",EDGE,"E12.MirrorC"),sQuery(id+"F0.wireOp",EDGE,"E13.MirrorC"),sQuery(id+"F0.wireOp",EDGE,"E14.MirrorCS"),sQuery(id+"F0.wireOp",EDGE,"E16.MirrorCS"),sQuery(id+"F0.wireOp",EDGE,"E17.MirrorCS"),sQuery(id+"F0.wireOp",EDGE,"E19.MirrorCS"),sQuery(id+"F0.wireOp",EDGE,"E20.MirrorC"),sQuery(id+"F0.wireOp",EDGE,"E21.MirrorC"),subQ3,subQ2,subQ1,subQ0,sQuery(id+"F0.wireOp",EDGE,"E25.bottom"),sQuery(id+"F0.wireOp",EDGE,"E25.top"),sQuery(id+"F0.wireOp",EDGE,"E25.left"),sQuery(id+"F0.wireOp",EDGE,"E25.right"),sQuery(id+"F0.wireOp",EDGE,"E26"),sQuery(id+"F0.wireOp",EDGE,"E27.trimOffspring"),sQuery(id+"F0.wireOp",EDGE,"E29"),sQuery(id+"F0.wireOp",EDGE,"E30.trimOffspring"),sQuery(id+"F0.wireOp",EDGE,"E32"),sQuery(id+"F0.wireOp",EDGE,"E33.trimOffspring"),sQuery(id+"F0.wireOp",EDGE,"E34"),sQuery(id+"F0.wireOp",EDGE,"E35.trimOffspring")])],"isStart":true}),makeQuery(id+"F2.opExtrude","CAP_FACE",FACE,{"disambiguationData":[OSD([subQ3,subQ2,subQ1,subQ0])],"isStart":true})]})});}
            var Q55;
            {var subQ0=sQuery(id+"F0.wireOp",EDGE,"E24.right");var subQ1=sQuery(id+"F0.wireOp",EDGE,"E24.left");var subQ2=sQuery(id+"F0.wireOp",EDGE,"E24.top");var subQ3=sQuery(id+"F0.wireOp",EDGE,"E24.bottom");Q55=makeQuery(id+"F4.boolean.opBoolean","SPLIT",FACE,{"disambiguationData":[TD([makeQuery(id+"F4.opExtrude","SWEPT_FACE",FACE,{"disambiguationData":[OSD([sQuery(id+"F3.wireOp",EDGE,"E41.3.0.1")])]})])],"derivedFrom":makeQuery(id+"F2.boolean.opBoolean","MERGE",FACE,{"derivedFrom":[makeQuery(id+"F1.opExtrude","CAP_FACE",FACE,{"disambiguationData":[OSD([sQuery(id+"F0.wireOp",EDGE,"E1"),sQuery(id+"F0.wireOp",EDGE,"E2.bottom"),sQuery(id+"F0.wireOp",EDGE,"E2.top"),sQuery(id+"F0.wireOp",EDGE,"E3"),sQuery(id+"F0.wireOp",EDGE,"E7.MirrorC"),sQuery(id+"F0.wireOp",EDGE,"E8.MirrorC"),sQuery(id+"F0.wireOp",EDGE,"E9.MirrorCS"),sQuery(id+"F0.wireOp",EDGE,"E11.MirrorCS"),sQuery(id+"F0.wireOp",EDGE,"E12.MirrorC"),sQuery(id+"F0.wireOp",EDGE,"E13.MirrorC"),sQuery(id+"F0.wireOp",EDGE,"E14.MirrorCS"),sQuery(id+"F0.wireOp",EDGE,"E16.MirrorCS"),sQuery(id+"F0.wireOp",EDGE,"E17.MirrorCS"),sQuery(id+"F0.wireOp",EDGE,"E19.MirrorCS"),sQuery(id+"F0.wireOp",EDGE,"E20.MirrorC"),sQuery(id+"F0.wireOp",EDGE,"E21.MirrorC"),subQ3,subQ2,subQ1,subQ0,sQuery(id+"F0.wireOp",EDGE,"E25.bottom"),sQuery(id+"F0.wireOp",EDGE,"E25.top"),sQuery(id+"F0.wireOp",EDGE,"E25.left"),sQuery(id+"F0.wireOp",EDGE,"E25.right"),sQuery(id+"F0.wireOp",EDGE,"E26"),sQuery(id+"F0.wireOp",EDGE,"E27.trimOffspring"),sQuery(id+"F0.wireOp",EDGE,"E29"),sQuery(id+"F0.wireOp",EDGE,"E30.trimOffspring"),sQuery(id+"F0.wireOp",EDGE,"E32"),sQuery(id+"F0.wireOp",EDGE,"E33.trimOffspring"),sQuery(id+"F0.wireOp",EDGE,"E34"),sQuery(id+"F0.wireOp",EDGE,"E35.trimOffspring")])],"isStart":true}),makeQuery(id+"F2.opExtrude","CAP_FACE",FACE,{"disambiguationData":[OSD([subQ3,subQ2,subQ1,subQ0])],"isStart":true})]})});}
            extrude(context, id + "F5", {"entities" : qUnion([Q0, Q1, Q2, Q3, Q4, Q5, Q6, Q7, Q8, Q9, Q10, Q11, Q12, Q13, Q14, Q15, Q16, Q17, Q18, Q19, Q20, Q21, Q22, Q23, Q24, Q25, Q26, Q27, Q28, Q29, Q30, Q31, Q32, Q33, Q34, Q35, Q36, Q37, Q38, Q39, Q40, Q41, Q42, Q43, Q44, Q45, Q46, Q47, Q48, Q49, Q50, Q51, Q52, Q53, Q54, Q55]), "operationType" : NewBodyOperationType.ADD, "depth" : 6 * mm});
        }
        {
            var Q0;
            Q0=makeQuery(id+"F3.imprint","IMPRINT",FACE,{"disambiguationData":[TD([[makeQuery(id+"F3.imprint","IMPRINT",EDGE,{"derivedFrom":sQuery(id+"F3.wireOp",EDGE,"E37.bottom")}),-1.0]])]});
            extrude(context, id + "F6", {"entities" : qUnion([Q0]), "operationType" : NewBodyOperationType.ADD, "depth" : 1.5 * mm});
        }
        {
            var Q0;
            Q0=makeQuery(id+"F3.imprint","IMPRINT",FACE,{"disambiguationData":[TD([[makeQuery(id+"F3.imprint","IMPRINT",EDGE,{"derivedFrom":sQuery(id+"F3.wireOp",EDGE,"E42")}),1.0]])]});
            var Q1;
            Q1=makeQuery(id+"F3.imprint","IMPRINT",FACE,{"disambiguationData":[TD([[makeQuery(id+"F3.imprint","IMPRINT",EDGE,{"derivedFrom":sQuery(id+"F3.wireOp",EDGE,"E43.1.0.0")}),1.0]])]});
            var Q2;
            Q2=makeQuery(id+"F3.imprint","IMPRINT",FACE,{"disambiguationData":[TD([[makeQuery(id+"F3.imprint","IMPRINT",EDGE,{"derivedFrom":sQuery(id+"F3.wireOp",EDGE,"E43.2.0.0")}),1.0]])]});
            var Q3;
            Q3=makeQuery(id+"F3.imprint","IMPRINT",FACE,{"disambiguationData":[TD([[makeQuery(id+"F3.imprint","IMPRINT",EDGE,{"derivedFrom":sQuery(id+"F3.wireOp",EDGE,"E43.3.0.0")}),1.0]])]});
            var Q4;
            Q4=makeQuery(id+"F3.imprint","IMPRINT",FACE,{"disambiguationData":[TD([[makeQuery(id+"F3.imprint","IMPRINT",EDGE,{"derivedFrom":sQuery(id+"F3.wireOp",EDGE,"E44.1.0.3")}),1.0]])]});
            var Q5;
            Q5=makeQuery(id+"F3.imprint","IMPRINT",FACE,{"disambiguationData":[TD([[makeQuery(id+"F3.imprint","IMPRINT",EDGE,{"derivedFrom":sQuery(id+"F3.wireOp",EDGE,"E44.1.0.2")}),1.0]])]});
            var Q6;
            Q6=makeQuery(id+"F3.imprint","IMPRINT",FACE,{"disambiguationData":[TD([[makeQuery(id+"F3.imprint","IMPRINT",EDGE,{"derivedFrom":sQuery(id+"F3.wireOp",EDGE,"E44.1.0.1")}),1.0]])]});
            var Q7;
            Q7=makeQuery(id+"F3.imprint","IMPRINT",FACE,{"disambiguationData":[TD([[makeQuery(id+"F3.imprint","IMPRINT",EDGE,{"derivedFrom":sQuery(id+"F3.wireOp",EDGE,"E44.1.0.0")}),1.0]])]});
            var Q8;
            Q8=makeQuery(id+"F3.imprint","IMPRINT",FACE,{"disambiguationData":[TD([[makeQuery(id+"F3.imprint","IMPRINT",EDGE,{"derivedFrom":sQuery(id+"F3.wireOp",EDGE,"E44.2.0.0")}),1.0]])]});
            var Q9;
            Q9=makeQuery(id+"F3.imprint","IMPRINT",FACE,{"disambiguationData":[TD([[makeQuery(id+"F3.imprint","IMPRINT",EDGE,{"derivedFrom":sQuery(id+"F3.wireOp",EDGE,"E44.2.0.1")}),1.0]])]});
            var Q10;
            Q10=makeQuery(id+"F3.imprint","IMPRINT",FACE,{"disambiguationData":[TD([[makeQuery(id+"F3.imprint","IMPRINT",EDGE,{"derivedFrom":sQuery(id+"F3.wireOp",EDGE,"E44.2.0.2")}),1.0]])]});
            var Q11;
            Q11=makeQuery(id+"F3.imprint","IMPRINT",FACE,{"disambiguationData":[TD([[makeQuery(id+"F3.imprint","IMPRINT",EDGE,{"derivedFrom":sQuery(id+"F3.wireOp",EDGE,"E44.2.0.3")}),1.0]])]});
            var Q12;
            Q12=makeQuery(id+"F3.imprint","IMPRINT",FACE,{"disambiguationData":[TD([[makeQuery(id+"F3.imprint","IMPRINT",EDGE,{"derivedFrom":sQuery(id+"F3.wireOp",EDGE,"E44.3.0.3")}),1.0]])]});
            var Q13;
            Q13=makeQuery(id+"F3.imprint","IMPRINT",FACE,{"disambiguationData":[TD([[makeQuery(id+"F3.imprint","IMPRINT",EDGE,{"derivedFrom":sQuery(id+"F3.wireOp",EDGE,"E44.3.0.2")}),1.0]])]});
            var Q14;
            Q14=makeQuery(id+"F3.imprint","IMPRINT",FACE,{"disambiguationData":[TD([[makeQuery(id+"F3.imprint","IMPRINT",EDGE,{"derivedFrom":sQuery(id+"F3.wireOp",EDGE,"E44.3.0.1")}),1.0]])]});
            var Q15;
            Q15=makeQuery(id+"F3.imprint","IMPRINT",FACE,{"disambiguationData":[TD([[makeQuery(id+"F3.imprint","IMPRINT",EDGE,{"derivedFrom":sQuery(id+"F3.wireOp",EDGE,"E44.3.0.0")}),1.0]])]});
            var Q16;
            Q16=makeQuery(id+"F3.imprint","IMPRINT",FACE,{"disambiguationData":[TD([[makeQuery(id+"F3.imprint","IMPRINT",EDGE,{"derivedFrom":sQuery(id+"F3.wireOp",EDGE,"E44.4.0.0")}),1.0]])]});
            var Q17;
            Q17=makeQuery(id+"F3.imprint","IMPRINT",FACE,{"disambiguationData":[TD([[makeQuery(id+"F3.imprint","IMPRINT",EDGE,{"derivedFrom":sQuery(id+"F3.wireOp",EDGE,"E44.4.0.1")}),1.0]])]});
            var Q18;
            Q18=makeQuery(id+"F3.imprint","IMPRINT",FACE,{"disambiguationData":[TD([[makeQuery(id+"F3.imprint","IMPRINT",EDGE,{"derivedFrom":sQuery(id+"F3.wireOp",EDGE,"E44.4.0.2")}),1.0]])]});
            var Q19;
            Q19=makeQuery(id+"F3.imprint","IMPRINT",FACE,{"disambiguationData":[TD([[makeQuery(id+"F3.imprint","IMPRINT",EDGE,{"derivedFrom":sQuery(id+"F3.wireOp",EDGE,"E44.4.0.3")}),1.0]])]});
            extrude(context, id + "F7", {"entities" : qUnion([Q0, Q1, Q2, Q3, Q4, Q5, Q6, Q7, Q8, Q9, Q10, Q11, Q12, Q13, Q14, Q15, Q16, Q17, Q18, Q19]), "operationType" : NewBodyOperationType.ADD, "depth" : 6 * mm});
        }
        {
            var Q0;
            Q0=makeQuery(id+"F2.opExtrude","CAP_FACE",FACE,{"disambiguationData":[OSD([sQuery(id+"F0.wireOp",EDGE,"E24.bottom"),sQuery(id+"F0.wireOp",EDGE,"E24.top"),sQuery(id+"F0.wireOp",EDGE,"E24.left"),sQuery(id+"F0.wireOp",EDGE,"E24.right")])],"isStart":false});
            var sketch = newSketch(context, id + "F8", { "sketchPlane" : qUnion([Q0])});
            skText(sketch, "E45", { "text": "7in Touch Screen", "fontName": "RobotoSlab-Regular.ttf"});
            const initialGuessF8  = {"E45": [-0.06091, -0.03235, 1, 0, 0.01]};
            skSetInitialGuess(sketch, initialGuessF8);
            skSolve(sketch);
        }
        {
            var Q0;
            Q0=makeQuery(id+"F8.imprint","IMPRINT",FACE,{"disambiguationData":[TD([[makeQuery(id+"F8.imprint","IMPRINT",EDGE,{"derivedFrom":sQuery(id+"F8.wireOp",EDGE,"E45.sketch_text.stroke-0")}),-1.0]])]});
            var Q1;
            Q1=makeQuery(id+"F8.imprint","IMPRINT",FACE,{"disambiguationData":[TD([[makeQuery(id+"F8.imprint","IMPRINT",EDGE,{"derivedFrom":sQuery(id+"F8.wireOp",EDGE,"E45.sketch_text.stroke-13")}),-1.0]])]});
            var Q2;
            Q2=makeQuery(id+"F8.imprint","IMPRINT",FACE,{"disambiguationData":[TD([[makeQuery(id+"F8.imprint","IMPRINT",EDGE,{"derivedFrom":sQuery(id+"F8.wireOp",EDGE,"E45.sketch_text.stroke-23")}),-1.0]])]});
            var Q3;
            Q3=makeQuery(id+"F8.imprint","IMPRINT",FACE,{"disambiguationData":[TD([[makeQuery(id+"F8.imprint","IMPRINT",EDGE,{"derivedFrom":sQuery(id+"F8.wireOp",EDGE,"E45.sketch_text.stroke-27")}),-1.0]])]});
            var Q4;
            Q4=makeQuery(id+"F8.imprint","IMPRINT",FACE,{"disambiguationData":[TD([[makeQuery(id+"F8.imprint","IMPRINT",EDGE,{"derivedFrom":sQuery(id+"F8.wireOp",EDGE,"E45.sketch_text.stroke-53")}),-1.0]])]});
            var Q5;
            Q5=makeQuery(id+"F8.imprint","IMPRINT",FACE,{"disambiguationData":[TD([[makeQuery(id+"F8.imprint","IMPRINT",EDGE,{"derivedFrom":sQuery(id+"F8.wireOp",EDGE,"E45.sketch_text.stroke-69")}),-1.0]])]});
            var Q6;
            Q6=makeQuery(id+"F8.imprint","IMPRINT",FACE,{"disambiguationData":[TD([[makeQuery(id+"F8.imprint","IMPRINT",EDGE,{"derivedFrom":sQuery(id+"F8.wireOp",EDGE,"E45.sketch_text.stroke-89")}),-1.0]])]});
            var Q7;
            Q7=makeQuery(id+"F8.imprint","IMPRINT",FACE,{"disambiguationData":[TD([[makeQuery(id+"F8.imprint","IMPRINT",EDGE,{"derivedFrom":sQuery(id+"F8.wireOp",EDGE,"E45.sketch_text.stroke-113")}),-1.0]])]});
            var Q8;
            Q8=makeQuery(id+"F8.imprint","IMPRINT",FACE,{"disambiguationData":[TD([[makeQuery(id+"F8.imprint","IMPRINT",EDGE,{"derivedFrom":sQuery(id+"F8.wireOp",EDGE,"E45.sketch_text.stroke-136")}),-1.0]])]});
            var Q9;
            Q9=makeQuery(id+"F8.imprint","IMPRINT",FACE,{"disambiguationData":[TD([[makeQuery(id+"F8.imprint","IMPRINT",EDGE,{"derivedFrom":sQuery(id+"F8.wireOp",EDGE,"E45.sketch_text.stroke-162")}),-1.0]])]});
            var Q10;
            Q10=makeQuery(id+"F8.imprint","IMPRINT",FACE,{"disambiguationData":[TD([[makeQuery(id+"F8.imprint","IMPRINT",EDGE,{"derivedFrom":sQuery(id+"F8.wireOp",EDGE,"E45.sketch_text.stroke-192")}),-1.0]])]});
            var Q11;
            Q11=makeQuery(id+"F8.imprint","IMPRINT",FACE,{"disambiguationData":[TD([[makeQuery(id+"F8.imprint","IMPRINT",EDGE,{"derivedFrom":sQuery(id+"F8.wireOp",EDGE,"E45.sketch_text.stroke-215")}),-1.0]])]});
            var Q12;
            Q12=makeQuery(id+"F8.imprint","IMPRINT",FACE,{"disambiguationData":[TD([[makeQuery(id+"F8.imprint","IMPRINT",EDGE,{"derivedFrom":sQuery(id+"F8.wireOp",EDGE,"E45.sketch_text.stroke-234")}),-1.0]])]});
            var Q13;
            Q13=makeQuery(id+"F8.imprint","IMPRINT",FACE,{"disambiguationData":[TD([[makeQuery(id+"F8.imprint","IMPRINT",EDGE,{"derivedFrom":sQuery(id+"F8.wireOp",EDGE,"E45.sketch_text.stroke-258")}),-1.0]])]});
            var Q14;
            Q14=makeQuery(id+"F8.imprint","IMPRINT",FACE,{"disambiguationData":[TD([[makeQuery(id+"F8.imprint","IMPRINT",EDGE,{"derivedFrom":sQuery(id+"F8.wireOp",EDGE,"E45.sketch_text.stroke-282")}),-1.0]])]});
            extrude(context, id + "F9", {"entities" : qUnion([Q0, Q1, Q2, Q3, Q4, Q5, Q6, Q7, Q8, Q9, Q10, Q11, Q12, Q13, Q14]), "operationType" : NewBodyOperationType.ADD, "depth" : .25 * mm});
        }
    });
